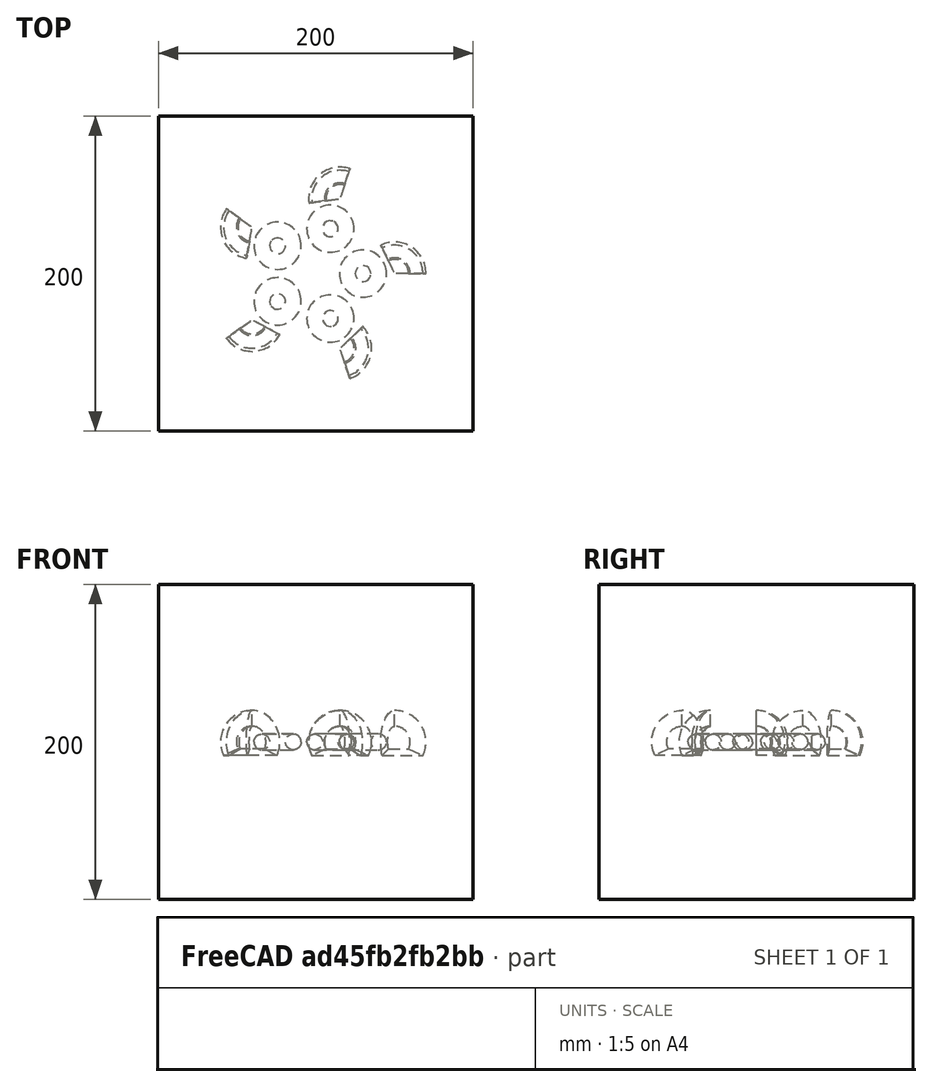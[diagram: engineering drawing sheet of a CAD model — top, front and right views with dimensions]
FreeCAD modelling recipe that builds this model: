
FCSTD DOCUMENT  (FreeCAD 0.19RUnknown)
Label: arrayTest-7
License: All rights reserved
LicenseURL: http://en.wikipedia.org/wiki/All_rights_reserved
objects: App::DocumentObjectGroupPython×1248, Part::FeaturePython×4, App::Part×2, Part::MultiFuse×1
note: 5 computed .brp shape members not serialized (recipe doc carries the construction recipe); baked Part::Feature solids carry a one-line shape summary decoded from their .brp

FEATURE [App::DocumentObjectGroupPython] HALFPI  # scripted group (container) (typed FeaturePython)
  name = HALFPI
  value = pi/2.
FEATURE [App::DocumentObjectGroupPython] PI  # scripted group (container) (typed FeaturePython)
  name = PI
  value = 1.*pi
FEATURE [App::DocumentObjectGroupPython] TWOPI  # scripted group (container) (typed FeaturePython)
  name = TWOPI
  value = 2.*pi
FEATURE [App::DocumentObjectGroupPython] Constants  # scripted group (container) (typed FeaturePython)
  Group = -> [HALFPI,PI,TWOPI]
FEATURE [App::DocumentObjectGroupPython] Variables  # scripted group (container) (typed FeaturePython)
FEATURE [App::DocumentObjectGroupPython] Quantities  # scripted group (container) (typed FeaturePython)
FEATURE [App::DocumentObjectGroupPython] Isotopes  # scripted group (container) (typed FeaturePython)
FEATURE [App::DocumentObjectGroupPython] Elements  # scripted group (container) (typed FeaturePython)
FEATURE [App::DocumentObjectGroupPython] G4Isotopes  # scripted group (container) (typed FeaturePython)
FEATURE [App::DocumentObjectGroupPython] H_element  # scripted group (container) (typed FeaturePython)
  Z = 1
  atom_value = 1.008
  formula = H
  name = H_element
FEATURE [App::DocumentObjectGroupPython] He_element  # scripted group (container) (typed FeaturePython)
  Z = 2
  atom_value = 4.0026
  formula = He
  name = He_element
FEATURE [App::DocumentObjectGroupPython] Li_element  # scripted group (container) (typed FeaturePython)
  Z = 3
  atom_value = 6.94
  formula = Li
  name = Li_element
FEATURE [App::DocumentObjectGroupPython] Be_element  # scripted group (container) (typed FeaturePython)
  Z = 4
  atom_value = 9.01218
  formula = Be
  name = Be_element
FEATURE [App::DocumentObjectGroupPython] B_element  # scripted group (container) (typed FeaturePython)
  Z = 5
  atom_value = 10.81
  formula = B
  name = B_element
FEATURE [App::DocumentObjectGroupPython] C_element  # scripted group (container) (typed FeaturePython)
  Z = 6
  atom_value = 12.011
  formula = C
  name = C_element
FEATURE [App::DocumentObjectGroupPython] N_element  # scripted group (container) (typed FeaturePython)
  Z = 7
  atom_value = 14.007
  formula = N
  name = N_element
FEATURE [App::DocumentObjectGroupPython] O_element  # scripted group (container) (typed FeaturePython)
  Z = 8
  atom_value = 15.999
  formula = O
  name = O_element
FEATURE [App::DocumentObjectGroupPython] F_element  # scripted group (container) (typed FeaturePython)
  Z = 9
  atom_value = 18.9984
  formula = F
  name = F_element
FEATURE [App::DocumentObjectGroupPython] Ne_element  # scripted group (container) (typed FeaturePython)
  Z = 10
  atom_value = 20.1797
  formula = Ne
  name = Ne_element
FEATURE [App::DocumentObjectGroupPython] Na_element  # scripted group (container) (typed FeaturePython)
  Z = 11
  atom_value = 22.9898
  formula = Na
  name = Na_element
FEATURE [App::DocumentObjectGroupPython] Mg_element  # scripted group (container) (typed FeaturePython)
  Z = 12
  atom_value = 24.305
  formula = Mg
  name = Mg_element
FEATURE [App::DocumentObjectGroupPython] Al_element  # scripted group (container) (typed FeaturePython)
  Z = 13
  atom_value = 26.9815
  formula = Al
  name = Al_element
FEATURE [App::DocumentObjectGroupPython] Si_element  # scripted group (container) (typed FeaturePython)
  Z = 14
  atom_value = 28.085
  formula = Si
  name = Si_element
FEATURE [App::DocumentObjectGroupPython] P_element  # scripted group (container) (typed FeaturePython)
  Z = 15
  atom_value = 30.9738
  formula = P
  name = P_element
FEATURE [App::DocumentObjectGroupPython] S_element  # scripted group (container) (typed FeaturePython)
  Z = 16
  atom_value = 32.06
  formula = S
  name = S_element
FEATURE [App::DocumentObjectGroupPython] Cl_element  # scripted group (container) (typed FeaturePython)
  Z = 17
  atom_value = 35.45
  formula = Cl
  name = Cl_element
FEATURE [App::DocumentObjectGroupPython] Ar_element  # scripted group (container) (typed FeaturePython)
  Z = 18
  atom_value = 39.95
  formula = Ar
  name = Ar_element
FEATURE [App::DocumentObjectGroupPython] K_element  # scripted group (container) (typed FeaturePython)
  Z = 19
  atom_value = 39.0983
  formula = K
  name = K_element
FEATURE [App::DocumentObjectGroupPython] Ca_element  # scripted group (container) (typed FeaturePython)
  Z = 20
  atom_value = 40.078
  formula = Ca
  name = Ca_element
FEATURE [App::DocumentObjectGroupPython] Sc_element  # scripted group (container) (typed FeaturePython)
  Z = 21
  atom_value = 44.9559
  formula = Sc
  name = Sc_element
FEATURE [App::DocumentObjectGroupPython] Ti_element  # scripted group (container) (typed FeaturePython)
  Z = 22
  atom_value = 47.867
  formula = Ti
  name = Ti_element
FEATURE [App::DocumentObjectGroupPython] V_element  # scripted group (container) (typed FeaturePython)
  Z = 23
  atom_value = 50.9415
  formula = V
  name = V_element
FEATURE [App::DocumentObjectGroupPython] Cr_element  # scripted group (container) (typed FeaturePython)
  Z = 24
  atom_value = 51.9961
  formula = Cr
  name = Cr_element
FEATURE [App::DocumentObjectGroupPython] Mn_element  # scripted group (container) (typed FeaturePython)
  Z = 25
  atom_value = 54.938
  formula = Mn
  name = Mn_element
FEATURE [App::DocumentObjectGroupPython] Fe_element  # scripted group (container) (typed FeaturePython)
  Z = 26
  atom_value = 55.845
  formula = Fe
  name = Fe_element
FEATURE [App::DocumentObjectGroupPython] Co_element  # scripted group (container) (typed FeaturePython)
  Z = 27
  atom_value = 58.9332
  formula = Co
  name = Co_element
FEATURE [App::DocumentObjectGroupPython] Ni_element  # scripted group (container) (typed FeaturePython)
  Z = 28
  atom_value = 58.6934
  formula = Ni
  name = Ni_element
FEATURE [App::DocumentObjectGroupPython] Cu_element  # scripted group (container) (typed FeaturePython)
  Z = 29
  atom_value = 63.546
  formula = Cu
  name = Cu_element
FEATURE [App::DocumentObjectGroupPython] Zn_element  # scripted group (container) (typed FeaturePython)
  Z = 30
  atom_value = 65.38
  formula = Zn
  name = Zn_element
FEATURE [App::DocumentObjectGroupPython] Ga_element  # scripted group (container) (typed FeaturePython)
  Z = 31
  atom_value = 69.723
  formula = Ga
  name = Ga_element
FEATURE [App::DocumentObjectGroupPython] Ge_element  # scripted group (container) (typed FeaturePython)
  Z = 32
  atom_value = 72.63
  formula = Ge
  name = Ge_element
FEATURE [App::DocumentObjectGroupPython] As_element  # scripted group (container) (typed FeaturePython)
  Z = 33
  atom_value = 74.9216
  formula = As
  name = As_element
FEATURE [App::DocumentObjectGroupPython] Se_element  # scripted group (container) (typed FeaturePython)
  Z = 34
  atom_value = 78.971
  formula = Se
  name = Se_element
FEATURE [App::DocumentObjectGroupPython] Br_element  # scripted group (container) (typed FeaturePython)
  Z = 35
  atom_value = 79.904
  formula = Br
  name = Br_element
FEATURE [App::DocumentObjectGroupPython] Kr_element  # scripted group (container) (typed FeaturePython)
  Z = 36
  atom_value = 83.798
  formula = Kr
  name = Kr_element
FEATURE [App::DocumentObjectGroupPython] Rb_element  # scripted group (container) (typed FeaturePython)
  Z = 37
  atom_value = 85.4678
  formula = Rb
  name = Rb_element
FEATURE [App::DocumentObjectGroupPython] Sr_element  # scripted group (container) (typed FeaturePython)
  Z = 38
  atom_value = 87.62
  formula = Sr
  name = Sr_element
FEATURE [App::DocumentObjectGroupPython] Y_element  # scripted group (container) (typed FeaturePython)
  Z = 39
  atom_value = 88.9058
  formula = Y
  name = Y_element
FEATURE [App::DocumentObjectGroupPython] Zr_element  # scripted group (container) (typed FeaturePython)
  Z = 40
  atom_value = 91.224
  formula = Zr
  name = Zr_element
FEATURE [App::DocumentObjectGroupPython] Nb_element  # scripted group (container) (typed FeaturePython)
  Z = 41
  atom_value = 92.9064
  formula = Nb
  name = Nb_element
FEATURE [App::DocumentObjectGroupPython] Mo_element  # scripted group (container) (typed FeaturePython)
  Z = 42
  atom_value = 95.95
  formula = Mo
  name = Mo_element
FEATURE [App::DocumentObjectGroupPython] Tc_element  # scripted group (container) (typed FeaturePython)
  Z = 43
  atom_value = 97
  formula = Tc
  name = Tc_element
FEATURE [App::DocumentObjectGroupPython] Ru_element  # scripted group (container) (typed FeaturePython)
  Z = 44
  atom_value = 101.07
  formula = Ru
  name = Ru_element
FEATURE [App::DocumentObjectGroupPython] Rh_element  # scripted group (container) (typed FeaturePython)
  Z = 45
  atom_value = 102.905
  formula = Rh
  name = Rh_element
FEATURE [App::DocumentObjectGroupPython] Pd_element  # scripted group (container) (typed FeaturePython)
  Z = 46
  atom_value = 106.42
  formula = Pd
  name = Pd_element
FEATURE [App::DocumentObjectGroupPython] Ag_element  # scripted group (container) (typed FeaturePython)
  Z = 47
  atom_value = 107.868
  formula = Ag
  name = Ag_element
FEATURE [App::DocumentObjectGroupPython] Cd_element  # scripted group (container) (typed FeaturePython)
  Z = 48
  atom_value = 112.414
  formula = Cd
  name = Cd_element
FEATURE [App::DocumentObjectGroupPython] In_element  # scripted group (container) (typed FeaturePython)
  Z = 49
  atom_value = 114.818
  formula = In
  name = In_element
FEATURE [App::DocumentObjectGroupPython] Sn_element  # scripted group (container) (typed FeaturePython)
  Z = 50
  atom_value = 118.71
  formula = Sn
  name = Sn_element
FEATURE [App::DocumentObjectGroupPython] Sb_element  # scripted group (container) (typed FeaturePython)
  Z = 51
  atom_value = 121.76
  formula = Sb
  name = Sb_element
FEATURE [App::DocumentObjectGroupPython] Te_element  # scripted group (container) (typed FeaturePython)
  Z = 52
  atom_value = 127.6
  formula = Te
  name = Te_element
FEATURE [App::DocumentObjectGroupPython] I_element  # scripted group (container) (typed FeaturePython)
  Z = 53
  atom_value = 126.904
  formula = I
  name = I_element
FEATURE [App::DocumentObjectGroupPython] Xe_element  # scripted group (container) (typed FeaturePython)
  Z = 54
  atom_value = 131.293
  formula = Xe
  name = Xe_element
FEATURE [App::DocumentObjectGroupPython] Cs_element  # scripted group (container) (typed FeaturePython)
  Z = 55
  atom_value = 132.905
  formula = Cs
  name = Cs_element
FEATURE [App::DocumentObjectGroupPython] Ba_element  # scripted group (container) (typed FeaturePython)
  Z = 56
  atom_value = 137.327
  formula = Ba
  name = Ba_element
FEATURE [App::DocumentObjectGroupPython] La_element  # scripted group (container) (typed FeaturePython)
  Z = 57
  atom_value = 138.905
  formula = La
  name = La_element
FEATURE [App::DocumentObjectGroupPython] Ce_element  # scripted group (container) (typed FeaturePython)
  Z = 58
  atom_value = 140.116
  formula = Ce
  name = Ce_element
FEATURE [App::DocumentObjectGroupPython] Pr_element  # scripted group (container) (typed FeaturePython)
  Z = 59
  atom_value = 140.908
  formula = Pr
  name = Pr_element
FEATURE [App::DocumentObjectGroupPython] Nd_element  # scripted group (container) (typed FeaturePython)
  Z = 60
  atom_value = 144.242
  formula = Nd
  name = Nd_element
FEATURE [App::DocumentObjectGroupPython] Pm_element  # scripted group (container) (typed FeaturePython)
  Z = 61
  atom_value = 145
  formula = Pm
  name = Pm_element
FEATURE [App::DocumentObjectGroupPython] Sm_element  # scripted group (container) (typed FeaturePython)
  Z = 62
  atom_value = 150.36
  formula = Sm
  name = Sm_element
FEATURE [App::DocumentObjectGroupPython] Eu_element  # scripted group (container) (typed FeaturePython)
  Z = 63
  atom_value = 151.964
  formula = Eu
  name = Eu_element
FEATURE [App::DocumentObjectGroupPython] Gd_element  # scripted group (container) (typed FeaturePython)
  Z = 64
  atom_value = 157.25
  formula = Gd
  name = Gd_element
FEATURE [App::DocumentObjectGroupPython] Tb_element  # scripted group (container) (typed FeaturePython)
  Z = 65
  atom_value = 158.925
  formula = Tb
  name = Tb_element
FEATURE [App::DocumentObjectGroupPython] Dy_element  # scripted group (container) (typed FeaturePython)
  Z = 66
  atom_value = 162.5
  formula = Dy
  name = Dy_element
FEATURE [App::DocumentObjectGroupPython] Ho_element  # scripted group (container) (typed FeaturePython)
  Z = 67
  atom_value = 164.93
  formula = Ho
  name = Ho_element
FEATURE [App::DocumentObjectGroupPython] Er_element  # scripted group (container) (typed FeaturePython)
  Z = 68
  atom_value = 167.259
  formula = Er
  name = Er_element
FEATURE [App::DocumentObjectGroupPython] Tm_element  # scripted group (container) (typed FeaturePython)
  Z = 69
  atom_value = 168.934
  formula = Tm
  name = Tm_element
FEATURE [App::DocumentObjectGroupPython] Yb_element  # scripted group (container) (typed FeaturePython)
  Z = 70
  atom_value = 173.045
  formula = Yb
  name = Yb_element
FEATURE [App::DocumentObjectGroupPython] Lu_element  # scripted group (container) (typed FeaturePython)
  Z = 71
  atom_value = 174.967
  formula = Lu
  name = Lu_element
FEATURE [App::DocumentObjectGroupPython] Hf_element  # scripted group (container) (typed FeaturePython)
  Z = 72
  atom_value = 178.49
  formula = Hf
  name = Hf_element
FEATURE [App::DocumentObjectGroupPython] Ta_element  # scripted group (container) (typed FeaturePython)
  Z = 73
  atom_value = 180.948
  formula = Ta
  name = Ta_element
FEATURE [App::DocumentObjectGroupPython] W_element  # scripted group (container) (typed FeaturePython)
  Z = 74
  atom_value = 183.84
  formula = W
  name = W_element
FEATURE [App::DocumentObjectGroupPython] Re_element  # scripted group (container) (typed FeaturePython)
  Z = 75
  atom_value = 186.207
  formula = Re
  name = Re_element
FEATURE [App::DocumentObjectGroupPython] Os_element  # scripted group (container) (typed FeaturePython)
  Z = 76
  atom_value = 190.23
  formula = Os
  name = Os_element
FEATURE [App::DocumentObjectGroupPython] Ir_element  # scripted group (container) (typed FeaturePython)
  Z = 77
  atom_value = 192.217
  formula = Ir
  name = Ir_element
FEATURE [App::DocumentObjectGroupPython] Pt_element  # scripted group (container) (typed FeaturePython)
  Z = 78
  atom_value = 195.084
  formula = Pt
  name = Pt_element
FEATURE [App::DocumentObjectGroupPython] Au_element  # scripted group (container) (typed FeaturePython)
  Z = 79
  atom_value = 196.967
  formula = Au
  name = Au_element
FEATURE [App::DocumentObjectGroupPython] Hg_element  # scripted group (container) (typed FeaturePython)
  Z = 80
  atom_value = 200.592
  formula = Hg
  name = Hg_element
FEATURE [App::DocumentObjectGroupPython] Tl_element  # scripted group (container) (typed FeaturePython)
  Z = 81
  atom_value = 204.38
  formula = Tl
  name = Tl_element
FEATURE [App::DocumentObjectGroupPython] Pb_element  # scripted group (container) (typed FeaturePython)
  Z = 82
  atom_value = 207.2
  formula = Pb
  name = Pb_element
FEATURE [App::DocumentObjectGroupPython] Bi_element  # scripted group (container) (typed FeaturePython)
  Z = 83
  atom_value = 208.98
  formula = Bi
  name = Bi_element
FEATURE [App::DocumentObjectGroupPython] Po_element  # scripted group (container) (typed FeaturePython)
  Z = 84
  atom_value = 209
  formula = Po
  name = Po_element
FEATURE [App::DocumentObjectGroupPython] At_element  # scripted group (container) (typed FeaturePython)
  Z = 85
  atom_value = 210
  formula = At
  name = At_element
FEATURE [App::DocumentObjectGroupPython] Rn_element  # scripted group (container) (typed FeaturePython)
  Z = 86
  atom_value = 222
  formula = Rn
  name = Rn_element
FEATURE [App::DocumentObjectGroupPython] Fr_element  # scripted group (container) (typed FeaturePython)
  Z = 87
  atom_value = 223
  formula = Fr
  name = Fr_element
FEATURE [App::DocumentObjectGroupPython] Ra_element  # scripted group (container) (typed FeaturePython)
  Z = 88
  atom_value = 226
  formula = Ra
  name = Ra_element
FEATURE [App::DocumentObjectGroupPython] Ac_element  # scripted group (container) (typed FeaturePython)
  Z = 89
  atom_value = 227
  formula = Ac
  name = Ac_element
FEATURE [App::DocumentObjectGroupPython] Th_element  # scripted group (container) (typed FeaturePython)
  Z = 90
  atom_value = 232.038
  formula = Th
  name = Th_element
FEATURE [App::DocumentObjectGroupPython] Pa_element  # scripted group (container) (typed FeaturePython)
  Z = 91
  atom_value = 231.036
  formula = Pa
  name = Pa_element
FEATURE [App::DocumentObjectGroupPython] U_element  # scripted group (container) (typed FeaturePython)
  Z = 92
  atom_value = 238.029
  formula = U
  name = U_element
FEATURE [App::DocumentObjectGroupPython] Np_element  # scripted group (container) (typed FeaturePython)
  Z = 93
  atom_value = 237
  formula = Np
  name = Np_element
FEATURE [App::DocumentObjectGroupPython] Pu_element  # scripted group (container) (typed FeaturePython)
  Z = 94
  atom_value = 244
  formula = Pu
  name = Pu_element
FEATURE [App::DocumentObjectGroupPython] Am_element  # scripted group (container) (typed FeaturePython)
  Z = 95
  atom_value = 243
  formula = Am
  name = Am_element
FEATURE [App::DocumentObjectGroupPython] Cm_element  # scripted group (container) (typed FeaturePython)
  Z = 96
  atom_value = 247
  formula = Cm
  name = Cm_element
FEATURE [App::DocumentObjectGroupPython] Bk_element  # scripted group (container) (typed FeaturePython)
  Z = 97
  atom_value = 247
  formula = Bk
  name = Bk_element
FEATURE [App::DocumentObjectGroupPython] Cf_element  # scripted group (container) (typed FeaturePython)
  Z = 98
  atom_value = 251
  formula = Cf
  name = Cf_element
FEATURE [App::DocumentObjectGroupPython] G4Elements  # scripted group (container) (typed FeaturePython)
  Group = -> [H_element,He_element,Li_element,Be_element,B_element,C_element,N_element,O_element,F_element,Ne_element,Na_element,Mg_element,Al_element,Si_element,P_element,S_element,Cl_element,Ar_element,K_element,Ca_element,Sc_element,Ti_element,V_element,Cr_element,Mn_element,Fe_element,Co_element,Ni_element,Cu_element,Zn_element,Ga_element,Ge_element,As_element,Se_element,Br_element,Kr_element,Rb_element,+61 more]
FEATURE [App::DocumentObjectGroupPython] H_element001  label="H_element : 0.101"  # scripted group (container) (typed FeaturePython)
  n = 0.101327
FEATURE [App::DocumentObjectGroupPython] C_element001  label="C_element : 0.775"  # scripted group (container) (typed FeaturePython)
  n = 0.7755
FEATURE [App::DocumentObjectGroupPython] N_element001  label="N_element : 0.035"  # scripted group (container) (typed FeaturePython)
  n = 0.035057
FEATURE [App::DocumentObjectGroupPython] O_element001  label="O_element : 0.052"  # scripted group (container) (typed FeaturePython)
  n = 0.0523159
FEATURE [App::DocumentObjectGroupPython] F_element001  label="F_element : 0.017"  # scripted group (container) (typed FeaturePython)
  n = 0.017422
FEATURE [App::DocumentObjectGroupPython] Ca_element001  label="Ca_element : 0.018"  # scripted group (container) (typed FeaturePython)
  n = 0.018378
FEATURE [App::DocumentObjectGroupPython] G4_A_150_TISSUE  label="G4_A-150_TISSUE"  # scripted group (container) (typed FeaturePython)
  Dunit = g/cm3
  Dvalue = 1.127
  Group = -> [H_element001,C_element001,N_element001,O_element001,F_element001,Ca_element001]
  conduct = 2
  density = 1
  expand = 3
  formula = G4_A-150_TISSUE
  name = G4_A-150_TISSUE
  specific = 4
FEATURE [App::DocumentObjectGroupPython] C_element002  label="C_element : 3"  # scripted group (container) (typed FeaturePython)
  n = 3
  ref = C_element
FEATURE [App::DocumentObjectGroupPython] H_element002  label="H_element : 6"  # scripted group (container) (typed FeaturePython)
  n = 6
  ref = H_element
FEATURE [App::DocumentObjectGroupPython] O_element002  label="O_element : 1"  # scripted group (container) (typed FeaturePython)
  n = 1
  ref = O_element
FEATURE [App::DocumentObjectGroupPython] G4_ACETONE  # scripted group (container) (typed FeaturePython)
  Dunit = g/cm3
  Dvalue = 0.7899
  Group = -> [C_element002,H_element002,O_element002]
  conduct = 2
  density = 1
  expand = 3
  formula = G4_ACETONE
  name = G4_ACETONE
  specific = 4
FEATURE [App::DocumentObjectGroupPython] C_element003  label="C_element : 2"  # scripted group (container) (typed FeaturePython)
  n = 2
  ref = C_element
FEATURE [App::DocumentObjectGroupPython] H_element003  label="H_element : 2"  # scripted group (container) (typed FeaturePython)
  n = 2
  ref = H_element
FEATURE [App::DocumentObjectGroupPython] G4_ACETYLENE  # scripted group (container) (typed FeaturePython)
  Dunit = g/cm3
  Dvalue = 0.0010967
  Group = -> [C_element003,H_element003]
  conduct = 2
  density = 1
  expand = 3
  formula = G4_ACETYLENE
  name = G4_ACETYLENE
  specific = 4
FEATURE [App::DocumentObjectGroupPython] C_element004  label="C_element : 5"  # scripted group (container) (typed FeaturePython)
  n = 5
  ref = C_element
FEATURE [App::DocumentObjectGroupPython] H_element004  label="H_element : 5"  # scripted group (container) (typed FeaturePython)
  n = 5
  ref = H_element
FEATURE [App::DocumentObjectGroupPython] N_element002  label="N_element : 5"  # scripted group (container) (typed FeaturePython)
  n = 5
  ref = N_element
FEATURE [App::DocumentObjectGroupPython] G4_ADENINE  # scripted group (container) (typed FeaturePython)
  Dunit = g/cm3
  Dvalue = 1.6
  Group = -> [C_element004,H_element004,N_element002]
  conduct = 2
  density = 1
  expand = 3
  formula = G4_ADENINE
  name = G4_ADENINE
  specific = 4
FEATURE [App::DocumentObjectGroupPython] H_element005  label="H_element : 0.114"  # scripted group (container) (typed FeaturePython)
  n = 0.114
FEATURE [App::DocumentObjectGroupPython] C_element005  label="C_element : 0.598"  # scripted group (container) (typed FeaturePython)
  n = 0.598
FEATURE [App::DocumentObjectGroupPython] N_element003  label="N_element : 0.007"  # scripted group (container) (typed FeaturePython)
  n = 0.007
FEATURE [App::DocumentObjectGroupPython] O_element003  label="O_element : 0.278"  # scripted group (container) (typed FeaturePython)
  n = 0.278
FEATURE [App::DocumentObjectGroupPython] Na_element001  label="Na_element : 0.001"  # scripted group (container) (typed FeaturePython)
  n = 0.001
FEATURE [App::DocumentObjectGroupPython] S_element001  label="S_element : 0.001"  # scripted group (container) (typed FeaturePython)
  n = 0.001
FEATURE [App::DocumentObjectGroupPython] Cl_element001  label="Cl_element : 0.001"  # scripted group (container) (typed FeaturePython)
  n = 0.001
FEATURE [App::DocumentObjectGroupPython] G4_ADIPOSE_TISSUE_ICRP  # scripted group (container) (typed FeaturePython)
  Dunit = g/cm3
  Dvalue = 0.95
  Group = -> [H_element005,C_element005,N_element003,O_element003,Na_element001,S_element001,Cl_element001]
  conduct = 2
  density = 1
  expand = 3
  formula = G4_ADIPOSE_TISSUE_ICRP
  name = G4_ADIPOSE_TISSUE_ICRP
  specific = 4
FEATURE [App::DocumentObjectGroupPython] C_element006  label="C_element : 0.000"  # scripted group (container) (typed FeaturePython)
  n = 0.000124
FEATURE [App::DocumentObjectGroupPython] N_element004  label="N_element : 0.755"  # scripted group (container) (typed FeaturePython)
  n = 0.755268
FEATURE [App::DocumentObjectGroupPython] O_element004  label="O_element : 0.232"  # scripted group (container) (typed FeaturePython)
  n = 0.231781
FEATURE [App::DocumentObjectGroupPython] Ar_element001  label="Ar_element : 0.013"  # scripted group (container) (typed FeaturePython)
  n = 0.012827
FEATURE [App::DocumentObjectGroupPython] G4_AIR  # scripted group (container) (typed FeaturePython)
  Dunit = g/cm3
  Dvalue = 0.00120479
  Group = -> [C_element006,N_element004,O_element004,Ar_element001]
  conduct = 2
  density = 1
  expand = 3
  formula = G4_AIR
  name = G4_AIR
  specific = 4
FEATURE [App::DocumentObjectGroupPython] C_element007  label="C_element : 006"  # scripted group (container) (typed FeaturePython)
  n = 3
  ref = C_element
FEATURE [App::DocumentObjectGroupPython] H_element006  label="H_element : 7"  # scripted group (container) (typed FeaturePython)
  n = 7
  ref = H_element
FEATURE [App::DocumentObjectGroupPython] N_element005  label="N_element : 1"  # scripted group (container) (typed FeaturePython)
  n = 1
  ref = N_element
FEATURE [App::DocumentObjectGroupPython] O_element005  label="O_element : 2"  # scripted group (container) (typed FeaturePython)
  n = 2
  ref = O_element
FEATURE [App::DocumentObjectGroupPython] G4_ALANINE  # scripted group (container) (typed FeaturePython)
  Dunit = g/cm3
  Dvalue = 1.42
  Group = -> [C_element007,H_element006,N_element005,O_element005]
  conduct = 2
  density = 1
  expand = 3
  formula = G4_ALANINE
  name = G4_ALANINE
  specific = 4
FEATURE [App::DocumentObjectGroupPython] Al_element001  label="Al_element : 2"  # scripted group (container) (typed FeaturePython)
  n = 2
  ref = Al_element
FEATURE [App::DocumentObjectGroupPython] O_element006  label="O_element : 3"  # scripted group (container) (typed FeaturePython)
  n = 3
  ref = O_element
FEATURE [App::DocumentObjectGroupPython] G4_ALUMINUM_OXIDE  # scripted group (container) (typed FeaturePython)
  Dunit = g/cm3
  Dvalue = 3.97
  Group = -> [Al_element001,O_element006]
  conduct = 2
  density = 1
  expand = 3
  formula = G4_ALUMINUM_OXIDE
  name = G4_ALUMINUM_OXIDE
  specific = 4
FEATURE [App::DocumentObjectGroupPython] H_element007  label="H_element : 0.106"  # scripted group (container) (typed FeaturePython)
  n = 0.10593
FEATURE [App::DocumentObjectGroupPython] C_element008  label="C_element : 0.789"  # scripted group (container) (typed FeaturePython)
  n = 0.788974
FEATURE [App::DocumentObjectGroupPython] O_element007  label="O_element : 0.105"  # scripted group (container) (typed FeaturePython)
  n = 0.105096
FEATURE [App::DocumentObjectGroupPython] G4_AMBER  # scripted group (container) (typed FeaturePython)
  Dunit = g/cm3
  Dvalue = 1.1
  Group = -> [H_element007,C_element008,O_element007]
  conduct = 2
  density = 1
  expand = 3
  formula = G4_AMBER
  name = G4_AMBER
  specific = 4
FEATURE [App::DocumentObjectGroupPython] N_element006  label="N_element : 006"  # scripted group (container) (typed FeaturePython)
  n = 1
  ref = N_element
FEATURE [App::DocumentObjectGroupPython] H_element008  label="H_element : 3"  # scripted group (container) (typed FeaturePython)
  n = 3
  ref = H_element
FEATURE [App::DocumentObjectGroupPython] G4_AMMONIA  # scripted group (container) (typed FeaturePython)
  Dunit = g/cm3
  Dvalue = 0.000826019
  Group = -> [N_element006,H_element008]
  conduct = 2
  density = 1
  expand = 3
  formula = G4_AMMONIA
  name = G4_AMMONIA
  specific = 4
FEATURE [App::DocumentObjectGroupPython] C_element009  label="C_element : 6"  # scripted group (container) (typed FeaturePython)
  n = 6
  ref = C_element
FEATURE [App::DocumentObjectGroupPython] H_element009  label="H_element : 008"  # scripted group (container) (typed FeaturePython)
  n = 7
  ref = H_element
FEATURE [App::DocumentObjectGroupPython] N_element007  label="N_element : 007"  # scripted group (container) (typed FeaturePython)
  n = 1
  ref = N_element
FEATURE [App::DocumentObjectGroupPython] G4_ANILINE  # scripted group (container) (typed FeaturePython)
  Dunit = g/cm3
  Dvalue = 1.0235
  Group = -> [C_element009,H_element009,N_element007]
  conduct = 2
  density = 1
  expand = 3
  formula = G4_ANILINE
  name = G4_ANILINE
  specific = 4
FEATURE [App::DocumentObjectGroupPython] C_element010  label="C_element : 14"  # scripted group (container) (typed FeaturePython)
  n = 14
  ref = C_element
FEATURE [App::DocumentObjectGroupPython] H_element010  label="H_element : 10"  # scripted group (container) (typed FeaturePython)
  n = 10
  ref = H_element
FEATURE [App::DocumentObjectGroupPython] G4_ANTHRACENE  # scripted group (container) (typed FeaturePython)
  Dunit = g/cm3
  Dvalue = 1.283
  Group = -> [C_element010,H_element010]
  conduct = 2
  density = 1
  expand = 3
  formula = G4_ANTHRACENE
  name = G4_ANTHRACENE
  specific = 4
FEATURE [App::DocumentObjectGroupPython] H_element011  label="H_element : 0.065"  # scripted group (container) (typed FeaturePython)
  n = 0.0654709
FEATURE [App::DocumentObjectGroupPython] C_element011  label="C_element : 0.537"  # scripted group (container) (typed FeaturePython)
  n = 0.536944
FEATURE [App::DocumentObjectGroupPython] N_element008  label="N_element : 0.021"  # scripted group (container) (typed FeaturePython)
  n = 0.0215
FEATURE [App::DocumentObjectGroupPython] O_element008  label="O_element : 0.032"  # scripted group (container) (typed FeaturePython)
  n = 0.032085
FEATURE [App::DocumentObjectGroupPython] F_element002  label="F_element : 0.167"  # scripted group (container) (typed FeaturePython)
  n = 0.167411
FEATURE [App::DocumentObjectGroupPython] Ca_element002  label="Ca_element : 0.177"  # scripted group (container) (typed FeaturePython)
  n = 0.176589
FEATURE [App::DocumentObjectGroupPython] G4_B_100_BONE  label="G4_B-100_BONE"  # scripted group (container) (typed FeaturePython)
  Dunit = g/cm3
  Dvalue = 1.45
  Group = -> [H_element011,C_element011,N_element008,O_element008,F_element002,Ca_element002]
  conduct = 2
  density = 1
  expand = 3
  formula = G4_B-100_BONE
  name = G4_B-100_BONE
  specific = 4
FEATURE [App::DocumentObjectGroupPython] H_element012  label="H_element : 0.057"  # scripted group (container) (typed FeaturePython)
  n = 0.057441
FEATURE [App::DocumentObjectGroupPython] C_element012  label="C_element : 0.790"  # scripted group (container) (typed FeaturePython)
  n = 0.774591
FEATURE [App::DocumentObjectGroupPython] O_element009  label="O_element : 0.168"  # scripted group (container) (typed FeaturePython)
  n = 0.167968
FEATURE [App::DocumentObjectGroupPython] G4_BAKELITE  # scripted group (container) (typed FeaturePython)
  Dunit = g/cm3
  Dvalue = 1.25
  Group = -> [H_element012,C_element012,O_element009]
  conduct = 2
  density = 1
  expand = 3
  formula = G4_BAKELITE
  name = G4_BAKELITE
  specific = 4
FEATURE [App::DocumentObjectGroupPython] Ba_element001  label="Ba_element : 1"  # scripted group (container) (typed FeaturePython)
  n = 1
  ref = Ba_element
FEATURE [App::DocumentObjectGroupPython] F_element003  label="F_element : 2"  # scripted group (container) (typed FeaturePython)
  n = 2
  ref = F_element
FEATURE [App::DocumentObjectGroupPython] G4_BARIUM_FLUORIDE  # scripted group (container) (typed FeaturePython)
  Dunit = g/cm3
  Dvalue = 4.89
  Group = -> [Ba_element001,F_element003]
  conduct = 2
  density = 1
  expand = 3
  formula = G4_BARIUM_FLUORIDE
  name = G4_BARIUM_FLUORIDE
  specific = 4
FEATURE [App::DocumentObjectGroupPython] Ba_element002  label="Ba_element : 002"  # scripted group (container) (typed FeaturePython)
  n = 1
  ref = Ba_element
FEATURE [App::DocumentObjectGroupPython] S_element002  label="S_element : 1"  # scripted group (container) (typed FeaturePython)
  n = 1
  ref = S_element
FEATURE [App::DocumentObjectGroupPython] O_element010  label="O_element : 4"  # scripted group (container) (typed FeaturePython)
  n = 4
  ref = O_element
FEATURE [App::DocumentObjectGroupPython] G4_BARIUM_SULFATE  # scripted group (container) (typed FeaturePython)
  Dunit = g/cm3
  Dvalue = 4.5
  Group = -> [Ba_element002,S_element002,O_element010]
  conduct = 2
  density = 1
  expand = 3
  formula = G4_BARIUM_SULFATE
  name = G4_BARIUM_SULFATE
  specific = 4
FEATURE [App::DocumentObjectGroupPython] C_element013  label="C_element : 007"  # scripted group (container) (typed FeaturePython)
  n = 6
  ref = C_element
FEATURE [App::DocumentObjectGroupPython] H_element013  label="H_element : 009"  # scripted group (container) (typed FeaturePython)
  n = 6
  ref = H_element
FEATURE [App::DocumentObjectGroupPython] G4_BENZENE  # scripted group (container) (typed FeaturePython)
  Dunit = g/cm3
  Dvalue = 0.87865
  Group = -> [C_element013,H_element013]
  conduct = 2
  density = 1
  expand = 3
  formula = G4_BENZENE
  name = G4_BENZENE
  specific = 4
FEATURE [App::DocumentObjectGroupPython] Be_element001  label="Be_element : 1"  # scripted group (container) (typed FeaturePython)
  n = 1
  ref = Be_element
FEATURE [App::DocumentObjectGroupPython] O_element011  label="O_element : 005"  # scripted group (container) (typed FeaturePython)
  n = 1
  ref = O_element
FEATURE [App::DocumentObjectGroupPython] G4_BERYLLIUM_OXIDE  # scripted group (container) (typed FeaturePython)
  Dunit = g/cm3
  Dvalue = 3.01
  Group = -> [Be_element001,O_element011]
  conduct = 2
  density = 1
  expand = 3
  formula = G4_BERYLLIUM_OXIDE
  name = G4_BERYLLIUM_OXIDE
  specific = 4
FEATURE [App::DocumentObjectGroupPython] Bi_element001  label="Bi_element : 4"  # scripted group (container) (typed FeaturePython)
  n = 4
  ref = Bi_element
FEATURE [App::DocumentObjectGroupPython] Ge_element001  label="Ge_element : 3"  # scripted group (container) (typed FeaturePython)
  n = 3
  ref = Ge_element
FEATURE [App::DocumentObjectGroupPython] O_element012  label="O_element : 12"  # scripted group (container) (typed FeaturePython)
  n = 12
  ref = O_element
FEATURE [App::DocumentObjectGroupPython] G4_BGO  # scripted group (container) (typed FeaturePython)
  Dunit = g/cm3
  Dvalue = 7.13
  Group = -> [Bi_element001,Ge_element001,O_element012]
  conduct = 2
  density = 1
  expand = 3
  formula = G4_BGO
  name = G4_BGO
  specific = 4
FEATURE [App::DocumentObjectGroupPython] H_element014  label="H_element : 0.102"  # scripted group (container) (typed FeaturePython)
  n = 0.102
FEATURE [App::DocumentObjectGroupPython] C_element014  label="C_element : 0.110"  # scripted group (container) (typed FeaturePython)
  n = 0.11
FEATURE [App::DocumentObjectGroupPython] N_element009  label="N_element : 0.033"  # scripted group (container) (typed FeaturePython)
  n = 0.033
FEATURE [App::DocumentObjectGroupPython] O_element013  label="O_element : 0.745"  # scripted group (container) (typed FeaturePython)
  n = 0.745
FEATURE [App::DocumentObjectGroupPython] Na_element002  label="Na_element : 0.002"  # scripted group (container) (typed FeaturePython)
  n = 0.001
FEATURE [App::DocumentObjectGroupPython] P_element001  label="P_element : 0.001"  # scripted group (container) (typed FeaturePython)
  n = 0.001
FEATURE [App::DocumentObjectGroupPython] S_element003  label="S_element : 0.002"  # scripted group (container) (typed FeaturePython)
  n = 0.002
FEATURE [App::DocumentObjectGroupPython] Cl_element002  label="Cl_element : 0.003"  # scripted group (container) (typed FeaturePython)
  n = 0.003
FEATURE [App::DocumentObjectGroupPython] K_element001  label="K_element : 0.002"  # scripted group (container) (typed FeaturePython)
  n = 0.002
FEATURE [App::DocumentObjectGroupPython] Fe_element001  label="Fe_element : 0.001"  # scripted group (container) (typed FeaturePython)
  n = 0.001
FEATURE [App::DocumentObjectGroupPython] G4_BLOOD_ICRP  # scripted group (container) (typed FeaturePython)
  Dunit = g/cm3
  Dvalue = 1.06
  Group = -> [H_element014,C_element014,N_element009,O_element013,Na_element002,P_element001,S_element003,Cl_element002,K_element001,Fe_element001]
  conduct = 2
  density = 1
  expand = 3
  formula = G4_BLOOD_ICRP
  name = G4_BLOOD_ICRP
  specific = 4
FEATURE [App::DocumentObjectGroupPython] H_element015  label="H_element : 0.064"  # scripted group (container) (typed FeaturePython)
  n = 0.064
FEATURE [App::DocumentObjectGroupPython] C_element015  label="C_element : 0.278"  # scripted group (container) (typed FeaturePython)
  n = 0.278
FEATURE [App::DocumentObjectGroupPython] N_element010  label="N_element : 0.027"  # scripted group (container) (typed FeaturePython)
  n = 0.027
FEATURE [App::DocumentObjectGroupPython] O_element014  label="O_element : 0.410"  # scripted group (container) (typed FeaturePython)
  n = 0.41
FEATURE [App::DocumentObjectGroupPython] Mg_element001  label="Mg_element : 0.002"  # scripted group (container) (typed FeaturePython)
  n = 0.002
FEATURE [App::DocumentObjectGroupPython] P_element002  label="P_element : 0.070"  # scripted group (container) (typed FeaturePython)
  n = 0.07
FEATURE [App::DocumentObjectGroupPython] S_element004  label="S_element : 0.003"  # scripted group (container) (typed FeaturePython)
  n = 0.002
FEATURE [App::DocumentObjectGroupPython] Ca_element003  label="Ca_element : 0.147"  # scripted group (container) (typed FeaturePython)
  n = 0.147
FEATURE [App::DocumentObjectGroupPython] G4_BONE_COMPACT_ICRU  # scripted group (container) (typed FeaturePython)
  Dunit = g/cm3
  Dvalue = 1.85
  Group = -> [H_element015,C_element015,N_element010,O_element014,Mg_element001,P_element002,S_element004,Ca_element003]
  conduct = 2
  density = 1
  expand = 3
  formula = G4_BONE_COMPACT_ICRU
  name = G4_BONE_COMPACT_ICRU
  specific = 4
FEATURE [App::DocumentObjectGroupPython] H_element016  label="H_element : 0.034"  # scripted group (container) (typed FeaturePython)
  n = 0.034
FEATURE [App::DocumentObjectGroupPython] C_element016  label="C_element : 0.155"  # scripted group (container) (typed FeaturePython)
  n = 0.155
FEATURE [App::DocumentObjectGroupPython] N_element011  label="N_element : 0.042"  # scripted group (container) (typed FeaturePython)
  n = 0.042
FEATURE [App::DocumentObjectGroupPython] O_element015  label="O_element : 0.435"  # scripted group (container) (typed FeaturePython)
  n = 0.435
FEATURE [App::DocumentObjectGroupPython] Na_element003  label="Na_element : 0.003"  # scripted group (container) (typed FeaturePython)
  n = 0.001
FEATURE [App::DocumentObjectGroupPython] Mg_element002  label="Mg_element : 0.003"  # scripted group (container) (typed FeaturePython)
  n = 0.002
FEATURE [App::DocumentObjectGroupPython] P_element003  label="P_element : 0.103"  # scripted group (container) (typed FeaturePython)
  n = 0.103
FEATURE [App::DocumentObjectGroupPython] S_element005  label="S_element : 0.004"  # scripted group (container) (typed FeaturePython)
  n = 0.003
FEATURE [App::DocumentObjectGroupPython] Ca_element004  label="Ca_element : 0.225"  # scripted group (container) (typed FeaturePython)
  n = 0.225
FEATURE [App::DocumentObjectGroupPython] G4_BONE_CORTICAL_ICRP  # scripted group (container) (typed FeaturePython)
  Dunit = g/cm3
  Dvalue = 1.92
  Group = -> [H_element016,C_element016,N_element011,O_element015,Na_element003,Mg_element002,P_element003,S_element005,Ca_element004]
  conduct = 2
  density = 1
  expand = 3
  formula = G4_BONE_CORTICAL_ICRP
  name = G4_BONE_CORTICAL_ICRP
  specific = 4
FEATURE [App::DocumentObjectGroupPython] B_element001  label="B_element : 4"  # scripted group (container) (typed FeaturePython)
  n = 4
  ref = B_element
FEATURE [App::DocumentObjectGroupPython] C_element017  label="C_element : 1"  # scripted group (container) (typed FeaturePython)
  n = 1
  ref = C_element
FEATURE [App::DocumentObjectGroupPython] G4_BORON_CARBIDE  # scripted group (container) (typed FeaturePython)
  Dunit = g/cm3
  Dvalue = 2.52
  Group = -> [B_element001,C_element017]
  conduct = 2
  density = 1
  expand = 3
  formula = G4_BORON_CARBIDE
  name = G4_BORON_CARBIDE
  specific = 4
FEATURE [App::DocumentObjectGroupPython] B_element002  label="B_element : 2"  # scripted group (container) (typed FeaturePython)
  n = 2
  ref = B_element
FEATURE [App::DocumentObjectGroupPython] O_element016  label="O_element : 006"  # scripted group (container) (typed FeaturePython)
  n = 3
  ref = O_element
FEATURE [App::DocumentObjectGroupPython] G4_BORON_OXIDE  # scripted group (container) (typed FeaturePython)
  Dunit = g/cm3
  Dvalue = 1.812
  Group = -> [B_element002,O_element016]
  conduct = 2
  density = 1
  expand = 3
  formula = G4_BORON_OXIDE
  name = G4_BORON_OXIDE
  specific = 4
FEATURE [App::DocumentObjectGroupPython] H_element017  label="H_element : 0.107"  # scripted group (container) (typed FeaturePython)
  n = 0.107
FEATURE [App::DocumentObjectGroupPython] C_element018  label="C_element : 0.145"  # scripted group (container) (typed FeaturePython)
  n = 0.145
FEATURE [App::DocumentObjectGroupPython] N_element012  label="N_element : 0.022"  # scripted group (container) (typed FeaturePython)
  n = 0.022
FEATURE [App::DocumentObjectGroupPython] O_element017  label="O_element : 0.712"  # scripted group (container) (typed FeaturePython)
  n = 0.712
FEATURE [App::DocumentObjectGroupPython] Na_element004  label="Na_element : 0.004"  # scripted group (container) (typed FeaturePython)
  n = 0.002
FEATURE [App::DocumentObjectGroupPython] P_element004  label="P_element : 0.004"  # scripted group (container) (typed FeaturePython)
  n = 0.004
FEATURE [App::DocumentObjectGroupPython] S_element006  label="S_element : 0.005"  # scripted group (container) (typed FeaturePython)
  n = 0.002
FEATURE [App::DocumentObjectGroupPython] Cl_element003  label="Cl_element : 0.004"  # scripted group (container) (typed FeaturePython)
  n = 0.003
FEATURE [App::DocumentObjectGroupPython] K_element002  label="K_element : 0.003"  # scripted group (container) (typed FeaturePython)
  n = 0.003
FEATURE [App::DocumentObjectGroupPython] G4_BRAIN_ICRP  # scripted group (container) (typed FeaturePython)
  Dunit = g/cm3
  Dvalue = 1.04
  Group = -> [H_element017,C_element018,N_element012,O_element017,Na_element004,P_element004,S_element006,Cl_element003,K_element002]
  conduct = 2
  density = 1
  expand = 3
  formula = G4_BRAIN_ICRP
  name = G4_BRAIN_ICRP
  specific = 4
FEATURE [App::DocumentObjectGroupPython] C_element019  label="C_element : 4"  # scripted group (container) (typed FeaturePython)
  n = 4
  ref = C_element
FEATURE [App::DocumentObjectGroupPython] H_element018  label="H_element : 010"  # scripted group (container) (typed FeaturePython)
  n = 10
  ref = H_element
FEATURE [App::DocumentObjectGroupPython] G4_BUTANE  # scripted group (container) (typed FeaturePython)
  Dunit = g/cm3
  Dvalue = 0.00249343
  Group = -> [C_element019,H_element018]
  conduct = 2
  density = 1
  expand = 3
  formula = G4_BUTANE
  name = G4_BUTANE
  specific = 4
FEATURE [App::DocumentObjectGroupPython] C_element020  label="C_element : 008"  # scripted group (container) (typed FeaturePython)
  n = 4
  ref = C_element
FEATURE [App::DocumentObjectGroupPython] H_element019  label="H_element : 011"  # scripted group (container) (typed FeaturePython)
  n = 10
  ref = H_element
FEATURE [App::DocumentObjectGroupPython] O_element018  label="O_element : 007"  # scripted group (container) (typed FeaturePython)
  n = 1
  ref = O_element
FEATURE [App::DocumentObjectGroupPython] G4_N_BUTYL_ALCOHOL  label="G4_N-BUTYL_ALCOHOL"  # scripted group (container) (typed FeaturePython)
  Dunit = g/cm3
  Dvalue = 0.8098
  Group = -> [C_element020,H_element019,O_element018]
  conduct = 2
  density = 1
  expand = 3
  formula = G4_N-BUTYL_ALCOHOL
  name = G4_N-BUTYL_ALCOHOL
  specific = 4
FEATURE [App::DocumentObjectGroupPython] H_element020  label="H_element : 0.025"  # scripted group (container) (typed FeaturePython)
  n = 0.02468
FEATURE [App::DocumentObjectGroupPython] C_element021  label="C_element : 0.502"  # scripted group (container) (typed FeaturePython)
  n = 0.501611
FEATURE [App::DocumentObjectGroupPython] O_element019  label="O_element : 0.005"  # scripted group (container) (typed FeaturePython)
  n = 0.004527
FEATURE [App::DocumentObjectGroupPython] F_element004  label="F_element : 0.465"  # scripted group (container) (typed FeaturePython)
  n = 0.465209
FEATURE [App::DocumentObjectGroupPython] Si_element001  label="Si_element : 0.004"  # scripted group (container) (typed FeaturePython)
  n = 0.003973
FEATURE [App::DocumentObjectGroupPython] G4_C_552  label="G4_C-552"  # scripted group (container) (typed FeaturePython)
  Dunit = g/cm3
  Dvalue = 1.76
  Group = -> [H_element020,C_element021,O_element019,F_element004,Si_element001]
  conduct = 2
  density = 1
  expand = 3
  formula = G4_C-552
  name = G4_C-552
  specific = 4
FEATURE [App::DocumentObjectGroupPython] Cd_element001  label="Cd_element : 1"  # scripted group (container) (typed FeaturePython)
  n = 1
  ref = Cd_element
FEATURE [App::DocumentObjectGroupPython] Te_element001  label="Te_element : 1"  # scripted group (container) (typed FeaturePython)
  n = 1
  ref = Te_element
FEATURE [App::DocumentObjectGroupPython] G4_CADMIUM_TELLURIDE  # scripted group (container) (typed FeaturePython)
  Dunit = g/cm3
  Dvalue = 6.2
  Group = -> [Cd_element001,Te_element001]
  conduct = 2
  density = 1
  expand = 3
  formula = G4_CADMIUM_TELLURIDE
  name = G4_CADMIUM_TELLURIDE
  specific = 4
FEATURE [App::DocumentObjectGroupPython] Cd_element002  label="Cd_element : 002"  # scripted group (container) (typed FeaturePython)
  n = 1
  ref = Cd_element
FEATURE [App::DocumentObjectGroupPython] W_element001  label="W_element : 1"  # scripted group (container) (typed FeaturePython)
  n = 1
  ref = W_element
FEATURE [App::DocumentObjectGroupPython] O_element020  label="O_element : 008"  # scripted group (container) (typed FeaturePython)
  n = 4
  ref = O_element
FEATURE [App::DocumentObjectGroupPython] G4_CADMIUM_TUNGSTATE  # scripted group (container) (typed FeaturePython)
  Dunit = g/cm3
  Dvalue = 7.9
  Group = -> [Cd_element002,W_element001,O_element020]
  conduct = 2
  density = 1
  expand = 3
  formula = G4_CADMIUM_TUNGSTATE
  name = G4_CADMIUM_TUNGSTATE
  specific = 4
FEATURE [App::DocumentObjectGroupPython] Ca_element005  label="Ca_element : 1"  # scripted group (container) (typed FeaturePython)
  n = 1
  ref = Ca_element
FEATURE [App::DocumentObjectGroupPython] C_element022  label="C_element : 009"  # scripted group (container) (typed FeaturePython)
  n = 1
  ref = C_element
FEATURE [App::DocumentObjectGroupPython] O_element021  label="O_element : 009"  # scripted group (container) (typed FeaturePython)
  n = 3
  ref = O_element
FEATURE [App::DocumentObjectGroupPython] G4_CALCIUM_CARBONATE  # scripted group (container) (typed FeaturePython)
  Dunit = g/cm3
  Dvalue = 2.8
  Group = -> [Ca_element005,C_element022,O_element021]
  conduct = 2
  density = 1
  expand = 3
  formula = G4_CALCIUM_CARBONATE
  name = G4_CALCIUM_CARBONATE
  specific = 4
FEATURE [App::DocumentObjectGroupPython] Ca_element006  label="Ca_element : 002"  # scripted group (container) (typed FeaturePython)
  n = 1
  ref = Ca_element
FEATURE [App::DocumentObjectGroupPython] F_element005  label="F_element : 003"  # scripted group (container) (typed FeaturePython)
  n = 2
  ref = F_element
FEATURE [App::DocumentObjectGroupPython] G4_CALCIUM_FLUORIDE  # scripted group (container) (typed FeaturePython)
  Dunit = g/cm3
  Dvalue = 3.18
  Group = -> [Ca_element006,F_element005]
  conduct = 2
  density = 1
  expand = 3
  formula = G4_CALCIUM_FLUORIDE
  name = G4_CALCIUM_FLUORIDE
  specific = 4
FEATURE [App::DocumentObjectGroupPython] Ca_element007  label="Ca_element : 003"  # scripted group (container) (typed FeaturePython)
  n = 1
  ref = Ca_element
FEATURE [App::DocumentObjectGroupPython] O_element022  label="O_element : 010"  # scripted group (container) (typed FeaturePython)
  n = 1
  ref = O_element
FEATURE [App::DocumentObjectGroupPython] G4_CALCIUM_OXIDE  # scripted group (container) (typed FeaturePython)
  Dunit = g/cm3
  Dvalue = 3.3
  Group = -> [Ca_element007,O_element022]
  conduct = 2
  density = 1
  expand = 3
  formula = G4_CALCIUM_OXIDE
  name = G4_CALCIUM_OXIDE
  specific = 4
FEATURE [App::DocumentObjectGroupPython] Ca_element008  label="Ca_element : 004"  # scripted group (container) (typed FeaturePython)
  n = 1
  ref = Ca_element
FEATURE [App::DocumentObjectGroupPython] S_element007  label="S_element : 002"  # scripted group (container) (typed FeaturePython)
  n = 1
  ref = S_element
FEATURE [App::DocumentObjectGroupPython] O_element023  label="O_element : 011"  # scripted group (container) (typed FeaturePython)
  n = 4
  ref = O_element
FEATURE [App::DocumentObjectGroupPython] G4_CALCIUM_SULFATE  # scripted group (container) (typed FeaturePython)
  Dunit = g/cm3
  Dvalue = 2.96
  Group = -> [Ca_element008,S_element007,O_element023]
  conduct = 2
  density = 1
  expand = 3
  formula = G4_CALCIUM_SULFATE
  name = G4_CALCIUM_SULFATE
  specific = 4
FEATURE [App::DocumentObjectGroupPython] Ca_element009  label="Ca_element : 005"  # scripted group (container) (typed FeaturePython)
  n = 1
  ref = Ca_element
FEATURE [App::DocumentObjectGroupPython] W_element002  label="W_element : 002"  # scripted group (container) (typed FeaturePython)
  n = 1
  ref = W_element
FEATURE [App::DocumentObjectGroupPython] O_element024  label="O_element : 012"  # scripted group (container) (typed FeaturePython)
  n = 4
  ref = O_element
FEATURE [App::DocumentObjectGroupPython] G4_CALCIUM_TUNGSTATE  # scripted group (container) (typed FeaturePython)
  Dunit = g/cm3
  Dvalue = 6.062
  Group = -> [Ca_element009,W_element002,O_element024]
  conduct = 2
  density = 1
  expand = 3
  formula = G4_CALCIUM_TUNGSTATE
  name = G4_CALCIUM_TUNGSTATE
  specific = 4
FEATURE [App::DocumentObjectGroupPython] C_element023  label="C_element : 010"  # scripted group (container) (typed FeaturePython)
  n = 1
  ref = C_element
FEATURE [App::DocumentObjectGroupPython] O_element025  label="O_element : 013"  # scripted group (container) (typed FeaturePython)
  n = 2
  ref = O_element
FEATURE [App::DocumentObjectGroupPython] G4_CARBON_DIOXIDE  # scripted group (container) (typed FeaturePython)
  Dunit = g/cm3
  Dvalue = 0.00184212
  Group = -> [C_element023,O_element025]
  conduct = 2
  density = 1
  expand = 3
  formula = G4_CARBON_DIOXIDE
  name = G4_CARBON_DIOXIDE
  specific = 4
FEATURE [App::DocumentObjectGroupPython] C_element024  label="C_element : 011"  # scripted group (container) (typed FeaturePython)
  n = 1
  ref = C_element
FEATURE [App::DocumentObjectGroupPython] Cl_element004  label="Cl_element : 4"  # scripted group (container) (typed FeaturePython)
  n = 4
  ref = Cl_element
FEATURE [App::DocumentObjectGroupPython] G4_CARBON_TETRACHLORIDE  # scripted group (container) (typed FeaturePython)
  Dunit = g/cm3
  Dvalue = 1.594
  Group = -> [C_element024,Cl_element004]
  conduct = 2
  density = 1
  expand = 3
  formula = G4_CARBON_TETRACHLORIDE
  name = G4_CARBON_TETRACHLORIDE
  specific = 4
FEATURE [App::DocumentObjectGroupPython] C_element025  label="C_element : 012"  # scripted group (container) (typed FeaturePython)
  n = 6
  ref = C_element
FEATURE [App::DocumentObjectGroupPython] H_element021  label="H_element : 012"  # scripted group (container) (typed FeaturePython)
  n = 10
  ref = H_element
FEATURE [App::DocumentObjectGroupPython] O_element026  label="O_element : 5"  # scripted group (container) (typed FeaturePython)
  n = 5
  ref = O_element
FEATURE [App::DocumentObjectGroupPython] G4_CELLULOSE_CELLOPHANE  # scripted group (container) (typed FeaturePython)
  Dunit = g/cm3
  Dvalue = 1.42
  Group = -> [C_element025,H_element021,O_element026]
  conduct = 2
  density = 1
  expand = 3
  formula = G4_CELLULOSE_CELLOPHANE
  name = G4_CELLULOSE_CELLOPHANE
  specific = 4
FEATURE [App::DocumentObjectGroupPython] H_element022  label="H_element : 0.067"  # scripted group (container) (typed FeaturePython)
  n = 0.067125
FEATURE [App::DocumentObjectGroupPython] C_element026  label="C_element : 0.545"  # scripted group (container) (typed FeaturePython)
  n = 0.545403
FEATURE [App::DocumentObjectGroupPython] O_element027  label="O_element : 0.387"  # scripted group (container) (typed FeaturePython)
  n = 0.387472
FEATURE [App::DocumentObjectGroupPython] G4_CELLULOSE_BUTYRATE  # scripted group (container) (typed FeaturePython)
  Dunit = g/cm3
  Dvalue = 1.2
  Group = -> [H_element022,C_element026,O_element027]
  conduct = 2
  density = 1
  expand = 3
  formula = G4_CELLULOSE_BUTYRATE
  name = G4_CELLULOSE_BUTYRATE
  specific = 4
FEATURE [App::DocumentObjectGroupPython] H_element023  label="H_element : 0.029"  # scripted group (container) (typed FeaturePython)
  n = 0.029216
FEATURE [App::DocumentObjectGroupPython] C_element027  label="C_element : 0.271"  # scripted group (container) (typed FeaturePython)
  n = 0.271296
FEATURE [App::DocumentObjectGroupPython] N_element013  label="N_element : 0.121"  # scripted group (container) (typed FeaturePython)
  n = 0.121276
FEATURE [App::DocumentObjectGroupPython] O_element028  label="O_element : 0.578"  # scripted group (container) (typed FeaturePython)
  n = 0.578212
FEATURE [App::DocumentObjectGroupPython] G4_CELLULOSE_NITRATE  # scripted group (container) (typed FeaturePython)
  Dunit = g/cm3
  Dvalue = 1.49
  Group = -> [H_element023,C_element027,N_element013,O_element028]
  conduct = 2
  density = 1
  expand = 3
  formula = G4_CELLULOSE_NITRATE
  name = G4_CELLULOSE_NITRATE
  specific = 4
FEATURE [App::DocumentObjectGroupPython] H_element024  label="H_element : 0.108"  # scripted group (container) (typed FeaturePython)
  n = 0.107596
FEATURE [App::DocumentObjectGroupPython] N_element014  label="N_element : 0.001"  # scripted group (container) (typed FeaturePython)
  n = 0.0008
FEATURE [App::DocumentObjectGroupPython] O_element029  label="O_element : 0.875"  # scripted group (container) (typed FeaturePython)
  n = 0.874976
FEATURE [App::DocumentObjectGroupPython] S_element008  label="S_element : 0.015"  # scripted group (container) (typed FeaturePython)
  n = 0.014627
FEATURE [App::DocumentObjectGroupPython] Ce_element001  label="Ce_element : 0.002"  # scripted group (container) (typed FeaturePython)
  n = 0.002001
FEATURE [App::DocumentObjectGroupPython] G4_CERIC_SULFATE  # scripted group (container) (typed FeaturePython)
  Dunit = g/cm3
  Dvalue = 1.03
  Group = -> [H_element024,N_element014,O_element029,S_element008,Ce_element001]
  conduct = 2
  density = 1
  expand = 3
  formula = G4_CERIC_SULFATE
  name = G4_CERIC_SULFATE
  specific = 4
FEATURE [App::DocumentObjectGroupPython] Cs_element001  label="Cs_element : 1"  # scripted group (container) (typed FeaturePython)
  n = 1
  ref = Cs_element
FEATURE [App::DocumentObjectGroupPython] F_element006  label="F_element : 1"  # scripted group (container) (typed FeaturePython)
  n = 1
  ref = F_element
FEATURE [App::DocumentObjectGroupPython] G4_CESIUM_FLUORIDE  # scripted group (container) (typed FeaturePython)
  Dunit = g/cm3
  Dvalue = 4.115
  Group = -> [Cs_element001,F_element006]
  conduct = 2
  density = 1
  expand = 3
  formula = G4_CESIUM_FLUORIDE
  name = G4_CESIUM_FLUORIDE
  specific = 4
FEATURE [App::DocumentObjectGroupPython] Cs_element002  label="Cs_element : 002"  # scripted group (container) (typed FeaturePython)
  n = 1
  ref = Cs_element
FEATURE [App::DocumentObjectGroupPython] I_element001  label="I_element : 1"  # scripted group (container) (typed FeaturePython)
  n = 1
  ref = I_element
FEATURE [App::DocumentObjectGroupPython] G4_CESIUM_IODIDE  # scripted group (container) (typed FeaturePython)
  Dunit = g/cm3
  Dvalue = 4.51
  Group = -> [Cs_element002,I_element001]
  conduct = 2
  density = 1
  expand = 3
  formula = G4_CESIUM_IODIDE
  name = G4_CESIUM_IODIDE
  specific = 4
FEATURE [App::DocumentObjectGroupPython] C_element028  label="C_element : 013"  # scripted group (container) (typed FeaturePython)
  n = 6
  ref = C_element
FEATURE [App::DocumentObjectGroupPython] H_element025  label="H_element : 013"  # scripted group (container) (typed FeaturePython)
  n = 5
  ref = H_element
FEATURE [App::DocumentObjectGroupPython] Cl_element005  label="Cl_element : 1"  # scripted group (container) (typed FeaturePython)
  n = 1
  ref = Cl_element
FEATURE [App::DocumentObjectGroupPython] G4_CHLOROBENZENE  # scripted group (container) (typed FeaturePython)
  Dunit = g/cm3
  Dvalue = 1.1058
  Group = -> [C_element028,H_element025,Cl_element005]
  conduct = 2
  density = 1
  expand = 3
  formula = G4_CHLOROBENZENE
  name = G4_CHLOROBENZENE
  specific = 4
FEATURE [App::DocumentObjectGroupPython] C_element029  label="C_element : 014"  # scripted group (container) (typed FeaturePython)
  n = 1
  ref = C_element
FEATURE [App::DocumentObjectGroupPython] H_element026  label="H_element : 1"  # scripted group (container) (typed FeaturePython)
  n = 1
  ref = H_element
FEATURE [App::DocumentObjectGroupPython] Cl_element006  label="Cl_element : 3"  # scripted group (container) (typed FeaturePython)
  n = 3
  ref = Cl_element
FEATURE [App::DocumentObjectGroupPython] G4_CHLOROFORM  # scripted group (container) (typed FeaturePython)
  Dunit = g/cm3
  Dvalue = 1.4832
  Group = -> [C_element029,H_element026,Cl_element006]
  conduct = 2
  density = 1
  expand = 3
  formula = G4_CHLOROFORM
  name = G4_CHLOROFORM
  specific = 4
FEATURE [App::DocumentObjectGroupPython] H_element027  label="H_element : 0.010"  # scripted group (container) (typed FeaturePython)
  n = 0.01
FEATURE [App::DocumentObjectGroupPython] C_element030  label="C_element : 0.001"  # scripted group (container) (typed FeaturePython)
  n = 0.001
FEATURE [App::DocumentObjectGroupPython] O_element030  label="O_element : 0.529"  # scripted group (container) (typed FeaturePython)
  n = 0.529107
FEATURE [App::DocumentObjectGroupPython] Na_element005  label="Na_element : 0.016"  # scripted group (container) (typed FeaturePython)
  n = 0.016
FEATURE [App::DocumentObjectGroupPython] Mg_element003  label="Mg_element : 0.004"  # scripted group (container) (typed FeaturePython)
  n = 0.002
FEATURE [App::DocumentObjectGroupPython] Al_element002  label="Al_element : 0.034"  # scripted group (container) (typed FeaturePython)
  n = 0.033872
FEATURE [App::DocumentObjectGroupPython] Si_element002  label="Si_element : 0.337"  # scripted group (container) (typed FeaturePython)
  n = 0.337021
FEATURE [App::DocumentObjectGroupPython] K_element003  label="K_element : 0.013"  # scripted group (container) (typed FeaturePython)
  n = 0.013
FEATURE [App::DocumentObjectGroupPython] Ca_element010  label="Ca_element : 0.044"  # scripted group (container) (typed FeaturePython)
  n = 0.044
FEATURE [App::DocumentObjectGroupPython] Fe_element002  label="Fe_element : 0.014"  # scripted group (container) (typed FeaturePython)
  n = 0.014
FEATURE [App::DocumentObjectGroupPython] G4_CONCRETE  # scripted group (container) (typed FeaturePython)
  Dunit = g/cm3
  Dvalue = 2.3
  Group = -> [H_element027,C_element030,O_element030,Na_element005,Mg_element003,Al_element002,Si_element002,K_element003,Ca_element010,Fe_element002]
  conduct = 2
  density = 1
  expand = 3
  formula = G4_CONCRETE
  name = G4_CONCRETE
  specific = 4
FEATURE [App::DocumentObjectGroupPython] C_element031  label="C_element : 015"  # scripted group (container) (typed FeaturePython)
  n = 6
  ref = C_element
FEATURE [App::DocumentObjectGroupPython] H_element028  label="H_element : 12"  # scripted group (container) (typed FeaturePython)
  n = 12
  ref = H_element
FEATURE [App::DocumentObjectGroupPython] G4_CYCLOHEXANE  # scripted group (container) (typed FeaturePython)
  Dunit = g/cm3
  Dvalue = 0.779
  Group = -> [C_element031,H_element028]
  conduct = 2
  density = 1
  expand = 3
  formula = G4_CYCLOHEXANE
  name = G4_CYCLOHEXANE
  specific = 4
FEATURE [App::DocumentObjectGroupPython] C_element032  label="C_element : 016"  # scripted group (container) (typed FeaturePython)
  n = 6
  ref = C_element
FEATURE [App::DocumentObjectGroupPython] H_element029  label="H_element : 4"  # scripted group (container) (typed FeaturePython)
  n = 4
  ref = H_element
FEATURE [App::DocumentObjectGroupPython] Cl_element007  label="Cl_element : 2"  # scripted group (container) (typed FeaturePython)
  n = 2
  ref = Cl_element
FEATURE [App::DocumentObjectGroupPython] G4_1_2_DICHLOROBENZENE  label="G4_1.2-DICHLOROBENZENE"  # scripted group (container) (typed FeaturePython)
  Dunit = g/cm3
  Dvalue = 1.3048
  Group = -> [C_element032,H_element029,Cl_element007]
  conduct = 2
  density = 1
  expand = 3
  formula = G4_1.2-DICHLOROBENZENE
  name = G4_1.2-DICHLOROBENZENE
  specific = 4
FEATURE [App::DocumentObjectGroupPython] C_element033  label="C_element : 017"  # scripted group (container) (typed FeaturePython)
  n = 4
  ref = C_element
FEATURE [App::DocumentObjectGroupPython] H_element030  label="H_element : 8"  # scripted group (container) (typed FeaturePython)
  n = 8
  ref = H_element
FEATURE [App::DocumentObjectGroupPython] O_element031  label="O_element : 014"  # scripted group (container) (typed FeaturePython)
  n = 1
  ref = O_element
FEATURE [App::DocumentObjectGroupPython] Cl_element008  label="Cl_element : 005"  # scripted group (container) (typed FeaturePython)
  n = 2
  ref = Cl_element
FEATURE [App::DocumentObjectGroupPython] G4_DICHLORODIETHYL_ETHER  # scripted group (container) (typed FeaturePython)
  Dunit = g/cm3
  Dvalue = 1.2199
  Group = -> [C_element033,H_element030,O_element031,Cl_element008]
  conduct = 2
  density = 1
  expand = 3
  formula = G4_DICHLORODIETHYL_ETHER
  name = G4_DICHLORODIETHYL_ETHER
  specific = 4
FEATURE [App::DocumentObjectGroupPython] C_element034  label="C_element : 018"  # scripted group (container) (typed FeaturePython)
  n = 2
  ref = C_element
FEATURE [App::DocumentObjectGroupPython] H_element031  label="H_element : 014"  # scripted group (container) (typed FeaturePython)
  n = 4
  ref = H_element
FEATURE [App::DocumentObjectGroupPython] Cl_element009  label="Cl_element : 006"  # scripted group (container) (typed FeaturePython)
  n = 2
  ref = Cl_element
FEATURE [App::DocumentObjectGroupPython] G4_1_2_DICHLOROETHANE  label="G4_1.2-DICHLOROETHANE"  # scripted group (container) (typed FeaturePython)
  Dunit = g/cm3
  Dvalue = 1.2351
  Group = -> [C_element034,H_element031,Cl_element009]
  conduct = 2
  density = 1
  expand = 3
  formula = G4_1.2-DICHLOROETHANE
  name = G4_1.2-DICHLOROETHANE
  specific = 4
FEATURE [App::DocumentObjectGroupPython] C_element035  label="C_element : 019"  # scripted group (container) (typed FeaturePython)
  n = 4
  ref = C_element
FEATURE [App::DocumentObjectGroupPython] H_element032  label="H_element : 015"  # scripted group (container) (typed FeaturePython)
  n = 10
  ref = H_element
FEATURE [App::DocumentObjectGroupPython] O_element032  label="O_element : 015"  # scripted group (container) (typed FeaturePython)
  n = 1
  ref = O_element
FEATURE [App::DocumentObjectGroupPython] G4_DIETHYL_ETHER  # scripted group (container) (typed FeaturePython)
  Dunit = g/cm3
  Dvalue = 0.71378
  Group = -> [C_element035,H_element032,O_element032]
  conduct = 2
  density = 1
  expand = 3
  formula = G4_DIETHYL_ETHER
  name = G4_DIETHYL_ETHER
  specific = 4
FEATURE [App::DocumentObjectGroupPython] C_element036  label="C_element : 020"  # scripted group (container) (typed FeaturePython)
  n = 3
  ref = C_element
FEATURE [App::DocumentObjectGroupPython] H_element033  label="H_element : 016"  # scripted group (container) (typed FeaturePython)
  n = 7
  ref = H_element
FEATURE [App::DocumentObjectGroupPython] N_element015  label="N_element : 008"  # scripted group (container) (typed FeaturePython)
  n = 1
  ref = N_element
FEATURE [App::DocumentObjectGroupPython] O_element033  label="O_element : 016"  # scripted group (container) (typed FeaturePython)
  n = 1
  ref = O_element
FEATURE [App::DocumentObjectGroupPython] G4_N_N_DIMETHYL_FORMAMIDE  label="G4_N.N-DIMETHYL_FORMAMIDE"  # scripted group (container) (typed FeaturePython)
  Dunit = g/cm3
  Dvalue = 0.9487
  Group = -> [C_element036,H_element033,N_element015,O_element033]
  conduct = 2
  density = 1
  expand = 3
  formula = G4_N.N-DIMETHYL_FORMAMIDE
  name = G4_N.N-DIMETHYL_FORMAMIDE
  specific = 4
FEATURE [App::DocumentObjectGroupPython] C_element037  label="C_element : 021"  # scripted group (container) (typed FeaturePython)
  n = 2
  ref = C_element
FEATURE [App::DocumentObjectGroupPython] H_element034  label="H_element : 017"  # scripted group (container) (typed FeaturePython)
  n = 6
  ref = H_element
FEATURE [App::DocumentObjectGroupPython] O_element034  label="O_element : 017"  # scripted group (container) (typed FeaturePython)
  n = 1
  ref = O_element
FEATURE [App::DocumentObjectGroupPython] S_element009  label="S_element : 003"  # scripted group (container) (typed FeaturePython)
  n = 1
  ref = S_element
FEATURE [App::DocumentObjectGroupPython] G4_DIMETHYL_SULFOXIDE  # scripted group (container) (typed FeaturePython)
  Dunit = g/cm3
  Dvalue = 1.1014
  Group = -> [C_element037,H_element034,O_element034,S_element009]
  conduct = 2
  density = 1
  expand = 3
  formula = G4_DIMETHYL_SULFOXIDE
  name = G4_DIMETHYL_SULFOXIDE
  specific = 4
FEATURE [App::DocumentObjectGroupPython] C_element038  label="C_element : 022"  # scripted group (container) (typed FeaturePython)
  n = 2
  ref = C_element
FEATURE [App::DocumentObjectGroupPython] H_element035  label="H_element : 018"  # scripted group (container) (typed FeaturePython)
  n = 6
  ref = H_element
FEATURE [App::DocumentObjectGroupPython] G4_ETHANE  # scripted group (container) (typed FeaturePython)
  Dunit = g/cm3
  Dvalue = 0.00125324
  Group = -> [C_element038,H_element035]
  conduct = 2
  density = 1
  expand = 3
  formula = G4_ETHANE
  name = G4_ETHANE
  specific = 4
FEATURE [App::DocumentObjectGroupPython] C_element039  label="C_element : 023"  # scripted group (container) (typed FeaturePython)
  n = 2
  ref = C_element
FEATURE [App::DocumentObjectGroupPython] H_element036  label="H_element : 019"  # scripted group (container) (typed FeaturePython)
  n = 6
  ref = H_element
FEATURE [App::DocumentObjectGroupPython] O_element035  label="O_element : 018"  # scripted group (container) (typed FeaturePython)
  n = 1
  ref = O_element
FEATURE [App::DocumentObjectGroupPython] G4_ETHYL_ALCOHOL  # scripted group (container) (typed FeaturePython)
  Dunit = g/cm3
  Dvalue = 0.7893
  Group = -> [C_element039,H_element036,O_element035]
  conduct = 2
  density = 1
  expand = 3
  formula = G4_ETHYL_ALCOHOL
  name = G4_ETHYL_ALCOHOL
  specific = 4
FEATURE [App::DocumentObjectGroupPython] H_element037  label="H_element : 0.090"  # scripted group (container) (typed FeaturePython)
  n = 0.090027
FEATURE [App::DocumentObjectGroupPython] C_element040  label="C_element : 0.585"  # scripted group (container) (typed FeaturePython)
  n = 0.585182
FEATURE [App::DocumentObjectGroupPython] O_element036  label="O_element : 0.325"  # scripted group (container) (typed FeaturePython)
  n = 0.324791
FEATURE [App::DocumentObjectGroupPython] G4_ETHYL_CELLULOSE  # scripted group (container) (typed FeaturePython)
  Dunit = g/cm3
  Dvalue = 1.13
  Group = -> [H_element037,C_element040,O_element036]
  conduct = 2
  density = 1
  expand = 3
  formula = G4_ETHYL_CELLULOSE
  name = G4_ETHYL_CELLULOSE
  specific = 4
FEATURE [App::DocumentObjectGroupPython] C_element041  label="C_element : 024"  # scripted group (container) (typed FeaturePython)
  n = 2
  ref = C_element
FEATURE [App::DocumentObjectGroupPython] H_element038  label="H_element : 020"  # scripted group (container) (typed FeaturePython)
  n = 4
  ref = H_element
FEATURE [App::DocumentObjectGroupPython] G4_ETHYLENE  # scripted group (container) (typed FeaturePython)
  Dunit = g/cm3
  Dvalue = 0.00117497
  Group = -> [C_element041,H_element038]
  conduct = 2
  density = 1
  expand = 3
  formula = G4_ETHYLENE
  name = G4_ETHYLENE
  specific = 4
FEATURE [App::DocumentObjectGroupPython] H_element039  label="H_element : 0.096"  # scripted group (container) (typed FeaturePython)
  n = 0.096
FEATURE [App::DocumentObjectGroupPython] C_element042  label="C_element : 0.195"  # scripted group (container) (typed FeaturePython)
  n = 0.195
FEATURE [App::DocumentObjectGroupPython] N_element016  label="N_element : 0.057"  # scripted group (container) (typed FeaturePython)
  n = 0.057
FEATURE [App::DocumentObjectGroupPython] O_element037  label="O_element : 0.646"  # scripted group (container) (typed FeaturePython)
  n = 0.646
FEATURE [App::DocumentObjectGroupPython] Na_element006  label="Na_element : 0.017"  # scripted group (container) (typed FeaturePython)
  n = 0.001
FEATURE [App::DocumentObjectGroupPython] P_element005  label="P_element : 0.104"  # scripted group (container) (typed FeaturePython)
  n = 0.001
FEATURE [App::DocumentObjectGroupPython] S_element010  label="S_element : 0.016"  # scripted group (container) (typed FeaturePython)
  n = 0.003
FEATURE [App::DocumentObjectGroupPython] Cl_element010  label="Cl_element : 0.005"  # scripted group (container) (typed FeaturePython)
  n = 0.001
FEATURE [App::DocumentObjectGroupPython] G4_EYE_LENS_ICRP  # scripted group (container) (typed FeaturePython)
  Dunit = g/cm3
  Dvalue = 1.07
  Group = -> [H_element039,C_element042,N_element016,O_element037,Na_element006,P_element005,S_element010,Cl_element010]
  conduct = 2
  density = 1
  expand = 3
  formula = G4_EYE_LENS_ICRP
  name = G4_EYE_LENS_ICRP
  specific = 4
FEATURE [App::DocumentObjectGroupPython] Fe_element003  label="Fe_element : 2"  # scripted group (container) (typed FeaturePython)
  n = 2
  ref = Fe_element
FEATURE [App::DocumentObjectGroupPython] O_element038  label="O_element : 019"  # scripted group (container) (typed FeaturePython)
  n = 3
  ref = O_element
FEATURE [App::DocumentObjectGroupPython] G4_FERRIC_OXIDE  # scripted group (container) (typed FeaturePython)
  Dunit = g/cm3
  Dvalue = 5.2
  Group = -> [Fe_element003,O_element038]
  conduct = 2
  density = 1
  expand = 3
  formula = G4_FERRIC_OXIDE
  name = G4_FERRIC_OXIDE
  specific = 4
FEATURE [App::DocumentObjectGroupPython] Fe_element004  label="Fe_element : 1"  # scripted group (container) (typed FeaturePython)
  n = 1
  ref = Fe_element
FEATURE [App::DocumentObjectGroupPython] B_element003  label="B_element : 1"  # scripted group (container) (typed FeaturePython)
  n = 1
  ref = B_element
FEATURE [App::DocumentObjectGroupPython] G4_FERROBORIDE  # scripted group (container) (typed FeaturePython)
  Dunit = g/cm3
  Dvalue = 7.15
  Group = -> [Fe_element004,B_element003]
  conduct = 2
  density = 1
  expand = 3
  formula = G4_FERROBORIDE
  name = G4_FERROBORIDE
  specific = 4
FEATURE [App::DocumentObjectGroupPython] Fe_element005  label="Fe_element : 003"  # scripted group (container) (typed FeaturePython)
  n = 1
  ref = Fe_element
FEATURE [App::DocumentObjectGroupPython] O_element039  label="O_element : 020"  # scripted group (container) (typed FeaturePython)
  n = 1
  ref = O_element
FEATURE [App::DocumentObjectGroupPython] G4_FERROUS_OXIDE  # scripted group (container) (typed FeaturePython)
  Dunit = g/cm3
  Dvalue = 5.7
  Group = -> [Fe_element005,O_element039]
  conduct = 2
  density = 1
  expand = 3
  formula = G4_FERROUS_OXIDE
  name = G4_FERROUS_OXIDE
  specific = 4
FEATURE [App::DocumentObjectGroupPython] H_element040  label="H_element : 0.115"  # scripted group (container) (typed FeaturePython)
  n = 0.108259
FEATURE [App::DocumentObjectGroupPython] N_element017  label="N_element : 0.000"  # scripted group (container) (typed FeaturePython)
  n = 2.7e-05
FEATURE [App::DocumentObjectGroupPython] O_element040  label="O_element : 0.879"  # scripted group (container) (typed FeaturePython)
  n = 0.878636
FEATURE [App::DocumentObjectGroupPython] Na_element007  label="Na_element : 0.000"  # scripted group (container) (typed FeaturePython)
  n = 2.2e-05
FEATURE [App::DocumentObjectGroupPython] S_element011  label="S_element : 0.013"  # scripted group (container) (typed FeaturePython)
  n = 0.012968
FEATURE [App::DocumentObjectGroupPython] Cl_element011  label="Cl_element : 0.000"  # scripted group (container) (typed FeaturePython)
  n = 3.4e-05
FEATURE [App::DocumentObjectGroupPython] Fe_element006  label="Fe_element : 0.000"  # scripted group (container) (typed FeaturePython)
  n = 5.4e-05
FEATURE [App::DocumentObjectGroupPython] G4_FERROUS_SULFATE  # scripted group (container) (typed FeaturePython)
  Dunit = g/cm3
  Dvalue = 1.024
  Group = -> [H_element040,N_element017,O_element040,Na_element007,S_element011,Cl_element011,Fe_element006]
  conduct = 2
  density = 1
  expand = 3
  formula = G4_FERROUS_SULFATE
  name = G4_FERROUS_SULFATE
  specific = 4
FEATURE [App::DocumentObjectGroupPython] C_element043  label="C_element : 0.099"  # scripted group (container) (typed FeaturePython)
  n = 0.099335
FEATURE [App::DocumentObjectGroupPython] F_element007  label="F_element : 0.314"  # scripted group (container) (typed FeaturePython)
  n = 0.314247
FEATURE [App::DocumentObjectGroupPython] Cl_element012  label="Cl_element : 0.586"  # scripted group (container) (typed FeaturePython)
  n = 0.586418
FEATURE [App::DocumentObjectGroupPython] G4_FREON_12  label="G4_FREON-12"  # scripted group (container) (typed FeaturePython)
  Dunit = g/cm3
  Dvalue = 1.12
  Group = -> [C_element043,F_element007,Cl_element012]
  conduct = 2
  density = 1
  expand = 3
  formula = G4_FREON-12
  name = G4_FREON-12
  specific = 4
FEATURE [App::DocumentObjectGroupPython] C_element044  label="C_element : 0.057"  # scripted group (container) (typed FeaturePython)
  n = 0.057245
FEATURE [App::DocumentObjectGroupPython] F_element008  label="F_element : 0.181"  # scripted group (container) (typed FeaturePython)
  n = 0.181096
FEATURE [App::DocumentObjectGroupPython] Br_element001  label="Br_element : 0.762"  # scripted group (container) (typed FeaturePython)
  n = 0.761659
FEATURE [App::DocumentObjectGroupPython] G4_FREON_12B2  label="G4_FREON-12B2"  # scripted group (container) (typed FeaturePython)
  Dunit = g/cm3
  Dvalue = 1.8
  Group = -> [C_element044,F_element008,Br_element001]
  conduct = 2
  density = 1
  expand = 3
  formula = G4_FREON-12B2
  name = G4_FREON-12B2
  specific = 4
FEATURE [App::DocumentObjectGroupPython] C_element045  label="C_element : 0.115"  # scripted group (container) (typed FeaturePython)
  n = 0.114983
FEATURE [App::DocumentObjectGroupPython] F_element009  label="F_element : 0.546"  # scripted group (container) (typed FeaturePython)
  n = 0.545621
FEATURE [App::DocumentObjectGroupPython] Cl_element013  label="Cl_element : 0.339"  # scripted group (container) (typed FeaturePython)
  n = 0.339396
FEATURE [App::DocumentObjectGroupPython] G4_FREON_13  label="G4_FREON-13"  # scripted group (container) (typed FeaturePython)
  Dunit = g/cm3
  Dvalue = 0.95
  Group = -> [C_element045,F_element009,Cl_element013]
  conduct = 2
  density = 1
  expand = 3
  formula = G4_FREON-13
  name = G4_FREON-13
  specific = 4
FEATURE [App::DocumentObjectGroupPython] C_element046  label="C_element : 025"  # scripted group (container) (typed FeaturePython)
  n = 1
  ref = C_element
FEATURE [App::DocumentObjectGroupPython] F_element010  label="F_element : 3"  # scripted group (container) (typed FeaturePython)
  n = 3
  ref = F_element
FEATURE [App::DocumentObjectGroupPython] Br_element002  label="Br_element : 1"  # scripted group (container) (typed FeaturePython)
  n = 1
  ref = Br_element
FEATURE [App::DocumentObjectGroupPython] G4_FREON_13B1  label="G4_FREON-13B1"  # scripted group (container) (typed FeaturePython)
  Dunit = g/cm3
  Dvalue = 1.5
  Group = -> [C_element046,F_element010,Br_element002]
  conduct = 2
  density = 1
  expand = 3
  formula = G4_FREON-13B1
  name = G4_FREON-13B1
  specific = 4
FEATURE [App::DocumentObjectGroupPython] C_element047  label="C_element : 0.061"  # scripted group (container) (typed FeaturePython)
  n = 0.061309
FEATURE [App::DocumentObjectGroupPython] F_element011  label="F_element : 0.291"  # scripted group (container) (typed FeaturePython)
  n = 0.290924
FEATURE [App::DocumentObjectGroupPython] I_element002  label="I_element : 0.648"  # scripted group (container) (typed FeaturePython)
  n = 0.647767
FEATURE [App::DocumentObjectGroupPython] G4_FREON_13I1  label="G4_FREON-13I1"  # scripted group (container) (typed FeaturePython)
  Dunit = g/cm3
  Dvalue = 1.8
  Group = -> [C_element047,F_element011,I_element002]
  conduct = 2
  density = 1
  expand = 3
  formula = G4_FREON-13I1
  name = G4_FREON-13I1
  specific = 4
FEATURE [App::DocumentObjectGroupPython] Gd_element001  label="Gd_element : 2"  # scripted group (container) (typed FeaturePython)
  n = 2
  ref = Gd_element
FEATURE [App::DocumentObjectGroupPython] O_element041  label="O_element : 021"  # scripted group (container) (typed FeaturePython)
  n = 2
  ref = O_element
FEATURE [App::DocumentObjectGroupPython] S_element012  label="S_element : 004"  # scripted group (container) (typed FeaturePython)
  n = 1
  ref = S_element
FEATURE [App::DocumentObjectGroupPython] G4_GADOLINIUM_OXYSULFIDE  # scripted group (container) (typed FeaturePython)
  Dunit = g/cm3
  Dvalue = 7.44
  Group = -> [Gd_element001,O_element041,S_element012]
  conduct = 2
  density = 1
  expand = 3
  formula = G4_GADOLINIUM_OXYSULFIDE
  name = G4_GADOLINIUM_OXYSULFIDE
  specific = 4
FEATURE [App::DocumentObjectGroupPython] Ga_element001  label="Ga_element : 1"  # scripted group (container) (typed FeaturePython)
  n = 1
  ref = Ga_element
FEATURE [App::DocumentObjectGroupPython] As_element001  label="As_element : 1"  # scripted group (container) (typed FeaturePython)
  n = 1
  ref = As_element
FEATURE [App::DocumentObjectGroupPython] G4_GALLIUM_ARSENIDE  # scripted group (container) (typed FeaturePython)
  Dunit = g/cm3
  Dvalue = 5.31
  Group = -> [Ga_element001,As_element001]
  conduct = 2
  density = 1
  expand = 3
  formula = G4_GALLIUM_ARSENIDE
  name = G4_GALLIUM_ARSENIDE
  specific = 4
FEATURE [App::DocumentObjectGroupPython] H_element041  label="H_element : 0.081"  # scripted group (container) (typed FeaturePython)
  n = 0.08118
FEATURE [App::DocumentObjectGroupPython] C_element048  label="C_element : 0.416"  # scripted group (container) (typed FeaturePython)
  n = 0.41606
FEATURE [App::DocumentObjectGroupPython] N_element018  label="N_element : 0.111"  # scripted group (container) (typed FeaturePython)
  n = 0.11124
FEATURE [App::DocumentObjectGroupPython] O_element042  label="O_element : 0.381"  # scripted group (container) (typed FeaturePython)
  n = 0.38064
FEATURE [App::DocumentObjectGroupPython] S_element013  label="S_element : 0.011"  # scripted group (container) (typed FeaturePython)
  n = 0.01088
FEATURE [App::DocumentObjectGroupPython] G4_GEL_PHOTO_EMULSION  # scripted group (container) (typed FeaturePython)
  Dunit = g/cm3
  Dvalue = 1.2914
  Group = -> [H_element041,C_element048,N_element018,O_element042,S_element013]
  conduct = 2
  density = 1
  expand = 3
  formula = G4_GEL_PHOTO_EMULSION
  name = G4_GEL_PHOTO_EMULSION
  specific = 4
FEATURE [App::DocumentObjectGroupPython] B_element004  label="B_element : 0.040"  # scripted group (container) (typed FeaturePython)
  n = 0.0400639
FEATURE [App::DocumentObjectGroupPython] O_element043  label="O_element : 0.540"  # scripted group (container) (typed FeaturePython)
  n = 0.539561
FEATURE [App::DocumentObjectGroupPython] Na_element008  label="Na_element : 0.028"  # scripted group (container) (typed FeaturePython)
  n = 0.0281909
FEATURE [App::DocumentObjectGroupPython] Al_element003  label="Al_element : 0.012"  # scripted group (container) (typed FeaturePython)
  n = 0.011644
FEATURE [App::DocumentObjectGroupPython] Si_element003  label="Si_element : 0.377"  # scripted group (container) (typed FeaturePython)
  n = 0.377219
FEATURE [App::DocumentObjectGroupPython] K_element004  label="K_element : 0.014"  # scripted group (container) (typed FeaturePython)
  n = 0.00332099
FEATURE [App::DocumentObjectGroupPython] G4_Pyrex_Glass  # scripted group (container) (typed FeaturePython)
  Dunit = g/cm3
  Dvalue = 2.23
  Group = -> [B_element004,O_element043,Na_element008,Al_element003,Si_element003,K_element004]
  conduct = 2
  density = 1
  expand = 3
  formula = G4_Pyrex_Glass
  name = G4_Pyrex_Glass
  specific = 4
FEATURE [App::DocumentObjectGroupPython] O_element044  label="O_element : 0.156"  # scripted group (container) (typed FeaturePython)
  n = 0.156453
FEATURE [App::DocumentObjectGroupPython] Si_element004  label="Si_element : 0.081"  # scripted group (container) (typed FeaturePython)
  n = 0.080866
FEATURE [App::DocumentObjectGroupPython] Ti_element001  label="Ti_element : 0.008"  # scripted group (container) (typed FeaturePython)
  n = 0.008092
FEATURE [App::DocumentObjectGroupPython] As_element002  label="As_element : 0.003"  # scripted group (container) (typed FeaturePython)
  n = 0.002651
FEATURE [App::DocumentObjectGroupPython] Pb_element001  label="Pb_element : 0.752"  # scripted group (container) (typed FeaturePython)
  n = 0.751938
FEATURE [App::DocumentObjectGroupPython] G4_GLASS_LEAD  # scripted group (container) (typed FeaturePython)
  Dunit = g/cm3
  Dvalue = 6.22
  Group = -> [O_element044,Si_element004,Ti_element001,As_element002,Pb_element001]
  conduct = 2
  density = 1
  expand = 3
  formula = G4_GLASS_LEAD
  name = G4_GLASS_LEAD
  specific = 4
FEATURE [App::DocumentObjectGroupPython] O_element045  label="O_element : 0.460"  # scripted group (container) (typed FeaturePython)
  n = 0.4598
FEATURE [App::DocumentObjectGroupPython] Na_element009  label="Na_element : 0.096"  # scripted group (container) (typed FeaturePython)
  n = 0.0964411
FEATURE [App::DocumentObjectGroupPython] Si_element005  label="Si_element : 0.378"  # scripted group (container) (typed FeaturePython)
  n = 0.336553
FEATURE [App::DocumentObjectGroupPython] Ca_element011  label="Ca_element : 0.107"  # scripted group (container) (typed FeaturePython)
  n = 0.107205
FEATURE [App::DocumentObjectGroupPython] G4_GLASS_PLATE  # scripted group (container) (typed FeaturePython)
  Dunit = g/cm3
  Dvalue = 2.4
  Group = -> [O_element045,Na_element009,Si_element005,Ca_element011]
  conduct = 2
  density = 1
  expand = 3
  formula = G4_GLASS_PLATE
  name = G4_GLASS_PLATE
  specific = 4
FEATURE [App::DocumentObjectGroupPython] C_element049  label="C_element : 026"  # scripted group (container) (typed FeaturePython)
  n = 5
  ref = C_element
FEATURE [App::DocumentObjectGroupPython] H_element042  label="H_element : 021"  # scripted group (container) (typed FeaturePython)
  n = 10
  ref = H_element
FEATURE [App::DocumentObjectGroupPython] N_element019  label="N_element : 2"  # scripted group (container) (typed FeaturePython)
  n = 2
  ref = N_element
FEATURE [App::DocumentObjectGroupPython] O_element046  label="O_element : 022"  # scripted group (container) (typed FeaturePython)
  n = 3
  ref = O_element
FEATURE [App::DocumentObjectGroupPython] G4_GLUTAMINE  # scripted group (container) (typed FeaturePython)
  Dunit = g/cm3
  Dvalue = 1.46
  Group = -> [C_element049,H_element042,N_element019,O_element046]
  conduct = 2
  density = 1
  expand = 3
  formula = G4_GLUTAMINE
  name = G4_GLUTAMINE
  specific = 4
FEATURE [App::DocumentObjectGroupPython] C_element050  label="C_element : 027"  # scripted group (container) (typed FeaturePython)
  n = 3
  ref = C_element
FEATURE [App::DocumentObjectGroupPython] H_element043  label="H_element : 022"  # scripted group (container) (typed FeaturePython)
  n = 8
  ref = H_element
FEATURE [App::DocumentObjectGroupPython] O_element047  label="O_element : 023"  # scripted group (container) (typed FeaturePython)
  n = 3
  ref = O_element
FEATURE [App::DocumentObjectGroupPython] G4_GLYCEROL  # scripted group (container) (typed FeaturePython)
  Dunit = g/cm3
  Dvalue = 1.2613
  Group = -> [C_element050,H_element043,O_element047]
  conduct = 2
  density = 1
  expand = 3
  formula = G4_GLYCEROL
  name = G4_GLYCEROL
  specific = 4
FEATURE [App::DocumentObjectGroupPython] C_element051  label="C_element : 028"  # scripted group (container) (typed FeaturePython)
  n = 5
  ref = C_element
FEATURE [App::DocumentObjectGroupPython] H_element044  label="H_element : 023"  # scripted group (container) (typed FeaturePython)
  n = 5
  ref = H_element
FEATURE [App::DocumentObjectGroupPython] N_element020  label="N_element : 009"  # scripted group (container) (typed FeaturePython)
  n = 5
  ref = N_element
FEATURE [App::DocumentObjectGroupPython] O_element048  label="O_element : 024"  # scripted group (container) (typed FeaturePython)
  n = 1
  ref = O_element
FEATURE [App::DocumentObjectGroupPython] G4_GUANINE  # scripted group (container) (typed FeaturePython)
  Dunit = g/cm3
  Dvalue = 2.2
  Group = -> [C_element051,H_element044,N_element020,O_element048]
  conduct = 2
  density = 1
  expand = 3
  formula = G4_GUANINE
  name = G4_GUANINE
  specific = 4
FEATURE [App::DocumentObjectGroupPython] Ca_element012  label="Ca_element : 006"  # scripted group (container) (typed FeaturePython)
  n = 1
  ref = Ca_element
FEATURE [App::DocumentObjectGroupPython] S_element014  label="S_element : 005"  # scripted group (container) (typed FeaturePython)
  n = 1
  ref = S_element
FEATURE [App::DocumentObjectGroupPython] O_element049  label="O_element : 6"  # scripted group (container) (typed FeaturePython)
  n = 6
  ref = O_element
FEATURE [App::DocumentObjectGroupPython] H_element045  label="H_element : 024"  # scripted group (container) (typed FeaturePython)
  n = 4
  ref = H_element
FEATURE [App::DocumentObjectGroupPython] G4_GYPSUM  # scripted group (container) (typed FeaturePython)
  Dunit = g/cm3
  Dvalue = 2.32
  Group = -> [Ca_element012,S_element014,O_element049,H_element045]
  conduct = 2
  density = 1
  expand = 3
  formula = G4_GYPSUM
  name = G4_GYPSUM
  specific = 4
FEATURE [App::DocumentObjectGroupPython] C_element052  label="C_element : 7"  # scripted group (container) (typed FeaturePython)
  n = 7
  ref = C_element
FEATURE [App::DocumentObjectGroupPython] H_element046  label="H_element : 16"  # scripted group (container) (typed FeaturePython)
  n = 16
  ref = H_element
FEATURE [App::DocumentObjectGroupPython] G4_N_HEPTANE  label="G4_N-HEPTANE"  # scripted group (container) (typed FeaturePython)
  Dunit = g/cm3
  Dvalue = 0.68376
  Group = -> [C_element052,H_element046]
  conduct = 2
  density = 1
  expand = 3
  formula = G4_N-HEPTANE
  name = G4_N-HEPTANE
  specific = 4
FEATURE [App::DocumentObjectGroupPython] C_element053  label="C_element : 029"  # scripted group (container) (typed FeaturePython)
  n = 6
  ref = C_element
FEATURE [App::DocumentObjectGroupPython] H_element047  label="H_element : 14"  # scripted group (container) (typed FeaturePython)
  n = 14
  ref = H_element
FEATURE [App::DocumentObjectGroupPython] G4_N_HEXANE  label="G4_N-HEXANE"  # scripted group (container) (typed FeaturePython)
  Dunit = g/cm3
  Dvalue = 0.6603
  Group = -> [C_element053,H_element047]
  conduct = 2
  density = 1
  expand = 3
  formula = G4_N-HEXANE
  name = G4_N-HEXANE
  specific = 4
FEATURE [App::DocumentObjectGroupPython] C_element054  label="C_element : 22"  # scripted group (container) (typed FeaturePython)
  n = 22
  ref = C_element
FEATURE [App::DocumentObjectGroupPython] H_element048  label="H_element : 025"  # scripted group (container) (typed FeaturePython)
  n = 10
  ref = H_element
FEATURE [App::DocumentObjectGroupPython] N_element021  label="N_element : 010"  # scripted group (container) (typed FeaturePython)
  n = 2
  ref = N_element
FEATURE [App::DocumentObjectGroupPython] O_element050  label="O_element : 025"  # scripted group (container) (typed FeaturePython)
  n = 5
  ref = O_element
FEATURE [App::DocumentObjectGroupPython] G4_KAPTON  # scripted group (container) (typed FeaturePython)
  Dunit = g/cm3
  Dvalue = 1.42
  Group = -> [C_element054,H_element048,N_element021,O_element050]
  conduct = 2
  density = 1
  expand = 3
  formula = G4_KAPTON
  name = G4_KAPTON
  specific = 4
FEATURE [App::DocumentObjectGroupPython] La_element001  label="La_element : 1"  # scripted group (container) (typed FeaturePython)
  n = 1
  ref = La_element
FEATURE [App::DocumentObjectGroupPython] Br_element003  label="Br_element : 002"  # scripted group (container) (typed FeaturePython)
  n = 1
  ref = Br_element
FEATURE [App::DocumentObjectGroupPython] O_element051  label="O_element : 026"  # scripted group (container) (typed FeaturePython)
  n = 1
  ref = O_element
FEATURE [App::DocumentObjectGroupPython] G4_LANTHANUM_OXYBROMIDE  # scripted group (container) (typed FeaturePython)
  Dunit = g/cm3
  Dvalue = 6.28
  Group = -> [La_element001,Br_element003,O_element051]
  conduct = 2
  density = 1
  expand = 3
  formula = G4_LANTHANUM_OXYBROMIDE
  name = G4_LANTHANUM_OXYBROMIDE
  specific = 4
FEATURE [App::DocumentObjectGroupPython] La_element002  label="La_element : 2"  # scripted group (container) (typed FeaturePython)
  n = 2
  ref = La_element
FEATURE [App::DocumentObjectGroupPython] O_element052  label="O_element : 027"  # scripted group (container) (typed FeaturePython)
  n = 2
  ref = O_element
FEATURE [App::DocumentObjectGroupPython] S_element015  label="S_element : 006"  # scripted group (container) (typed FeaturePython)
  n = 1
  ref = S_element
FEATURE [App::DocumentObjectGroupPython] G4_LANTHANUM_OXYSULFIDE  # scripted group (container) (typed FeaturePython)
  Dunit = g/cm3
  Dvalue = 5.86
  Group = -> [La_element002,O_element052,S_element015]
  conduct = 2
  density = 1
  expand = 3
  formula = G4_LANTHANUM_OXYSULFIDE
  name = G4_LANTHANUM_OXYSULFIDE
  specific = 4
FEATURE [App::DocumentObjectGroupPython] O_element053  label="O_element : 0.072"  # scripted group (container) (typed FeaturePython)
  n = 0.071682
FEATURE [App::DocumentObjectGroupPython] Pb_element002  label="Pb_element : 0.928"  # scripted group (container) (typed FeaturePython)
  n = 0.928318
FEATURE [App::DocumentObjectGroupPython] G4_LEAD_OXIDE  # scripted group (container) (typed FeaturePython)
  Dunit = g/cm3
  Dvalue = 9.53
  Group = -> [O_element053,Pb_element002]
  conduct = 2
  density = 1
  expand = 3
  formula = G4_LEAD_OXIDE
  name = G4_LEAD_OXIDE
  specific = 4
FEATURE [App::DocumentObjectGroupPython] Li_element001  label="Li_element : 1"  # scripted group (container) (typed FeaturePython)
  n = 1
  ref = Li_element
FEATURE [App::DocumentObjectGroupPython] N_element022  label="N_element : 011"  # scripted group (container) (typed FeaturePython)
  n = 1
  ref = N_element
FEATURE [App::DocumentObjectGroupPython] H_element049  label="H_element : 026"  # scripted group (container) (typed FeaturePython)
  n = 2
  ref = H_element
FEATURE [App::DocumentObjectGroupPython] G4_LITHIUM_AMIDE  # scripted group (container) (typed FeaturePython)
  Dunit = g/cm3
  Dvalue = 1.178
  Group = -> [Li_element001,N_element022,H_element049]
  conduct = 2
  density = 1
  expand = 3
  formula = G4_LITHIUM_AMIDE
  name = G4_LITHIUM_AMIDE
  specific = 4
FEATURE [App::DocumentObjectGroupPython] Li_element002  label="Li_element : 2"  # scripted group (container) (typed FeaturePython)
  n = 2
  ref = Li_element
FEATURE [App::DocumentObjectGroupPython] C_element055  label="C_element : 030"  # scripted group (container) (typed FeaturePython)
  n = 1
  ref = C_element
FEATURE [App::DocumentObjectGroupPython] O_element054  label="O_element : 028"  # scripted group (container) (typed FeaturePython)
  n = 3
  ref = O_element
FEATURE [App::DocumentObjectGroupPython] G4_LITHIUM_CARBONATE  # scripted group (container) (typed FeaturePython)
  Dunit = g/cm3
  Dvalue = 2.11
  Group = -> [Li_element002,C_element055,O_element054]
  conduct = 2
  density = 1
  expand = 3
  formula = G4_LITHIUM_CARBONATE
  name = G4_LITHIUM_CARBONATE
  specific = 4
FEATURE [App::DocumentObjectGroupPython] Li_element003  label="Li_element : 003"  # scripted group (container) (typed FeaturePython)
  n = 1
  ref = Li_element
FEATURE [App::DocumentObjectGroupPython] F_element012  label="F_element : 004"  # scripted group (container) (typed FeaturePython)
  n = 1
  ref = F_element
FEATURE [App::DocumentObjectGroupPython] G4_LITHIUM_FLUORIDE  # scripted group (container) (typed FeaturePython)
  Dunit = g/cm3
  Dvalue = 2.635
  Group = -> [Li_element003,F_element012]
  conduct = 2
  density = 1
  expand = 3
  formula = G4_LITHIUM_FLUORIDE
  name = G4_LITHIUM_FLUORIDE
  specific = 4
FEATURE [App::DocumentObjectGroupPython] Li_element004  label="Li_element : 004"  # scripted group (container) (typed FeaturePython)
  n = 1
  ref = Li_element
FEATURE [App::DocumentObjectGroupPython] H_element050  label="H_element : 027"  # scripted group (container) (typed FeaturePython)
  n = 1
  ref = H_element
FEATURE [App::DocumentObjectGroupPython] G4_LITHIUM_HYDRIDE  # scripted group (container) (typed FeaturePython)
  Dunit = g/cm3
  Dvalue = 0.82
  Group = -> [Li_element004,H_element050]
  conduct = 2
  density = 1
  expand = 3
  formula = G4_LITHIUM_HYDRIDE
  name = G4_LITHIUM_HYDRIDE
  specific = 4
FEATURE [App::DocumentObjectGroupPython] Li_element005  label="Li_element : 005"  # scripted group (container) (typed FeaturePython)
  n = 1
  ref = Li_element
FEATURE [App::DocumentObjectGroupPython] I_element003  label="I_element : 002"  # scripted group (container) (typed FeaturePython)
  n = 1
  ref = I_element
FEATURE [App::DocumentObjectGroupPython] G4_LITHIUM_IODIDE  # scripted group (container) (typed FeaturePython)
  Dunit = g/cm3
  Dvalue = 3.494
  Group = -> [Li_element005,I_element003]
  conduct = 2
  density = 1
  expand = 3
  formula = G4_LITHIUM_IODIDE
  name = G4_LITHIUM_IODIDE
  specific = 4
FEATURE [App::DocumentObjectGroupPython] Li_element006  label="Li_element : 006"  # scripted group (container) (typed FeaturePython)
  n = 2
  ref = Li_element
FEATURE [App::DocumentObjectGroupPython] O_element055  label="O_element : 029"  # scripted group (container) (typed FeaturePython)
  n = 1
  ref = O_element
FEATURE [App::DocumentObjectGroupPython] G4_LITHIUM_OXIDE  # scripted group (container) (typed FeaturePython)
  Dunit = g/cm3
  Dvalue = 2.013
  Group = -> [Li_element006,O_element055]
  conduct = 2
  density = 1
  expand = 3
  formula = G4_LITHIUM_OXIDE
  name = G4_LITHIUM_OXIDE
  specific = 4
FEATURE [App::DocumentObjectGroupPython] Li_element007  label="Li_element : 007"  # scripted group (container) (typed FeaturePython)
  n = 2
  ref = Li_element
FEATURE [App::DocumentObjectGroupPython] B_element005  label="B_element : 005"  # scripted group (container) (typed FeaturePython)
  n = 4
  ref = B_element
FEATURE [App::DocumentObjectGroupPython] O_element056  label="O_element : 7"  # scripted group (container) (typed FeaturePython)
  n = 7
  ref = O_element
FEATURE [App::DocumentObjectGroupPython] G4_LITHIUM_TETRABORATE  # scripted group (container) (typed FeaturePython)
  Dunit = g/cm3
  Dvalue = 2.44
  Group = -> [Li_element007,B_element005,O_element056]
  conduct = 2
  density = 1
  expand = 3
  formula = G4_LITHIUM_TETRABORATE
  name = G4_LITHIUM_TETRABORATE
  specific = 4
FEATURE [App::DocumentObjectGroupPython] H_element051  label="H_element : 0.105"  # scripted group (container) (typed FeaturePython)
  n = 0.105
FEATURE [App::DocumentObjectGroupPython] C_element056  label="C_element : 0.083"  # scripted group (container) (typed FeaturePython)
  n = 0.083
FEATURE [App::DocumentObjectGroupPython] N_element023  label="N_element : 0.023"  # scripted group (container) (typed FeaturePython)
  n = 0.023
FEATURE [App::DocumentObjectGroupPython] O_element057  label="O_element : 0.779"  # scripted group (container) (typed FeaturePython)
  n = 0.779
FEATURE [App::DocumentObjectGroupPython] Na_element010  label="Na_element : 0.097"  # scripted group (container) (typed FeaturePython)
  n = 0.002
FEATURE [App::DocumentObjectGroupPython] P_element006  label="P_element : 0.105"  # scripted group (container) (typed FeaturePython)
  n = 0.001
FEATURE [App::DocumentObjectGroupPython] S_element016  label="S_element : 0.017"  # scripted group (container) (typed FeaturePython)
  n = 0.002
FEATURE [App::DocumentObjectGroupPython] Cl_element014  label="Cl_element : 0.587"  # scripted group (container) (typed FeaturePython)
  n = 0.003
FEATURE [App::DocumentObjectGroupPython] K_element005  label="K_element : 0.015"  # scripted group (container) (typed FeaturePython)
  n = 0.002
FEATURE [App::DocumentObjectGroupPython] G4_LUNG_ICRP  # scripted group (container) (typed FeaturePython)
  Dunit = g/cm3
  Dvalue = 1.04
  Group = -> [H_element051,C_element056,N_element023,O_element057,Na_element010,P_element006,S_element016,Cl_element014,K_element005]
  conduct = 2
  density = 1
  expand = 3
  formula = G4_LUNG_ICRP
  name = G4_LUNG_ICRP
  specific = 4
FEATURE [App::DocumentObjectGroupPython] H_element052  label="H_element : 0.116"  # scripted group (container) (typed FeaturePython)
  n = 0.114318
FEATURE [App::DocumentObjectGroupPython] C_element057  label="C_element : 0.656"  # scripted group (container) (typed FeaturePython)
  n = 0.655824
FEATURE [App::DocumentObjectGroupPython] O_element058  label="O_element : 0.092"  # scripted group (container) (typed FeaturePython)
  n = 0.0921831
FEATURE [App::DocumentObjectGroupPython] Mg_element004  label="Mg_element : 0.135"  # scripted group (container) (typed FeaturePython)
  n = 0.134792
FEATURE [App::DocumentObjectGroupPython] Ca_element013  label="Ca_element : 0.003"  # scripted group (container) (typed FeaturePython)
  n = 0.002883
FEATURE [App::DocumentObjectGroupPython] G4_M3_WAX  # scripted group (container) (typed FeaturePython)
  Dunit = g/cm3
  Dvalue = 1.05
  Group = -> [H_element052,C_element057,O_element058,Mg_element004,Ca_element013]
  conduct = 2
  density = 1
  expand = 3
  formula = G4_M3_WAX
  name = G4_M3_WAX
  specific = 4
FEATURE [App::DocumentObjectGroupPython] Mg_element005  label="Mg_element : 1"  # scripted group (container) (typed FeaturePython)
  n = 1
  ref = Mg_element
FEATURE [App::DocumentObjectGroupPython] C_element058  label="C_element : 031"  # scripted group (container) (typed FeaturePython)
  n = 1
  ref = C_element
FEATURE [App::DocumentObjectGroupPython] O_element059  label="O_element : 030"  # scripted group (container) (typed FeaturePython)
  n = 3
  ref = O_element
FEATURE [App::DocumentObjectGroupPython] G4_MAGNESIUM_CARBONATE  # scripted group (container) (typed FeaturePython)
  Dunit = g/cm3
  Dvalue = 2.958
  Group = -> [Mg_element005,C_element058,O_element059]
  conduct = 2
  density = 1
  expand = 3
  formula = G4_MAGNESIUM_CARBONATE
  name = G4_MAGNESIUM_CARBONATE
  specific = 4
FEATURE [App::DocumentObjectGroupPython] Mg_element006  label="Mg_element : 002"  # scripted group (container) (typed FeaturePython)
  n = 1
  ref = Mg_element
FEATURE [App::DocumentObjectGroupPython] F_element013  label="F_element : 005"  # scripted group (container) (typed FeaturePython)
  n = 2
  ref = F_element
FEATURE [App::DocumentObjectGroupPython] G4_MAGNESIUM_FLUORIDE  # scripted group (container) (typed FeaturePython)
  Dunit = g/cm3
  Dvalue = 3
  Group = -> [Mg_element006,F_element013]
  conduct = 2
  density = 1
  expand = 3
  formula = G4_MAGNESIUM_FLUORIDE
  name = G4_MAGNESIUM_FLUORIDE
  specific = 4
FEATURE [App::DocumentObjectGroupPython] Mg_element007  label="Mg_element : 003"  # scripted group (container) (typed FeaturePython)
  n = 1
  ref = Mg_element
FEATURE [App::DocumentObjectGroupPython] O_element060  label="O_element : 031"  # scripted group (container) (typed FeaturePython)
  n = 1
  ref = O_element
FEATURE [App::DocumentObjectGroupPython] G4_MAGNESIUM_OXIDE  # scripted group (container) (typed FeaturePython)
  Dunit = g/cm3
  Dvalue = 3.58
  Group = -> [Mg_element007,O_element060]
  conduct = 2
  density = 1
  expand = 3
  formula = G4_MAGNESIUM_OXIDE
  name = G4_MAGNESIUM_OXIDE
  specific = 4
FEATURE [App::DocumentObjectGroupPython] Mg_element008  label="Mg_element : 004"  # scripted group (container) (typed FeaturePython)
  n = 1
  ref = Mg_element
FEATURE [App::DocumentObjectGroupPython] B_element006  label="B_element : 006"  # scripted group (container) (typed FeaturePython)
  n = 4
  ref = B_element
FEATURE [App::DocumentObjectGroupPython] O_element061  label="O_element : 032"  # scripted group (container) (typed FeaturePython)
  n = 7
  ref = O_element
FEATURE [App::DocumentObjectGroupPython] G4_MAGNESIUM_TETRABORATE  # scripted group (container) (typed FeaturePython)
  Dunit = g/cm3
  Dvalue = 2.53
  Group = -> [Mg_element008,B_element006,O_element061]
  conduct = 2
  density = 1
  expand = 3
  formula = G4_MAGNESIUM_TETRABORATE
  name = G4_MAGNESIUM_TETRABORATE
  specific = 4
FEATURE [App::DocumentObjectGroupPython] Hg_element001  label="Hg_element : 1"  # scripted group (container) (typed FeaturePython)
  n = 1
  ref = Hg_element
FEATURE [App::DocumentObjectGroupPython] I_element004  label="I_element : 2"  # scripted group (container) (typed FeaturePython)
  n = 2
  ref = I_element
FEATURE [App::DocumentObjectGroupPython] G4_MERCURIC_IODIDE  # scripted group (container) (typed FeaturePython)
  Dunit = g/cm3
  Dvalue = 6.36
  Group = -> [Hg_element001,I_element004]
  conduct = 2
  density = 1
  expand = 3
  formula = G4_MERCURIC_IODIDE
  name = G4_MERCURIC_IODIDE
  specific = 4
FEATURE [App::DocumentObjectGroupPython] C_element059  label="C_element : 032"  # scripted group (container) (typed FeaturePython)
  n = 1
  ref = C_element
FEATURE [App::DocumentObjectGroupPython] H_element053  label="H_element : 028"  # scripted group (container) (typed FeaturePython)
  n = 4
  ref = H_element
FEATURE [App::DocumentObjectGroupPython] G4_METHANE  # scripted group (container) (typed FeaturePython)
  Dunit = g/cm3
  Dvalue = 0.000667151
  Group = -> [C_element059,H_element053]
  conduct = 2
  density = 1
  expand = 3
  formula = G4_METHANE
  name = G4_METHANE
  specific = 4
FEATURE [App::DocumentObjectGroupPython] C_element060  label="C_element : 033"  # scripted group (container) (typed FeaturePython)
  n = 1
  ref = C_element
FEATURE [App::DocumentObjectGroupPython] H_element054  label="H_element : 029"  # scripted group (container) (typed FeaturePython)
  n = 4
  ref = H_element
FEATURE [App::DocumentObjectGroupPython] O_element062  label="O_element : 033"  # scripted group (container) (typed FeaturePython)
  n = 1
  ref = O_element
FEATURE [App::DocumentObjectGroupPython] G4_METHANOL  # scripted group (container) (typed FeaturePython)
  Dunit = g/cm3
  Dvalue = 0.7914
  Group = -> [C_element060,H_element054,O_element062]
  conduct = 2
  density = 1
  expand = 3
  formula = G4_METHANOL
  name = G4_METHANOL
  specific = 4
FEATURE [App::DocumentObjectGroupPython] H_element055  label="H_element : 0.134"  # scripted group (container) (typed FeaturePython)
  n = 0.13404
FEATURE [App::DocumentObjectGroupPython] C_element061  label="C_element : 0.778"  # scripted group (container) (typed FeaturePython)
  n = 0.77796
FEATURE [App::DocumentObjectGroupPython] O_element063  label="O_element : 0.035"  # scripted group (container) (typed FeaturePython)
  n = 0.03502
FEATURE [App::DocumentObjectGroupPython] Mg_element009  label="Mg_element : 0.039"  # scripted group (container) (typed FeaturePython)
  n = 0.038594
FEATURE [App::DocumentObjectGroupPython] Ti_element002  label="Ti_element : 0.014"  # scripted group (container) (typed FeaturePython)
  n = 0.014386
FEATURE [App::DocumentObjectGroupPython] G4_MIX_D_WAX  # scripted group (container) (typed FeaturePython)
  Dunit = g/cm3
  Dvalue = 0.99
  Group = -> [H_element055,C_element061,O_element063,Mg_element009,Ti_element002]
  conduct = 2
  density = 1
  expand = 3
  formula = G4_MIX_D_WAX
  name = G4_MIX_D_WAX
  specific = 4
FEATURE [App::DocumentObjectGroupPython] H_element056  label="H_element : 0.135"  # scripted group (container) (typed FeaturePython)
  n = 0.081192
FEATURE [App::DocumentObjectGroupPython] C_element062  label="C_element : 0.583"  # scripted group (container) (typed FeaturePython)
  n = 0.583442
FEATURE [App::DocumentObjectGroupPython] N_element024  label="N_element : 0.018"  # scripted group (container) (typed FeaturePython)
  n = 0.017798
FEATURE [App::DocumentObjectGroupPython] O_element064  label="O_element : 0.186"  # scripted group (container) (typed FeaturePython)
  n = 0.186381
FEATURE [App::DocumentObjectGroupPython] Mg_element010  label="Mg_element : 0.130"  # scripted group (container) (typed FeaturePython)
  n = 0.130287
FEATURE [App::DocumentObjectGroupPython] Cl_element015  label="Cl_element : 0.588"  # scripted group (container) (typed FeaturePython)
  n = 0.0009
FEATURE [App::DocumentObjectGroupPython] G4_MS20_TISSUE  # scripted group (container) (typed FeaturePython)
  Dunit = g/cm3
  Dvalue = 1
  Group = -> [H_element056,C_element062,N_element024,O_element064,Mg_element010,Cl_element015]
  conduct = 2
  density = 1
  expand = 3
  formula = G4_MS20_TISSUE
  name = G4_MS20_TISSUE
  specific = 4
FEATURE [App::DocumentObjectGroupPython] H_element057  label="H_element : 0.136"  # scripted group (container) (typed FeaturePython)
  n = 0.102
FEATURE [App::DocumentObjectGroupPython] C_element063  label="C_element : 0.143"  # scripted group (container) (typed FeaturePython)
  n = 0.143
FEATURE [App::DocumentObjectGroupPython] N_element025  label="N_element : 0.034"  # scripted group (container) (typed FeaturePython)
  n = 0.034
FEATURE [App::DocumentObjectGroupPython] O_element065  label="O_element : 0.710"  # scripted group (container) (typed FeaturePython)
  n = 0.71
FEATURE [App::DocumentObjectGroupPython] Na_element011  label="Na_element : 0.098"  # scripted group (container) (typed FeaturePython)
  n = 0.001
FEATURE [App::DocumentObjectGroupPython] P_element007  label="P_element : 0.002"  # scripted group (container) (typed FeaturePython)
  n = 0.002
FEATURE [App::DocumentObjectGroupPython] S_element017  label="S_element : 0.018"  # scripted group (container) (typed FeaturePython)
  n = 0.003
FEATURE [App::DocumentObjectGroupPython] Cl_element016  label="Cl_element : 0.589"  # scripted group (container) (typed FeaturePython)
  n = 0.001
FEATURE [App::DocumentObjectGroupPython] K_element006  label="K_element : 0.004"  # scripted group (container) (typed FeaturePython)
  n = 0.004
FEATURE [App::DocumentObjectGroupPython] G4_MUSCLE_SKELETAL_ICRP  # scripted group (container) (typed FeaturePython)
  Dunit = g/cm3
  Dvalue = 1.05
  Group = -> [H_element057,C_element063,N_element025,O_element065,Na_element011,P_element007,S_element017,Cl_element016,K_element006]
  conduct = 2
  density = 1
  expand = 3
  formula = G4_MUSCLE_SKELETAL_ICRP
  name = G4_MUSCLE_SKELETAL_ICRP
  specific = 4
FEATURE [App::DocumentObjectGroupPython] H_element058  label="H_element : 0.137"  # scripted group (container) (typed FeaturePython)
  n = 0.102102
FEATURE [App::DocumentObjectGroupPython] C_element064  label="C_element : 0.123"  # scripted group (container) (typed FeaturePython)
  n = 0.123123
FEATURE [App::DocumentObjectGroupPython] N_element026  label="N_element : 0.756"  # scripted group (container) (typed FeaturePython)
  n = 0.035035
FEATURE [App::DocumentObjectGroupPython] O_element066  label="O_element : 0.730"  # scripted group (container) (typed FeaturePython)
  n = 0.72973
FEATURE [App::DocumentObjectGroupPython] Na_element012  label="Na_element : 0.099"  # scripted group (container) (typed FeaturePython)
  n = 0.001001
FEATURE [App::DocumentObjectGroupPython] P_element008  label="P_element : 0.106"  # scripted group (container) (typed FeaturePython)
  n = 0.002002
FEATURE [App::DocumentObjectGroupPython] S_element018  label="S_element : 0.019"  # scripted group (container) (typed FeaturePython)
  n = 0.004004
FEATURE [App::DocumentObjectGroupPython] K_element007  label="K_element : 0.016"  # scripted group (container) (typed FeaturePython)
  n = 0.003003
FEATURE [App::DocumentObjectGroupPython] G4_MUSCLE_STRIATED_ICRU  # scripted group (container) (typed FeaturePython)
  Dunit = g/cm3
  Dvalue = 1.04
  Group = -> [H_element058,C_element064,N_element026,O_element066,Na_element012,P_element008,S_element018,K_element007]
  conduct = 2
  density = 1
  expand = 3
  formula = G4_MUSCLE_STRIATED_ICRU
  name = G4_MUSCLE_STRIATED_ICRU
  specific = 4
FEATURE [App::DocumentObjectGroupPython] H_element059  label="H_element : 0.098"  # scripted group (container) (typed FeaturePython)
  n = 0.0982341
FEATURE [App::DocumentObjectGroupPython] C_element065  label="C_element : 0.156"  # scripted group (container) (typed FeaturePython)
  n = 0.156214
FEATURE [App::DocumentObjectGroupPython] N_element027  label="N_element : 0.757"  # scripted group (container) (typed FeaturePython)
  n = 0.035451
FEATURE [App::DocumentObjectGroupPython] O_element067  label="O_element : 0.880"  # scripted group (container) (typed FeaturePython)
  n = 0.710101
FEATURE [App::DocumentObjectGroupPython] G4_MUSCLE_WITH_SUCROSE  # scripted group (container) (typed FeaturePython)
  Dunit = g/cm3
  Dvalue = 1.11
  Group = -> [H_element059,C_element065,N_element027,O_element067]
  conduct = 2
  density = 1
  expand = 3
  formula = G4_MUSCLE_WITH_SUCROSE
  name = G4_MUSCLE_WITH_SUCROSE
  specific = 4
FEATURE [App::DocumentObjectGroupPython] H_element060  label="H_element : 0.138"  # scripted group (container) (typed FeaturePython)
  n = 0.101969
FEATURE [App::DocumentObjectGroupPython] C_element066  label="C_element : 0.120"  # scripted group (container) (typed FeaturePython)
  n = 0.120058
FEATURE [App::DocumentObjectGroupPython] N_element028  label="N_element : 0.758"  # scripted group (container) (typed FeaturePython)
  n = 0.035451
FEATURE [App::DocumentObjectGroupPython] O_element068  label="O_element : 0.743"  # scripted group (container) (typed FeaturePython)
  n = 0.742522
FEATURE [App::DocumentObjectGroupPython] G4_MUSCLE_WITHOUT_SUCROSE  # scripted group (container) (typed FeaturePython)
  Dunit = g/cm3
  Dvalue = 1.07
  Group = -> [H_element060,C_element066,N_element028,O_element068]
  conduct = 2
  density = 1
  expand = 3
  formula = G4_MUSCLE_WITHOUT_SUCROSE
  name = G4_MUSCLE_WITHOUT_SUCROSE
  specific = 4
FEATURE [App::DocumentObjectGroupPython] C_element067  label="C_element : 10"  # scripted group (container) (typed FeaturePython)
  n = 10
  ref = C_element
FEATURE [App::DocumentObjectGroupPython] H_element061  label="H_element : 030"  # scripted group (container) (typed FeaturePython)
  n = 8
  ref = H_element
FEATURE [App::DocumentObjectGroupPython] G4_NAPHTHALENE  # scripted group (container) (typed FeaturePython)
  Dunit = g/cm3
  Dvalue = 1.145
  Group = -> [C_element067,H_element061]
  conduct = 2
  density = 1
  expand = 3
  formula = G4_NAPHTHALENE
  name = G4_NAPHTHALENE
  specific = 4
FEATURE [App::DocumentObjectGroupPython] C_element068  label="C_element : 034"  # scripted group (container) (typed FeaturePython)
  n = 6
  ref = C_element
FEATURE [App::DocumentObjectGroupPython] H_element062  label="H_element : 031"  # scripted group (container) (typed FeaturePython)
  n = 5
  ref = H_element
FEATURE [App::DocumentObjectGroupPython] N_element029  label="N_element : 012"  # scripted group (container) (typed FeaturePython)
  n = 1
  ref = N_element
FEATURE [App::DocumentObjectGroupPython] O_element069  label="O_element : 034"  # scripted group (container) (typed FeaturePython)
  n = 2
  ref = O_element
FEATURE [App::DocumentObjectGroupPython] G4_NITROBENZENE  # scripted group (container) (typed FeaturePython)
  Dunit = g/cm3
  Dvalue = 1.19867
  Group = -> [C_element068,H_element062,N_element029,O_element069]
  conduct = 2
  density = 1
  expand = 3
  formula = G4_NITROBENZENE
  name = G4_NITROBENZENE
  specific = 4
FEATURE [App::DocumentObjectGroupPython] N_element030  label="N_element : 013"  # scripted group (container) (typed FeaturePython)
  n = 2
  ref = N_element
FEATURE [App::DocumentObjectGroupPython] O_element070  label="O_element : 035"  # scripted group (container) (typed FeaturePython)
  n = 1
  ref = O_element
FEATURE [App::DocumentObjectGroupPython] G4_NITROUS_OXIDE  # scripted group (container) (typed FeaturePython)
  Dunit = g/cm3
  Dvalue = 0.00183094
  Group = -> [N_element030,O_element070]
  conduct = 2
  density = 1
  expand = 3
  formula = G4_NITROUS_OXIDE
  name = G4_NITROUS_OXIDE
  specific = 4
FEATURE [App::DocumentObjectGroupPython] H_element063  label="H_element : 0.104"  # scripted group (container) (typed FeaturePython)
  n = 0.103509
FEATURE [App::DocumentObjectGroupPython] C_element069  label="C_element : 0.648"  # scripted group (container) (typed FeaturePython)
  n = 0.648416
FEATURE [App::DocumentObjectGroupPython] N_element031  label="N_element : 0.100"  # scripted group (container) (typed FeaturePython)
  n = 0.0995361
FEATURE [App::DocumentObjectGroupPython] O_element071  label="O_element : 0.149"  # scripted group (container) (typed FeaturePython)
  n = 0.148539
FEATURE [App::DocumentObjectGroupPython] G4_NYLON_8062  label="G4_NYLON-8062"  # scripted group (container) (typed FeaturePython)
  Dunit = g/cm3
  Dvalue = 1.08
  Group = -> [H_element063,C_element069,N_element031,O_element071]
  conduct = 2
  density = 1
  expand = 3
  formula = G4_NYLON-8062
  name = G4_NYLON-8062
  specific = 4
FEATURE [App::DocumentObjectGroupPython] C_element070  label="C_element : 035"  # scripted group (container) (typed FeaturePython)
  n = 6
  ref = C_element
FEATURE [App::DocumentObjectGroupPython] H_element064  label="H_element : 11"  # scripted group (container) (typed FeaturePython)
  n = 11
  ref = H_element
FEATURE [App::DocumentObjectGroupPython] N_element032  label="N_element : 014"  # scripted group (container) (typed FeaturePython)
  n = 1
  ref = N_element
FEATURE [App::DocumentObjectGroupPython] O_element072  label="O_element : 036"  # scripted group (container) (typed FeaturePython)
  n = 1
  ref = O_element
FEATURE [App::DocumentObjectGroupPython] G4_NYLON_6_6  label="G4_NYLON-6-6"  # scripted group (container) (typed FeaturePython)
  Dunit = g/cm3
  Dvalue = 1.14
  Group = -> [C_element070,H_element064,N_element032,O_element072]
  conduct = 2
  density = 1
  expand = 3
  formula = G4_NYLON-6-6
  name = G4_NYLON-6-6
  specific = 4
FEATURE [App::DocumentObjectGroupPython] H_element065  label="H_element : 0.139"  # scripted group (container) (typed FeaturePython)
  n = 0.107062
FEATURE [App::DocumentObjectGroupPython] C_element071  label="C_element : 0.680"  # scripted group (container) (typed FeaturePython)
  n = 0.680449
FEATURE [App::DocumentObjectGroupPython] N_element033  label="N_element : 0.099"  # scripted group (container) (typed FeaturePython)
  n = 0.099189
FEATURE [App::DocumentObjectGroupPython] O_element073  label="O_element : 0.113"  # scripted group (container) (typed FeaturePython)
  n = 0.1133
FEATURE [App::DocumentObjectGroupPython] G4_NYLON_6_10  label="G4_NYLON-6-10"  # scripted group (container) (typed FeaturePython)
  Dunit = g/cm3
  Dvalue = 1.14
  Group = -> [H_element065,C_element071,N_element033,O_element073]
  conduct = 2
  density = 1
  expand = 3
  formula = G4_NYLON-6-10
  name = G4_NYLON-6-10
  specific = 4
FEATURE [App::DocumentObjectGroupPython] H_element066  label="H_element : 0.140"  # scripted group (container) (typed FeaturePython)
  n = 0.115476
FEATURE [App::DocumentObjectGroupPython] C_element072  label="C_element : 0.721"  # scripted group (container) (typed FeaturePython)
  n = 0.720818
FEATURE [App::DocumentObjectGroupPython] N_element034  label="N_element : 0.076"  # scripted group (container) (typed FeaturePython)
  n = 0.0764169
FEATURE [App::DocumentObjectGroupPython] O_element074  label="O_element : 0.087"  # scripted group (container) (typed FeaturePython)
  n = 0.0872889
FEATURE [App::DocumentObjectGroupPython] G4_NYLON_11_RILSAN  label="G4_NYLON-11_RILSAN"  # scripted group (container) (typed FeaturePython)
  Dunit = g/cm3
  Dvalue = 1.425
  Group = -> [H_element066,C_element072,N_element034,O_element074]
  conduct = 2
  density = 1
  expand = 3
  formula = G4_NYLON-11_RILSAN
  name = G4_NYLON-11_RILSAN
  specific = 4
FEATURE [App::DocumentObjectGroupPython] C_element073  label="C_element : 8"  # scripted group (container) (typed FeaturePython)
  n = 8
  ref = C_element
FEATURE [App::DocumentObjectGroupPython] H_element067  label="H_element : 18"  # scripted group (container) (typed FeaturePython)
  n = 18
  ref = H_element
FEATURE [App::DocumentObjectGroupPython] G4_OCTANE  # scripted group (container) (typed FeaturePython)
  Dunit = g/cm3
  Dvalue = 0.7026
  Group = -> [C_element073,H_element067]
  conduct = 2
  density = 1
  expand = 3
  formula = G4_OCTANE
  name = G4_OCTANE
  specific = 4
FEATURE [App::DocumentObjectGroupPython] C_element074  label="C_element : 25"  # scripted group (container) (typed FeaturePython)
  n = 25
  ref = C_element
FEATURE [App::DocumentObjectGroupPython] H_element068  label="H_element : 52"  # scripted group (container) (typed FeaturePython)
  n = 52
  ref = H_element
FEATURE [App::DocumentObjectGroupPython] G4_PARAFFIN  # scripted group (container) (typed FeaturePython)
  Dunit = g/cm3
  Dvalue = 0.93
  Group = -> [C_element074,H_element068]
  conduct = 2
  density = 1
  expand = 3
  formula = G4_PARAFFIN
  name = G4_PARAFFIN
  specific = 4
FEATURE [App::DocumentObjectGroupPython] C_element075  label="C_element : 036"  # scripted group (container) (typed FeaturePython)
  n = 5
  ref = C_element
FEATURE [App::DocumentObjectGroupPython] H_element069  label="H_element : 032"  # scripted group (container) (typed FeaturePython)
  n = 12
  ref = H_element
FEATURE [App::DocumentObjectGroupPython] G4_N_PENTANE  label="G4_N-PENTANE"  # scripted group (container) (typed FeaturePython)
  Dunit = g/cm3
  Dvalue = 0.6262
  Group = -> [C_element075,H_element069]
  conduct = 2
  density = 1
  expand = 3
  formula = G4_N-PENTANE
  name = G4_N-PENTANE
  specific = 4
FEATURE [App::DocumentObjectGroupPython] H_element070  label="H_element : 0.014"  # scripted group (container) (typed FeaturePython)
  n = 0.0141
FEATURE [App::DocumentObjectGroupPython] C_element076  label="C_element : 0.072"  # scripted group (container) (typed FeaturePython)
  n = 0.072261
FEATURE [App::DocumentObjectGroupPython] N_element035  label="N_element : 0.019"  # scripted group (container) (typed FeaturePython)
  n = 0.01932
FEATURE [App::DocumentObjectGroupPython] O_element075  label="O_element : 0.066"  # scripted group (container) (typed FeaturePython)
  n = 0.066101
FEATURE [App::DocumentObjectGroupPython] S_element019  label="S_element : 0.020"  # scripted group (container) (typed FeaturePython)
  n = 0.00189
FEATURE [App::DocumentObjectGroupPython] Br_element004  label="Br_element : 0.349"  # scripted group (container) (typed FeaturePython)
  n = 0.349103
FEATURE [App::DocumentObjectGroupPython] Ag_element001  label="Ag_element : 0.474"  # scripted group (container) (typed FeaturePython)
  n = 0.474105
FEATURE [App::DocumentObjectGroupPython] I_element005  label="I_element : 0.003"  # scripted group (container) (typed FeaturePython)
  n = 0.00312
FEATURE [App::DocumentObjectGroupPython] G4_PHOTO_EMULSION  # scripted group (container) (typed FeaturePython)
  Dunit = g/cm3
  Dvalue = 3.815
  Group = -> [H_element070,C_element076,N_element035,O_element075,S_element019,Br_element004,Ag_element001,I_element005]
  conduct = 2
  density = 1
  expand = 3
  formula = G4_PHOTO_EMULSION
  name = G4_PHOTO_EMULSION
  specific = 4
FEATURE [App::DocumentObjectGroupPython] C_element077  label="C_element : 9"  # scripted group (container) (typed FeaturePython)
  n = 9
  ref = C_element
FEATURE [App::DocumentObjectGroupPython] H_element071  label="H_element : 033"  # scripted group (container) (typed FeaturePython)
  n = 10
  ref = H_element
FEATURE [App::DocumentObjectGroupPython] G4_PLASTIC_SC_VINYLTOLUENE  # scripted group (container) (typed FeaturePython)
  Dunit = g/cm3
  Dvalue = 1.032
  Group = -> [C_element077,H_element071]
  conduct = 2
  density = 1
  expand = 3
  formula = G4_PLASTIC_SC_VINYLTOLUENE
  name = G4_PLASTIC_SC_VINYLTOLUENE
  specific = 4
FEATURE [App::DocumentObjectGroupPython] Pu_element001  label="Pu_element : 1"  # scripted group (container) (typed FeaturePython)
  n = 1
  ref = Pu_element
FEATURE [App::DocumentObjectGroupPython] O_element076  label="O_element : 037"  # scripted group (container) (typed FeaturePython)
  n = 2
  ref = O_element
FEATURE [App::DocumentObjectGroupPython] G4_PLUTONIUM_DIOXIDE  # scripted group (container) (typed FeaturePython)
  Dunit = g/cm3
  Dvalue = 11.46
  Group = -> [Pu_element001,O_element076]
  conduct = 2
  density = 1
  expand = 3
  formula = G4_PLUTONIUM_DIOXIDE
  name = G4_PLUTONIUM_DIOXIDE
  specific = 4
FEATURE [App::DocumentObjectGroupPython] C_element078  label="C_element : 037"  # scripted group (container) (typed FeaturePython)
  n = 3
  ref = C_element
FEATURE [App::DocumentObjectGroupPython] H_element072  label="H_element : 034"  # scripted group (container) (typed FeaturePython)
  n = 3
  ref = H_element
FEATURE [App::DocumentObjectGroupPython] N_element036  label="N_element : 015"  # scripted group (container) (typed FeaturePython)
  n = 1
  ref = N_element
FEATURE [App::DocumentObjectGroupPython] G4_POLYACRYLONITRILE  # scripted group (container) (typed FeaturePython)
  Dunit = g/cm3
  Dvalue = 1.17
  Group = -> [C_element078,H_element072,N_element036]
  conduct = 2
  density = 1
  expand = 3
  formula = G4_POLYACRYLONITRILE
  name = G4_POLYACRYLONITRILE
  specific = 4
FEATURE [App::DocumentObjectGroupPython] C_element079  label="C_element : 16"  # scripted group (container) (typed FeaturePython)
  n = 16
  ref = C_element
FEATURE [App::DocumentObjectGroupPython] H_element073  label="H_element : 035"  # scripted group (container) (typed FeaturePython)
  n = 14
  ref = H_element
FEATURE [App::DocumentObjectGroupPython] O_element077  label="O_element : 038"  # scripted group (container) (typed FeaturePython)
  n = 3
  ref = O_element
FEATURE [App::DocumentObjectGroupPython] G4_POLYCARBONATE  # scripted group (container) (typed FeaturePython)
  Dunit = g/cm3
  Dvalue = 1.2
  Group = -> [C_element079,H_element073,O_element077]
  conduct = 2
  density = 1
  expand = 3
  formula = G4_POLYCARBONATE
  name = G4_POLYCARBONATE
  specific = 4
FEATURE [App::DocumentObjectGroupPython] C_element080  label="C_element : 038"  # scripted group (container) (typed FeaturePython)
  n = 8
  ref = C_element
FEATURE [App::DocumentObjectGroupPython] H_element074  label="H_element : 036"  # scripted group (container) (typed FeaturePython)
  n = 7
  ref = H_element
FEATURE [App::DocumentObjectGroupPython] Cl_element017  label="Cl_element : 007"  # scripted group (container) (typed FeaturePython)
  n = 1
  ref = Cl_element
FEATURE [App::DocumentObjectGroupPython] G4_POLYCHLOROSTYRENE  # scripted group (container) (typed FeaturePython)
  Dunit = g/cm3
  Dvalue = 1.3
  Group = -> [C_element080,H_element074,Cl_element017]
  conduct = 2
  density = 1
  expand = 3
  formula = G4_POLYCHLOROSTYRENE
  name = G4_POLYCHLOROSTYRENE
  specific = 4
FEATURE [App::DocumentObjectGroupPython] C_element081  label="C_element : 039"  # scripted group (container) (typed FeaturePython)
  n = 1
  ref = C_element
FEATURE [App::DocumentObjectGroupPython] H_element075  label="H_element : 037"  # scripted group (container) (typed FeaturePython)
  n = 2
  ref = H_element
FEATURE [App::DocumentObjectGroupPython] G4_POLYETHYLENE  # scripted group (container) (typed FeaturePython)
  Dunit = g/cm3
  Dvalue = 0.94
  Group = -> [C_element081,H_element075]
  conduct = 2
  density = 1
  expand = 3
  formula = G4_POLYETHYLENE
  name = G4_POLYETHYLENE
  specific = 4
FEATURE [App::DocumentObjectGroupPython] C_element082  label="C_element : 040"  # scripted group (container) (typed FeaturePython)
  n = 10
  ref = C_element
FEATURE [App::DocumentObjectGroupPython] H_element076  label="H_element : 038"  # scripted group (container) (typed FeaturePython)
  n = 8
  ref = H_element
FEATURE [App::DocumentObjectGroupPython] O_element078  label="O_element : 039"  # scripted group (container) (typed FeaturePython)
  n = 4
  ref = O_element
FEATURE [App::DocumentObjectGroupPython] G4_MYLAR  # scripted group (container) (typed FeaturePython)
  Dunit = g/cm3
  Dvalue = 1.4
  Group = -> [C_element082,H_element076,O_element078]
  conduct = 2
  density = 1
  expand = 3
  formula = G4_MYLAR
  name = G4_MYLAR
  specific = 4
FEATURE [App::DocumentObjectGroupPython] C_element083  label="C_element : 041"  # scripted group (container) (typed FeaturePython)
  n = 5
  ref = C_element
FEATURE [App::DocumentObjectGroupPython] H_element077  label="H_element : 039"  # scripted group (container) (typed FeaturePython)
  n = 8
  ref = H_element
FEATURE [App::DocumentObjectGroupPython] O_element079  label="O_element : 040"  # scripted group (container) (typed FeaturePython)
  n = 2
  ref = O_element
FEATURE [App::DocumentObjectGroupPython] G4_PLEXIGLASS  # scripted group (container) (typed FeaturePython)
  Dunit = g/cm3
  Dvalue = 1.19
  Group = -> [C_element083,H_element077,O_element079]
  conduct = 2
  density = 1
  expand = 3
  formula = G4_PLEXIGLASS
  name = G4_PLEXIGLASS
  specific = 4
FEATURE [App::DocumentObjectGroupPython] C_element084  label="C_element : 042"  # scripted group (container) (typed FeaturePython)
  n = 1
  ref = C_element
FEATURE [App::DocumentObjectGroupPython] H_element078  label="H_element : 040"  # scripted group (container) (typed FeaturePython)
  n = 2
  ref = H_element
FEATURE [App::DocumentObjectGroupPython] O_element080  label="O_element : 041"  # scripted group (container) (typed FeaturePython)
  n = 1
  ref = O_element
FEATURE [App::DocumentObjectGroupPython] G4_POLYOXYMETHYLENE  # scripted group (container) (typed FeaturePython)
  Dunit = g/cm3
  Dvalue = 1.425
  Group = -> [C_element084,H_element078,O_element080]
  conduct = 2
  density = 1
  expand = 3
  formula = G4_POLYOXYMETHYLENE
  name = G4_POLYOXYMETHYLENE
  specific = 4
FEATURE [App::DocumentObjectGroupPython] C_element085  label="C_element : 043"  # scripted group (container) (typed FeaturePython)
  n = 2
  ref = C_element
FEATURE [App::DocumentObjectGroupPython] H_element079  label="H_element : 041"  # scripted group (container) (typed FeaturePython)
  n = 4
  ref = H_element
FEATURE [App::DocumentObjectGroupPython] G4_POLYPROPYLENE  # scripted group (container) (typed FeaturePython)
  Dunit = g/cm3
  Dvalue = 0.9
  Group = -> [C_element085,H_element079]
  conduct = 2
  density = 1
  expand = 3
  formula = G4_POLYPROPYLENE
  name = G4_POLYPROPYLENE
  specific = 4
FEATURE [App::DocumentObjectGroupPython] C_element086  label="C_element : 044"  # scripted group (container) (typed FeaturePython)
  n = 8
  ref = C_element
FEATURE [App::DocumentObjectGroupPython] H_element080  label="H_element : 042"  # scripted group (container) (typed FeaturePython)
  n = 8
  ref = H_element
FEATURE [App::DocumentObjectGroupPython] G4_POLYSTYRENE  # scripted group (container) (typed FeaturePython)
  Dunit = g/cm3
  Dvalue = 1.06
  Group = -> [C_element086,H_element080]
  conduct = 2
  density = 1
  expand = 3
  formula = G4_POLYSTYRENE
  name = G4_POLYSTYRENE
  specific = 4
FEATURE [App::DocumentObjectGroupPython] C_element087  label="C_element : 045"  # scripted group (container) (typed FeaturePython)
  n = 2
  ref = C_element
FEATURE [App::DocumentObjectGroupPython] F_element014  label="F_element : 4"  # scripted group (container) (typed FeaturePython)
  n = 4
  ref = F_element
FEATURE [App::DocumentObjectGroupPython] G4_TEFLON  # scripted group (container) (typed FeaturePython)
  Dunit = g/cm3
  Dvalue = 2.2
  Group = -> [C_element087,F_element014]
  conduct = 2
  density = 1
  expand = 3
  formula = G4_TEFLON
  name = G4_TEFLON
  specific = 4
FEATURE [App::DocumentObjectGroupPython] C_element088  label="C_element : 046"  # scripted group (container) (typed FeaturePython)
  n = 2
  ref = C_element
FEATURE [App::DocumentObjectGroupPython] F_element015  label="F_element : 006"  # scripted group (container) (typed FeaturePython)
  n = 3
  ref = F_element
FEATURE [App::DocumentObjectGroupPython] Cl_element018  label="Cl_element : 008"  # scripted group (container) (typed FeaturePython)
  n = 1
  ref = Cl_element
FEATURE [App::DocumentObjectGroupPython] G4_POLYTRIFLUOROCHLOROETHYLENE  # scripted group (container) (typed FeaturePython)
  Dunit = g/cm3
  Dvalue = 2.1
  Group = -> [C_element088,F_element015,Cl_element018]
  conduct = 2
  density = 1
  expand = 3
  formula = G4_POLYTRIFLUOROCHLOROETHYLENE
  name = G4_POLYTRIFLUOROCHLOROETHYLENE
  specific = 4
FEATURE [App::DocumentObjectGroupPython] C_element089  label="C_element : 047"  # scripted group (container) (typed FeaturePython)
  n = 4
  ref = C_element
FEATURE [App::DocumentObjectGroupPython] H_element081  label="H_element : 043"  # scripted group (container) (typed FeaturePython)
  n = 6
  ref = H_element
FEATURE [App::DocumentObjectGroupPython] O_element081  label="O_element : 042"  # scripted group (container) (typed FeaturePython)
  n = 2
  ref = O_element
FEATURE [App::DocumentObjectGroupPython] G4_POLYVINYL_ACETATE  # scripted group (container) (typed FeaturePython)
  Dunit = g/cm3
  Dvalue = 1.19
  Group = -> [C_element089,H_element081,O_element081]
  conduct = 2
  density = 1
  expand = 3
  formula = G4_POLYVINYL_ACETATE
  name = G4_POLYVINYL_ACETATE
  specific = 4
FEATURE [App::DocumentObjectGroupPython] C_element090  label="C_element : 048"  # scripted group (container) (typed FeaturePython)
  n = 2
  ref = C_element
FEATURE [App::DocumentObjectGroupPython] H_element082  label="H_element : 044"  # scripted group (container) (typed FeaturePython)
  n = 4
  ref = H_element
FEATURE [App::DocumentObjectGroupPython] O_element082  label="O_element : 043"  # scripted group (container) (typed FeaturePython)
  n = 1
  ref = O_element
FEATURE [App::DocumentObjectGroupPython] G4_POLYVINYL_ALCOHOL  # scripted group (container) (typed FeaturePython)
  Dunit = g/cm3
  Dvalue = 1.3
  Group = -> [C_element090,H_element082,O_element082]
  conduct = 2
  density = 1
  expand = 3
  formula = G4_POLYVINYL_ALCOHOL
  name = G4_POLYVINYL_ALCOHOL
  specific = 4
FEATURE [App::DocumentObjectGroupPython] C_element091  label="C_element : 049"  # scripted group (container) (typed FeaturePython)
  n = 8
  ref = C_element
FEATURE [App::DocumentObjectGroupPython] H_element083  label="H_element : 045"  # scripted group (container) (typed FeaturePython)
  n = 14
  ref = H_element
FEATURE [App::DocumentObjectGroupPython] O_element083  label="O_element : 044"  # scripted group (container) (typed FeaturePython)
  n = 2
  ref = O_element
FEATURE [App::DocumentObjectGroupPython] G4_POLYVINYL_BUTYRAL  # scripted group (container) (typed FeaturePython)
  Dunit = g/cm3
  Dvalue = 1.12
  Group = -> [C_element091,H_element083,O_element083]
  conduct = 2
  density = 1
  expand = 3
  formula = G4_POLYVINYL_BUTYRAL
  name = G4_POLYVINYL_BUTYRAL
  specific = 4
FEATURE [App::DocumentObjectGroupPython] C_element092  label="C_element : 050"  # scripted group (container) (typed FeaturePython)
  n = 2
  ref = C_element
FEATURE [App::DocumentObjectGroupPython] H_element084  label="H_element : 046"  # scripted group (container) (typed FeaturePython)
  n = 3
  ref = H_element
FEATURE [App::DocumentObjectGroupPython] Cl_element019  label="Cl_element : 009"  # scripted group (container) (typed FeaturePython)
  n = 1
  ref = Cl_element
FEATURE [App::DocumentObjectGroupPython] G4_POLYVINYL_CHLORIDE  # scripted group (container) (typed FeaturePython)
  Dunit = g/cm3
  Dvalue = 1.3
  Group = -> [C_element092,H_element084,Cl_element019]
  conduct = 2
  density = 1
  expand = 3
  formula = G4_POLYVINYL_CHLORIDE
  name = G4_POLYVINYL_CHLORIDE
  specific = 4
FEATURE [App::DocumentObjectGroupPython] C_element093  label="C_element : 051"  # scripted group (container) (typed FeaturePython)
  n = 2
  ref = C_element
FEATURE [App::DocumentObjectGroupPython] H_element085  label="H_element : 047"  # scripted group (container) (typed FeaturePython)
  n = 2
  ref = H_element
FEATURE [App::DocumentObjectGroupPython] Cl_element020  label="Cl_element : 010"  # scripted group (container) (typed FeaturePython)
  n = 2
  ref = Cl_element
FEATURE [App::DocumentObjectGroupPython] G4_POLYVINYLIDENE_CHLORIDE  # scripted group (container) (typed FeaturePython)
  Dunit = g/cm3
  Dvalue = 1.7
  Group = -> [C_element093,H_element085,Cl_element020]
  conduct = 2
  density = 1
  expand = 3
  formula = G4_POLYVINYLIDENE_CHLORIDE
  name = G4_POLYVINYLIDENE_CHLORIDE
  specific = 4
FEATURE [App::DocumentObjectGroupPython] C_element094  label="C_element : 052"  # scripted group (container) (typed FeaturePython)
  n = 2
  ref = C_element
FEATURE [App::DocumentObjectGroupPython] H_element086  label="H_element : 048"  # scripted group (container) (typed FeaturePython)
  n = 2
  ref = H_element
FEATURE [App::DocumentObjectGroupPython] F_element016  label="F_element : 007"  # scripted group (container) (typed FeaturePython)
  n = 2
  ref = F_element
FEATURE [App::DocumentObjectGroupPython] G4_POLYVINYLIDENE_FLUORIDE  # scripted group (container) (typed FeaturePython)
  Dunit = g/cm3
  Dvalue = 1.76
  Group = -> [C_element094,H_element086,F_element016]
  conduct = 2
  density = 1
  expand = 3
  formula = G4_POLYVINYLIDENE_FLUORIDE
  name = G4_POLYVINYLIDENE_FLUORIDE
  specific = 4
FEATURE [App::DocumentObjectGroupPython] C_element095  label="C_element : 053"  # scripted group (container) (typed FeaturePython)
  n = 6
  ref = C_element
FEATURE [App::DocumentObjectGroupPython] H_element087  label="H_element : 9"  # scripted group (container) (typed FeaturePython)
  n = 9
  ref = H_element
FEATURE [App::DocumentObjectGroupPython] N_element037  label="N_element : 016"  # scripted group (container) (typed FeaturePython)
  n = 1
  ref = N_element
FEATURE [App::DocumentObjectGroupPython] O_element084  label="O_element : 045"  # scripted group (container) (typed FeaturePython)
  n = 1
  ref = O_element
FEATURE [App::DocumentObjectGroupPython] G4_POLYVINYL_PYRROLIDONE  # scripted group (container) (typed FeaturePython)
  Dunit = g/cm3
  Dvalue = 1.25
  Group = -> [C_element095,H_element087,N_element037,O_element084]
  conduct = 2
  density = 1
  expand = 3
  formula = G4_POLYVINYL_PYRROLIDONE
  name = G4_POLYVINYL_PYRROLIDONE
  specific = 4
FEATURE [App::DocumentObjectGroupPython] K_element008  label="K_element : 1"  # scripted group (container) (typed FeaturePython)
  n = 1
  ref = K_element
FEATURE [App::DocumentObjectGroupPython] I_element006  label="I_element : 003"  # scripted group (container) (typed FeaturePython)
  n = 1
  ref = I_element
FEATURE [App::DocumentObjectGroupPython] G4_POTASSIUM_IODIDE  # scripted group (container) (typed FeaturePython)
  Dunit = g/cm3
  Dvalue = 3.13
  Group = -> [K_element008,I_element006]
  conduct = 2
  density = 1
  expand = 3
  formula = G4_POTASSIUM_IODIDE
  name = G4_POTASSIUM_IODIDE
  specific = 4
FEATURE [App::DocumentObjectGroupPython] K_element009  label="K_element : 2"  # scripted group (container) (typed FeaturePython)
  n = 2
  ref = K_element
FEATURE [App::DocumentObjectGroupPython] O_element085  label="O_element : 046"  # scripted group (container) (typed FeaturePython)
  n = 1
  ref = O_element
FEATURE [App::DocumentObjectGroupPython] G4_POTASSIUM_OXIDE  # scripted group (container) (typed FeaturePython)
  Dunit = g/cm3
  Dvalue = 2.32
  Group = -> [K_element009,O_element085]
  conduct = 2
  density = 1
  expand = 3
  formula = G4_POTASSIUM_OXIDE
  name = G4_POTASSIUM_OXIDE
  specific = 4
FEATURE [App::DocumentObjectGroupPython] C_element096  label="C_element : 054"  # scripted group (container) (typed FeaturePython)
  n = 3
  ref = C_element
FEATURE [App::DocumentObjectGroupPython] H_element088  label="H_element : 049"  # scripted group (container) (typed FeaturePython)
  n = 8
  ref = H_element
FEATURE [App::DocumentObjectGroupPython] G4_PROPANE  # scripted group (container) (typed FeaturePython)
  Dunit = g/cm3
  Dvalue = 0.00187939
  Group = -> [C_element096,H_element088]
  conduct = 2
  density = 1
  expand = 3
  formula = G4_PROPANE
  name = G4_PROPANE
  specific = 4
FEATURE [App::DocumentObjectGroupPython] C_element097  label="C_element : 055"  # scripted group (container) (typed FeaturePython)
  n = 3
  ref = C_element
FEATURE [App::DocumentObjectGroupPython] H_element089  label="H_element : 050"  # scripted group (container) (typed FeaturePython)
  n = 8
  ref = H_element
FEATURE [App::DocumentObjectGroupPython] G4_lPROPANE  # scripted group (container) (typed FeaturePython)
  Dunit = g/cm3
  Dvalue = 0.43
  Group = -> [C_element097,H_element089]
  conduct = 2
  density = 1
  expand = 3
  formula = G4_lPROPANE
  name = G4_lPROPANE
  specific = 4
FEATURE [App::DocumentObjectGroupPython] C_element098  label="C_element : 056"  # scripted group (container) (typed FeaturePython)
  n = 3
  ref = C_element
FEATURE [App::DocumentObjectGroupPython] H_element090  label="H_element : 051"  # scripted group (container) (typed FeaturePython)
  n = 8
  ref = H_element
FEATURE [App::DocumentObjectGroupPython] O_element086  label="O_element : 047"  # scripted group (container) (typed FeaturePython)
  n = 1
  ref = O_element
FEATURE [App::DocumentObjectGroupPython] G4_N_PROPYL_ALCOHOL  label="G4_N-PROPYL_ALCOHOL"  # scripted group (container) (typed FeaturePython)
  Dunit = g/cm3
  Dvalue = 0.8035
  Group = -> [C_element098,H_element090,O_element086]
  conduct = 2
  density = 1
  expand = 3
  formula = G4_N-PROPYL_ALCOHOL
  name = G4_N-PROPYL_ALCOHOL
  specific = 4
FEATURE [App::DocumentObjectGroupPython] C_element099  label="C_element : 057"  # scripted group (container) (typed FeaturePython)
  n = 5
  ref = C_element
FEATURE [App::DocumentObjectGroupPython] H_element091  label="H_element : 052"  # scripted group (container) (typed FeaturePython)
  n = 5
  ref = H_element
FEATURE [App::DocumentObjectGroupPython] N_element038  label="N_element : 017"  # scripted group (container) (typed FeaturePython)
  n = 1
  ref = N_element
FEATURE [App::DocumentObjectGroupPython] G4_PYRIDINE  # scripted group (container) (typed FeaturePython)
  Dunit = g/cm3
  Dvalue = 0.9819
  Group = -> [C_element099,H_element091,N_element038]
  conduct = 2
  density = 1
  expand = 3
  formula = G4_PYRIDINE
  name = G4_PYRIDINE
  specific = 4
FEATURE [App::DocumentObjectGroupPython] H_element092  label="H_element : 0.144"  # scripted group (container) (typed FeaturePython)
  n = 0.143711
FEATURE [App::DocumentObjectGroupPython] C_element100  label="C_element : 0.856"  # scripted group (container) (typed FeaturePython)
  n = 0.856289
FEATURE [App::DocumentObjectGroupPython] G4_RUBBER_BUTYL  # scripted group (container) (typed FeaturePython)
  Dunit = g/cm3
  Dvalue = 0.92
  Group = -> [H_element092,C_element100]
  conduct = 2
  density = 1
  expand = 3
  formula = G4_RUBBER_BUTYL
  name = G4_RUBBER_BUTYL
  specific = 4
FEATURE [App::DocumentObjectGroupPython] H_element093  label="H_element : 0.118"  # scripted group (container) (typed FeaturePython)
  n = 0.118371
FEATURE [App::DocumentObjectGroupPython] C_element101  label="C_element : 0.882"  # scripted group (container) (typed FeaturePython)
  n = 0.881629
FEATURE [App::DocumentObjectGroupPython] G4_RUBBER_NATURAL  # scripted group (container) (typed FeaturePython)
  Dunit = g/cm3
  Dvalue = 0.92
  Group = -> [H_element093,C_element101]
  conduct = 2
  density = 1
  expand = 3
  formula = G4_RUBBER_NATURAL
  name = G4_RUBBER_NATURAL
  specific = 4
FEATURE [App::DocumentObjectGroupPython] H_element094  label="H_element : 0.145"  # scripted group (container) (typed FeaturePython)
  n = 0.05692
FEATURE [App::DocumentObjectGroupPython] C_element102  label="C_element : 0.543"  # scripted group (container) (typed FeaturePython)
  n = 0.542646
FEATURE [App::DocumentObjectGroupPython] Cl_element021  label="Cl_element : 0.400"  # scripted group (container) (typed FeaturePython)
  n = 0.400434
FEATURE [App::DocumentObjectGroupPython] G4_RUBBER_NEOPRENE  # scripted group (container) (typed FeaturePython)
  Dunit = g/cm3
  Dvalue = 1.23
  Group = -> [H_element094,C_element102,Cl_element021]
  conduct = 2
  density = 1
  expand = 3
  formula = G4_RUBBER_NEOPRENE
  name = G4_RUBBER_NEOPRENE
  specific = 4
FEATURE [App::DocumentObjectGroupPython] Si_element006  label="Si_element : 1"  # scripted group (container) (typed FeaturePython)
  n = 1
  ref = Si_element
FEATURE [App::DocumentObjectGroupPython] O_element087  label="O_element : 048"  # scripted group (container) (typed FeaturePython)
  n = 2
  ref = O_element
FEATURE [App::DocumentObjectGroupPython] G4_SILICON_DIOXIDE  # scripted group (container) (typed FeaturePython)
  Dunit = g/cm3
  Dvalue = 2.32
  Group = -> [Si_element006,O_element087]
  conduct = 2
  density = 1
  expand = 3
  formula = G4_SILICON_DIOXIDE
  name = G4_SILICON_DIOXIDE
  specific = 4
FEATURE [App::DocumentObjectGroupPython] Ag_element002  label="Ag_element : 1"  # scripted group (container) (typed FeaturePython)
  n = 1
  ref = Ag_element
FEATURE [App::DocumentObjectGroupPython] Br_element005  label="Br_element : 003"  # scripted group (container) (typed FeaturePython)
  n = 1
  ref = Br_element
FEATURE [App::DocumentObjectGroupPython] G4_SILVER_BROMIDE  # scripted group (container) (typed FeaturePython)
  Dunit = g/cm3
  Dvalue = 6.473
  Group = -> [Ag_element002,Br_element005]
  conduct = 2
  density = 1
  expand = 3
  formula = G4_SILVER_BROMIDE
  name = G4_SILVER_BROMIDE
  specific = 4
FEATURE [App::DocumentObjectGroupPython] Ag_element003  label="Ag_element : 002"  # scripted group (container) (typed FeaturePython)
  n = 1
  ref = Ag_element
FEATURE [App::DocumentObjectGroupPython] Cl_element022  label="Cl_element : 011"  # scripted group (container) (typed FeaturePython)
  n = 1
  ref = Cl_element
FEATURE [App::DocumentObjectGroupPython] G4_SILVER_CHLORIDE  # scripted group (container) (typed FeaturePython)
  Dunit = g/cm3
  Dvalue = 5.56
  Group = -> [Ag_element003,Cl_element022]
  conduct = 2
  density = 1
  expand = 3
  formula = G4_SILVER_CHLORIDE
  name = G4_SILVER_CHLORIDE
  specific = 4
FEATURE [App::DocumentObjectGroupPython] Br_element006  label="Br_element : 0.423"  # scripted group (container) (typed FeaturePython)
  n = 0.422895
FEATURE [App::DocumentObjectGroupPython] Ag_element004  label="Ag_element : 0.574"  # scripted group (container) (typed FeaturePython)
  n = 0.573748
FEATURE [App::DocumentObjectGroupPython] I_element007  label="I_element : 0.649"  # scripted group (container) (typed FeaturePython)
  n = 0.003357
FEATURE [App::DocumentObjectGroupPython] G4_SILVER_HALIDES  # scripted group (container) (typed FeaturePython)
  Dunit = g/cm3
  Dvalue = 6.47
  Group = -> [Br_element006,Ag_element004,I_element007]
  conduct = 2
  density = 1
  expand = 3
  formula = G4_SILVER_HALIDES
  name = G4_SILVER_HALIDES
  specific = 4
FEATURE [App::DocumentObjectGroupPython] Ag_element005  label="Ag_element : 003"  # scripted group (container) (typed FeaturePython)
  n = 1
  ref = Ag_element
FEATURE [App::DocumentObjectGroupPython] I_element008  label="I_element : 004"  # scripted group (container) (typed FeaturePython)
  n = 1
  ref = I_element
FEATURE [App::DocumentObjectGroupPython] G4_SILVER_IODIDE  # scripted group (container) (typed FeaturePython)
  Dunit = g/cm3
  Dvalue = 6.01
  Group = -> [Ag_element005,I_element008]
  conduct = 2
  density = 1
  expand = 3
  formula = G4_SILVER_IODIDE
  name = G4_SILVER_IODIDE
  specific = 4
FEATURE [App::DocumentObjectGroupPython] H_element095  label="H_element : 0.100"  # scripted group (container) (typed FeaturePython)
  n = 0.1
FEATURE [App::DocumentObjectGroupPython] C_element103  label="C_element : 0.204"  # scripted group (container) (typed FeaturePython)
  n = 0.204
FEATURE [App::DocumentObjectGroupPython] N_element039  label="N_element : 0.759"  # scripted group (container) (typed FeaturePython)
  n = 0.042
FEATURE [App::DocumentObjectGroupPython] O_element088  label="O_element : 0.645"  # scripted group (container) (typed FeaturePython)
  n = 0.645
FEATURE [App::DocumentObjectGroupPython] Na_element013  label="Na_element : 0.100"  # scripted group (container) (typed FeaturePython)
  n = 0.002
FEATURE [App::DocumentObjectGroupPython] P_element009  label="P_element : 0.107"  # scripted group (container) (typed FeaturePython)
  n = 0.001
FEATURE [App::DocumentObjectGroupPython] S_element020  label="S_element : 0.021"  # scripted group (container) (typed FeaturePython)
  n = 0.002
FEATURE [App::DocumentObjectGroupPython] Cl_element023  label="Cl_element : 0.590"  # scripted group (container) (typed FeaturePython)
  n = 0.003
FEATURE [App::DocumentObjectGroupPython] K_element010  label="K_element : 0.001"  # scripted group (container) (typed FeaturePython)
  n = 0.001
FEATURE [App::DocumentObjectGroupPython] G4_SKIN_ICRP  # scripted group (container) (typed FeaturePython)
  Dunit = g/cm3
  Dvalue = 1.09
  Group = -> [H_element095,C_element103,N_element039,O_element088,Na_element013,P_element009,S_element020,Cl_element023,K_element010]
  conduct = 2
  density = 1
  expand = 3
  formula = G4_SKIN_ICRP
  name = G4_SKIN_ICRP
  specific = 4
FEATURE [App::DocumentObjectGroupPython] Na_element014  label="Na_element : 2"  # scripted group (container) (typed FeaturePython)
  n = 2
  ref = Na_element
FEATURE [App::DocumentObjectGroupPython] C_element104  label="C_element : 058"  # scripted group (container) (typed FeaturePython)
  n = 1
  ref = C_element
FEATURE [App::DocumentObjectGroupPython] O_element089  label="O_element : 049"  # scripted group (container) (typed FeaturePython)
  n = 3
  ref = O_element
FEATURE [App::DocumentObjectGroupPython] G4_SODIUM_CARBONATE  # scripted group (container) (typed FeaturePython)
  Dunit = g/cm3
  Dvalue = 2.532
  Group = -> [Na_element014,C_element104,O_element089]
  conduct = 2
  density = 1
  expand = 3
  formula = G4_SODIUM_CARBONATE
  name = G4_SODIUM_CARBONATE
  specific = 4
FEATURE [App::DocumentObjectGroupPython] Na_element015  label="Na_element : 1"  # scripted group (container) (typed FeaturePython)
  n = 1
  ref = Na_element
FEATURE [App::DocumentObjectGroupPython] I_element009  label="I_element : 005"  # scripted group (container) (typed FeaturePython)
  n = 1
  ref = I_element
FEATURE [App::DocumentObjectGroupPython] G4_SODIUM_IODIDE  # scripted group (container) (typed FeaturePython)
  Dunit = g/cm3
  Dvalue = 3.667
  Group = -> [Na_element015,I_element009]
  conduct = 2
  density = 1
  expand = 3
  formula = G4_SODIUM_IODIDE
  name = G4_SODIUM_IODIDE
  specific = 4
FEATURE [App::DocumentObjectGroupPython] Na_element016  label="Na_element : 003"  # scripted group (container) (typed FeaturePython)
  n = 2
  ref = Na_element
FEATURE [App::DocumentObjectGroupPython] O_element090  label="O_element : 050"  # scripted group (container) (typed FeaturePython)
  n = 1
  ref = O_element
FEATURE [App::DocumentObjectGroupPython] G4_SODIUM_MONOXIDE  # scripted group (container) (typed FeaturePython)
  Dunit = g/cm3
  Dvalue = 2.27
  Group = -> [Na_element016,O_element090]
  conduct = 2
  density = 1
  expand = 3
  formula = G4_SODIUM_MONOXIDE
  name = G4_SODIUM_MONOXIDE
  specific = 4
FEATURE [App::DocumentObjectGroupPython] Na_element017  label="Na_element : 004"  # scripted group (container) (typed FeaturePython)
  n = 1
  ref = Na_element
FEATURE [App::DocumentObjectGroupPython] N_element040  label="N_element : 018"  # scripted group (container) (typed FeaturePython)
  n = 1
  ref = N_element
FEATURE [App::DocumentObjectGroupPython] O_element091  label="O_element : 051"  # scripted group (container) (typed FeaturePython)
  n = 3
  ref = O_element
FEATURE [App::DocumentObjectGroupPython] G4_SODIUM_NITRATE  # scripted group (container) (typed FeaturePython)
  Dunit = g/cm3
  Dvalue = 2.261
  Group = -> [Na_element017,N_element040,O_element091]
  conduct = 2
  density = 1
  expand = 3
  formula = G4_SODIUM_NITRATE
  name = G4_SODIUM_NITRATE
  specific = 4
FEATURE [App::DocumentObjectGroupPython] C_element105  label="C_element : 059"  # scripted group (container) (typed FeaturePython)
  n = 14
  ref = C_element
FEATURE [App::DocumentObjectGroupPython] H_element096  label="H_element : 053"  # scripted group (container) (typed FeaturePython)
  n = 12
  ref = H_element
FEATURE [App::DocumentObjectGroupPython] G4_STILBENE  # scripted group (container) (typed FeaturePython)
  Dunit = g/cm3
  Dvalue = 0.9707
  Group = -> [C_element105,H_element096]
  conduct = 2
  density = 1
  expand = 3
  formula = G4_STILBENE
  name = G4_STILBENE
  specific = 4
FEATURE [App::DocumentObjectGroupPython] C_element106  label="C_element : 12"  # scripted group (container) (typed FeaturePython)
  n = 12
  ref = C_element
FEATURE [App::DocumentObjectGroupPython] H_element097  label="H_element : 22"  # scripted group (container) (typed FeaturePython)
  n = 22
  ref = H_element
FEATURE [App::DocumentObjectGroupPython] O_element092  label="O_element : 11"  # scripted group (container) (typed FeaturePython)
  n = 11
  ref = O_element
FEATURE [App::DocumentObjectGroupPython] G4_SUCROSE  # scripted group (container) (typed FeaturePython)
  Dunit = g/cm3
  Dvalue = 1.5805
  Group = -> [C_element106,H_element097,O_element092]
  conduct = 2
  density = 1
  expand = 3
  formula = G4_SUCROSE
  name = G4_SUCROSE
  specific = 4
FEATURE [App::DocumentObjectGroupPython] C_element107  label="C_element : 18"  # scripted group (container) (typed FeaturePython)
  n = 18
  ref = C_element
FEATURE [App::DocumentObjectGroupPython] H_element098  label="H_element : 054"  # scripted group (container) (typed FeaturePython)
  n = 14
  ref = H_element
FEATURE [App::DocumentObjectGroupPython] G4_TERPHENYL  # scripted group (container) (typed FeaturePython)
  Dunit = g/cm3
  Dvalue = 1.24
  Group = -> [C_element107,H_element098]
  conduct = 2
  density = 1
  expand = 3
  formula = G4_TERPHENYL
  name = G4_TERPHENYL
  specific = 4
FEATURE [App::DocumentObjectGroupPython] H_element099  label="H_element : 0.146"  # scripted group (container) (typed FeaturePython)
  n = 0.106
FEATURE [App::DocumentObjectGroupPython] C_element108  label="C_element : 0.883"  # scripted group (container) (typed FeaturePython)
  n = 0.099
FEATURE [App::DocumentObjectGroupPython] N_element041  label="N_element : 0.020"  # scripted group (container) (typed FeaturePython)
  n = 0.02
FEATURE [App::DocumentObjectGroupPython] O_element093  label="O_element : 0.766"  # scripted group (container) (typed FeaturePython)
  n = 0.766
FEATURE [App::DocumentObjectGroupPython] Na_element018  label="Na_element : 0.101"  # scripted group (container) (typed FeaturePython)
  n = 0.002
FEATURE [App::DocumentObjectGroupPython] P_element010  label="P_element : 0.108"  # scripted group (container) (typed FeaturePython)
  n = 0.001
FEATURE [App::DocumentObjectGroupPython] S_element021  label="S_element : 0.022"  # scripted group (container) (typed FeaturePython)
  n = 0.002
FEATURE [App::DocumentObjectGroupPython] Cl_element024  label="Cl_element : 0.002"  # scripted group (container) (typed FeaturePython)
  n = 0.002
FEATURE [App::DocumentObjectGroupPython] K_element011  label="K_element : 0.017"  # scripted group (container) (typed FeaturePython)
  n = 0.002
FEATURE [App::DocumentObjectGroupPython] G4_TESTIS_ICRP  # scripted group (container) (typed FeaturePython)
  Dunit = g/cm3
  Dvalue = 1.04
  Group = -> [H_element099,C_element108,N_element041,O_element093,Na_element018,P_element010,S_element021,Cl_element024,K_element011]
  conduct = 2
  density = 1
  expand = 3
  formula = G4_TESTIS_ICRP
  name = G4_TESTIS_ICRP
  specific = 4
FEATURE [App::DocumentObjectGroupPython] C_element109  label="C_element : 060"  # scripted group (container) (typed FeaturePython)
  n = 2
  ref = C_element
FEATURE [App::DocumentObjectGroupPython] Cl_element025  label="Cl_element : 012"  # scripted group (container) (typed FeaturePython)
  n = 4
  ref = Cl_element
FEATURE [App::DocumentObjectGroupPython] G4_TETRACHLOROETHYLENE  # scripted group (container) (typed FeaturePython)
  Dunit = g/cm3
  Dvalue = 1.625
  Group = -> [C_element109,Cl_element025]
  conduct = 2
  density = 1
  expand = 3
  formula = G4_TETRACHLOROETHYLENE
  name = G4_TETRACHLOROETHYLENE
  specific = 4
FEATURE [App::DocumentObjectGroupPython] Tl_element001  label="Tl_element : 1"  # scripted group (container) (typed FeaturePython)
  n = 1
  ref = Tl_element
FEATURE [App::DocumentObjectGroupPython] Cl_element026  label="Cl_element : 013"  # scripted group (container) (typed FeaturePython)
  n = 1
  ref = Cl_element
FEATURE [App::DocumentObjectGroupPython] G4_THALLIUM_CHLORIDE  # scripted group (container) (typed FeaturePython)
  Dunit = g/cm3
  Dvalue = 7.004
  Group = -> [Tl_element001,Cl_element026]
  conduct = 2
  density = 1
  expand = 3
  formula = G4_THALLIUM_CHLORIDE
  name = G4_THALLIUM_CHLORIDE
  specific = 4
FEATURE [App::DocumentObjectGroupPython] H_element100  label="H_element : 0.147"  # scripted group (container) (typed FeaturePython)
  n = 0.105
FEATURE [App::DocumentObjectGroupPython] C_element110  label="C_element : 0.256"  # scripted group (container) (typed FeaturePython)
  n = 0.256
FEATURE [App::DocumentObjectGroupPython] N_element042  label="N_element : 0.760"  # scripted group (container) (typed FeaturePython)
  n = 0.027
FEATURE [App::DocumentObjectGroupPython] O_element094  label="O_element : 0.602"  # scripted group (container) (typed FeaturePython)
  n = 0.602
FEATURE [App::DocumentObjectGroupPython] Na_element019  label="Na_element : 0.102"  # scripted group (container) (typed FeaturePython)
  n = 0.001
FEATURE [App::DocumentObjectGroupPython] P_element011  label="P_element : 0.109"  # scripted group (container) (typed FeaturePython)
  n = 0.002
FEATURE [App::DocumentObjectGroupPython] S_element022  label="S_element : 0.023"  # scripted group (container) (typed FeaturePython)
  n = 0.003
FEATURE [App::DocumentObjectGroupPython] Cl_element027  label="Cl_element : 0.591"  # scripted group (container) (typed FeaturePython)
  n = 0.002
FEATURE [App::DocumentObjectGroupPython] K_element012  label="K_element : 0.018"  # scripted group (container) (typed FeaturePython)
  n = 0.002
FEATURE [App::DocumentObjectGroupPython] G4_TISSUE_SOFT_ICRP  # scripted group (container) (typed FeaturePython)
  Dunit = g/cm3
  Dvalue = 1.03
  Group = -> [H_element100,C_element110,N_element042,O_element094,Na_element019,P_element011,S_element022,Cl_element027,K_element012]
  conduct = 2
  density = 1
  expand = 3
  formula = G4_TISSUE_SOFT_ICRP
  name = G4_TISSUE_SOFT_ICRP
  specific = 4
FEATURE [App::DocumentObjectGroupPython] H_element101  label="H_element : 0.148"  # scripted group (container) (typed FeaturePython)
  n = 0.101
FEATURE [App::DocumentObjectGroupPython] C_element111  label="C_element : 0.111"  # scripted group (container) (typed FeaturePython)
  n = 0.111
FEATURE [App::DocumentObjectGroupPython] N_element043  label="N_element : 0.026"  # scripted group (container) (typed FeaturePython)
  n = 0.026
FEATURE [App::DocumentObjectGroupPython] O_element095  label="O_element : 0.762"  # scripted group (container) (typed FeaturePython)
  n = 0.762
FEATURE [App::DocumentObjectGroupPython] G4_TISSUE_SOFT_ICRU_4  label="G4_TISSUE_SOFT_ICRU-4"  # scripted group (container) (typed FeaturePython)
  Dunit = g/cm3
  Dvalue = 1
  Group = -> [H_element101,C_element111,N_element043,O_element095]
  conduct = 2
  density = 1
  expand = 3
  formula = G4_TISSUE_SOFT_ICRU-4
  name = G4_TISSUE_SOFT_ICRU-4
  specific = 4
FEATURE [App::DocumentObjectGroupPython] H_element102  label="H_element : 0.149"  # scripted group (container) (typed FeaturePython)
  n = 0.101869
FEATURE [App::DocumentObjectGroupPython] C_element112  label="C_element : 0.456"  # scripted group (container) (typed FeaturePython)
  n = 0.456179
FEATURE [App::DocumentObjectGroupPython] N_element044  label="N_element : 0.761"  # scripted group (container) (typed FeaturePython)
  n = 0.035172
FEATURE [App::DocumentObjectGroupPython] O_element096  label="O_element : 0.407"  # scripted group (container) (typed FeaturePython)
  n = 0.40678
FEATURE [App::DocumentObjectGroupPython] G4_TISSUE_METHANE  label="G4_TISSUE-METHANE"  # scripted group (container) (typed FeaturePython)
  Dunit = g/cm3
  Dvalue = 0.00106409
  Group = -> [H_element102,C_element112,N_element044,O_element096]
  conduct = 2
  density = 1
  expand = 3
  formula = G4_TISSUE-METHANE
  name = G4_TISSUE-METHANE
  specific = 4
FEATURE [App::DocumentObjectGroupPython] H_element103  label="H_element : 0.103"  # scripted group (container) (typed FeaturePython)
  n = 0.102672
FEATURE [App::DocumentObjectGroupPython] C_element113  label="C_element : 0.569"  # scripted group (container) (typed FeaturePython)
  n = 0.56894
FEATURE [App::DocumentObjectGroupPython] N_element045  label="N_element : 0.762"  # scripted group (container) (typed FeaturePython)
  n = 0.035022
FEATURE [App::DocumentObjectGroupPython] O_element097  label="O_element : 0.293"  # scripted group (container) (typed FeaturePython)
  n = 0.293366
FEATURE [App::DocumentObjectGroupPython] G4_TISSUE_PROPANE  label="G4_TISSUE-PROPANE"  # scripted group (container) (typed FeaturePython)
  Dunit = g/cm3
  Dvalue = 0.00182628
  Group = -> [H_element103,C_element113,N_element045,O_element097]
  conduct = 2
  density = 1
  expand = 3
  formula = G4_TISSUE-PROPANE
  name = G4_TISSUE-PROPANE
  specific = 4
FEATURE [App::DocumentObjectGroupPython] Ti_element003  label="Ti_element : 1"  # scripted group (container) (typed FeaturePython)
  n = 1
  ref = Ti_element
FEATURE [App::DocumentObjectGroupPython] O_element098  label="O_element : 052"  # scripted group (container) (typed FeaturePython)
  n = 2
  ref = O_element
FEATURE [App::DocumentObjectGroupPython] G4_TITANIUM_DIOXIDE  # scripted group (container) (typed FeaturePython)
  Dunit = g/cm3
  Dvalue = 4.26
  Group = -> [Ti_element003,O_element098]
  conduct = 2
  density = 1
  expand = 3
  formula = G4_TITANIUM_DIOXIDE
  name = G4_TITANIUM_DIOXIDE
  specific = 4
FEATURE [App::DocumentObjectGroupPython] C_element114  label="C_element : 061"  # scripted group (container) (typed FeaturePython)
  n = 7
  ref = C_element
FEATURE [App::DocumentObjectGroupPython] H_element104  label="H_element : 055"  # scripted group (container) (typed FeaturePython)
  n = 8
  ref = H_element
FEATURE [App::DocumentObjectGroupPython] G4_TOLUENE  # scripted group (container) (typed FeaturePython)
  Dunit = g/cm3
  Dvalue = 0.8669
  Group = -> [C_element114,H_element104]
  conduct = 2
  density = 1
  expand = 3
  formula = G4_TOLUENE
  name = G4_TOLUENE
  specific = 4
FEATURE [App::DocumentObjectGroupPython] C_element115  label="C_element : 062"  # scripted group (container) (typed FeaturePython)
  n = 2
  ref = C_element
FEATURE [App::DocumentObjectGroupPython] H_element105  label="H_element : 056"  # scripted group (container) (typed FeaturePython)
  n = 1
  ref = H_element
FEATURE [App::DocumentObjectGroupPython] Cl_element028  label="Cl_element : 014"  # scripted group (container) (typed FeaturePython)
  n = 3
  ref = Cl_element
FEATURE [App::DocumentObjectGroupPython] G4_TRICHLOROETHYLENE  # scripted group (container) (typed FeaturePython)
  Dunit = g/cm3
  Dvalue = 1.46
  Group = -> [C_element115,H_element105,Cl_element028]
  conduct = 2
  density = 1
  expand = 3
  formula = G4_TRICHLOROETHYLENE
  name = G4_TRICHLOROETHYLENE
  specific = 4
FEATURE [App::DocumentObjectGroupPython] C_element116  label="C_element : 063"  # scripted group (container) (typed FeaturePython)
  n = 6
  ref = C_element
FEATURE [App::DocumentObjectGroupPython] H_element106  label="H_element : 15"  # scripted group (container) (typed FeaturePython)
  n = 15
  ref = H_element
FEATURE [App::DocumentObjectGroupPython] O_element099  label="O_element : 053"  # scripted group (container) (typed FeaturePython)
  n = 4
  ref = O_element
FEATURE [App::DocumentObjectGroupPython] P_element012  label="P_element : 1"  # scripted group (container) (typed FeaturePython)
  n = 1
  ref = P_element
FEATURE [App::DocumentObjectGroupPython] G4_TRIETHYL_PHOSPHATE  # scripted group (container) (typed FeaturePython)
  Dunit = g/cm3
  Dvalue = 1.07
  Group = -> [C_element116,H_element106,O_element099,P_element012]
  conduct = 2
  density = 1
  expand = 3
  formula = G4_TRIETHYL_PHOSPHATE
  name = G4_TRIETHYL_PHOSPHATE
  specific = 4
FEATURE [App::DocumentObjectGroupPython] W_element003  label="W_element : 003"  # scripted group (container) (typed FeaturePython)
  n = 1
  ref = W_element
FEATURE [App::DocumentObjectGroupPython] F_element017  label="F_element : 6"  # scripted group (container) (typed FeaturePython)
  n = 6
  ref = F_element
FEATURE [App::DocumentObjectGroupPython] G4_TUNGSTEN_HEXAFLUORIDE  # scripted group (container) (typed FeaturePython)
  Dunit = g/cm3
  Dvalue = 2.4
  Group = -> [W_element003,F_element017]
  conduct = 2
  density = 1
  expand = 3
  formula = G4_TUNGSTEN_HEXAFLUORIDE
  name = G4_TUNGSTEN_HEXAFLUORIDE
  specific = 4
FEATURE [App::DocumentObjectGroupPython] U_element001  label="U_element : 1"  # scripted group (container) (typed FeaturePython)
  n = 1
  ref = U_element
FEATURE [App::DocumentObjectGroupPython] C_element117  label="C_element : 064"  # scripted group (container) (typed FeaturePython)
  n = 2
  ref = C_element
FEATURE [App::DocumentObjectGroupPython] G4_URANIUM_DICARBIDE  # scripted group (container) (typed FeaturePython)
  Dunit = g/cm3
  Dvalue = 11.28
  Group = -> [U_element001,C_element117]
  conduct = 2
  density = 1
  expand = 3
  formula = G4_URANIUM_DICARBIDE
  name = G4_URANIUM_DICARBIDE
  specific = 4
FEATURE [App::DocumentObjectGroupPython] U_element002  label="U_element : 002"  # scripted group (container) (typed FeaturePython)
  n = 1
  ref = U_element
FEATURE [App::DocumentObjectGroupPython] C_element118  label="C_element : 065"  # scripted group (container) (typed FeaturePython)
  n = 1
  ref = C_element
FEATURE [App::DocumentObjectGroupPython] G4_URANIUM_MONOCARBIDE  # scripted group (container) (typed FeaturePython)
  Dunit = g/cm3
  Dvalue = 13.63
  Group = -> [U_element002,C_element118]
  conduct = 2
  density = 1
  expand = 3
  formula = G4_URANIUM_MONOCARBIDE
  name = G4_URANIUM_MONOCARBIDE
  specific = 4
FEATURE [App::DocumentObjectGroupPython] U_element003  label="U_element : 003"  # scripted group (container) (typed FeaturePython)
  n = 1
  ref = U_element
FEATURE [App::DocumentObjectGroupPython] O_element100  label="O_element : 054"  # scripted group (container) (typed FeaturePython)
  n = 2
  ref = O_element
FEATURE [App::DocumentObjectGroupPython] G4_URANIUM_OXIDE  # scripted group (container) (typed FeaturePython)
  Dunit = g/cm3
  Dvalue = 10.96
  Group = -> [U_element003,O_element100]
  conduct = 2
  density = 1
  expand = 3
  formula = G4_URANIUM_OXIDE
  name = G4_URANIUM_OXIDE
  specific = 4
FEATURE [App::DocumentObjectGroupPython] C_element119  label="C_element : 066"  # scripted group (container) (typed FeaturePython)
  n = 1
  ref = C_element
FEATURE [App::DocumentObjectGroupPython] H_element107  label="H_element : 057"  # scripted group (container) (typed FeaturePython)
  n = 4
  ref = H_element
FEATURE [App::DocumentObjectGroupPython] N_element046  label="N_element : 019"  # scripted group (container) (typed FeaturePython)
  n = 2
  ref = N_element
FEATURE [App::DocumentObjectGroupPython] O_element101  label="O_element : 055"  # scripted group (container) (typed FeaturePython)
  n = 1
  ref = O_element
FEATURE [App::DocumentObjectGroupPython] G4_UREA  # scripted group (container) (typed FeaturePython)
  Dunit = g/cm3
  Dvalue = 1.323
  Group = -> [C_element119,H_element107,N_element046,O_element101]
  conduct = 2
  density = 1
  expand = 3
  formula = G4_UREA
  name = G4_UREA
  specific = 4
FEATURE [App::DocumentObjectGroupPython] C_element120  label="C_element : 067"  # scripted group (container) (typed FeaturePython)
  n = 5
  ref = C_element
FEATURE [App::DocumentObjectGroupPython] H_element108  label="H_element : 058"  # scripted group (container) (typed FeaturePython)
  n = 11
  ref = H_element
FEATURE [App::DocumentObjectGroupPython] N_element047  label="N_element : 020"  # scripted group (container) (typed FeaturePython)
  n = 1
  ref = N_element
FEATURE [App::DocumentObjectGroupPython] O_element102  label="O_element : 056"  # scripted group (container) (typed FeaturePython)
  n = 2
  ref = O_element
FEATURE [App::DocumentObjectGroupPython] G4_VALINE  # scripted group (container) (typed FeaturePython)
  Dunit = g/cm3
  Dvalue = 1.23
  Group = -> [C_element120,H_element108,N_element047,O_element102]
  conduct = 2
  density = 1
  expand = 3
  formula = G4_VALINE
  name = G4_VALINE
  specific = 4
FEATURE [App::DocumentObjectGroupPython] H_element109  label="H_element : 0.009"  # scripted group (container) (typed FeaturePython)
  n = 0.009417
FEATURE [App::DocumentObjectGroupPython] C_element121  label="C_element : 0.281"  # scripted group (container) (typed FeaturePython)
  n = 0.280555
FEATURE [App::DocumentObjectGroupPython] F_element018  label="F_element : 0.710"  # scripted group (container) (typed FeaturePython)
  n = 0.710028
FEATURE [App::DocumentObjectGroupPython] G4_VITON  # scripted group (container) (typed FeaturePython)
  Dunit = g/cm3
  Dvalue = 1.8
  Group = -> [H_element109,C_element121,F_element018]
  conduct = 2
  density = 1
  expand = 3
  formula = G4_VITON
  name = G4_VITON
  specific = 4
FEATURE [App::DocumentObjectGroupPython] H_element110  label="H_element : 059"  # scripted group (container) (typed FeaturePython)
  n = 2
  ref = H_element
FEATURE [App::DocumentObjectGroupPython] O_element103  label="O_element : 057"  # scripted group (container) (typed FeaturePython)
  n = 1
  ref = O_element
FEATURE [App::DocumentObjectGroupPython] G4_WATER  # scripted group (container) (typed FeaturePython)
  Dunit = g/cm3
  Dvalue = 1
  Group = -> [H_element110,O_element103]
  conduct = 2
  density = 1
  expand = 3
  formula = G4_WATER
  name = G4_WATER
  specific = 4
FEATURE [App::DocumentObjectGroupPython] H_element111  label="H_element : 060"  # scripted group (container) (typed FeaturePython)
  n = 2
  ref = H_element
FEATURE [App::DocumentObjectGroupPython] O_element104  label="O_element : 058"  # scripted group (container) (typed FeaturePython)
  n = 1
  ref = O_element
FEATURE [App::DocumentObjectGroupPython] G4_WATER_VAPOR  # scripted group (container) (typed FeaturePython)
  Dunit = g/cm3
  Dvalue = 0.000756182
  Group = -> [H_element111,O_element104]
  conduct = 2
  density = 1
  expand = 3
  formula = G4_WATER_VAPOR
  name = G4_WATER_VAPOR
  specific = 4
FEATURE [App::DocumentObjectGroupPython] C_element122  label="C_element : 068"  # scripted group (container) (typed FeaturePython)
  n = 8
  ref = C_element
FEATURE [App::DocumentObjectGroupPython] H_element112  label="H_element : 061"  # scripted group (container) (typed FeaturePython)
  n = 10
  ref = H_element
FEATURE [App::DocumentObjectGroupPython] G4_XYLENE  # scripted group (container) (typed FeaturePython)
  Dunit = g/cm3
  Dvalue = 0.87
  Group = -> [C_element122,H_element112]
  conduct = 2
  density = 1
  expand = 3
  formula = G4_XYLENE
  name = G4_XYLENE
  specific = 4
FEATURE [App::DocumentObjectGroupPython] C_element123  label="C_element : 069"  # scripted group (container) (typed FeaturePython)
  n = 1
  ref = C_element
FEATURE [App::DocumentObjectGroupPython] G4_GRAPHITE  # scripted group (container) (typed FeaturePython)
  Dunit = g/cm3
  Dvalue = 2.21
  Group = -> [C_element123]
  conduct = 2
  density = 1
  expand = 3
  formula = G4_GRAPHITE
  name = G4_GRAPHITE
  specific = 4
FEATURE [App::DocumentObjectGroupPython] NIST  # scripted group (container) (typed FeaturePython)
  Group = -> [G4_A_150_TISSUE,G4_ACETONE,G4_ACETYLENE,G4_ADENINE,G4_ADIPOSE_TISSUE_ICRP,G4_AIR,G4_ALANINE,G4_ALUMINUM_OXIDE,G4_AMBER,G4_AMMONIA,G4_ANILINE,G4_ANTHRACENE,G4_B_100_BONE,G4_BAKELITE,G4_BARIUM_FLUORIDE,G4_BARIUM_SULFATE,G4_BENZENE,G4_BERYLLIUM_OXIDE,G4_BGO,G4_BLOOD_ICRP,G4_BONE_COMPACT_ICRU,G4_BONE_CORTICAL_ICRP,G4_BORON_CARBIDE,G4_BORON_OXIDE,G4_BRAIN_ICRP,G4_BUTANE,G4_N_BUTYL_ALCOHOL,G4_C_552,+152 more]
FEATURE [App::DocumentObjectGroupPython] H_element113  label="H_element : 062"  # scripted group (container) (typed FeaturePython)
  n = 1
  ref = H_element
FEATURE [App::DocumentObjectGroupPython] G4_H  # scripted group (container) (typed FeaturePython)
  Dunit = g/cm3
  Dvalue = 8.3748e-05
  Group = -> [H_element113]
  conduct = 2
  density = 1
  expand = 3
  formula = H
  name = G4_H
  specific = 4
FEATURE [App::DocumentObjectGroupPython] He_element001  label="He_element : 1"  # scripted group (container) (typed FeaturePython)
  n = 1
  ref = He_element
FEATURE [App::DocumentObjectGroupPython] G4_He  # scripted group (container) (typed FeaturePython)
  Dunit = g/cm3
  Dvalue = 0.000166322
  Group = -> [He_element001]
  conduct = 2
  density = 1
  expand = 3
  formula = He
  name = G4_He
  specific = 4
FEATURE [App::DocumentObjectGroupPython] Li_element008  label="Li_element : 008"  # scripted group (container) (typed FeaturePython)
  n = 1
  ref = Li_element
FEATURE [App::DocumentObjectGroupPython] G4_Li  # scripted group (container) (typed FeaturePython)
  Dunit = g/cm3
  Dvalue = 0.534
  Group = -> [Li_element008]
  conduct = 2
  density = 1
  expand = 3
  formula = Li
  name = G4_Li
  specific = 4
FEATURE [App::DocumentObjectGroupPython] Be_element002  label="Be_element : 002"  # scripted group (container) (typed FeaturePython)
  n = 1
  ref = Be_element
FEATURE [App::DocumentObjectGroupPython] G4_Be  # scripted group (container) (typed FeaturePython)
  Dunit = g/cm3
  Dvalue = 1.848
  Group = -> [Be_element002]
  conduct = 2
  density = 1
  expand = 3
  formula = Be
  name = G4_Be
  specific = 4
FEATURE [App::DocumentObjectGroupPython] B_element007  label="B_element : 007"  # scripted group (container) (typed FeaturePython)
  n = 1
  ref = B_element
FEATURE [App::DocumentObjectGroupPython] G4_B  # scripted group (container) (typed FeaturePython)
  Dunit = g/cm3
  Dvalue = 2.37
  Group = -> [B_element007]
  conduct = 2
  density = 1
  expand = 3
  formula = B
  name = G4_B
  specific = 4
FEATURE [App::DocumentObjectGroupPython] C_element124  label="C_element : 070"  # scripted group (container) (typed FeaturePython)
  n = 1
  ref = C_element
FEATURE [App::DocumentObjectGroupPython] G4_C  # scripted group (container) (typed FeaturePython)
  Dunit = g/cm3
  Dvalue = 2
  Group = -> [C_element124]
  conduct = 2
  density = 1
  expand = 3
  formula = C
  name = G4_C
  specific = 4
FEATURE [App::DocumentObjectGroupPython] N_element048  label="N_element : 021"  # scripted group (container) (typed FeaturePython)
  n = 1
  ref = N_element
FEATURE [App::DocumentObjectGroupPython] G4_N  # scripted group (container) (typed FeaturePython)
  Dunit = g/cm3
  Dvalue = 0.0011652
  Group = -> [N_element048]
  conduct = 2
  density = 1
  expand = 3
  formula = N
  name = G4_N
  specific = 4
FEATURE [App::DocumentObjectGroupPython] O_element105  label="O_element : 059"  # scripted group (container) (typed FeaturePython)
  n = 1
  ref = O_element
FEATURE [App::DocumentObjectGroupPython] G4_O  # scripted group (container) (typed FeaturePython)
  Dunit = g/cm3
  Dvalue = 0.00133151
  Group = -> [O_element105]
  conduct = 2
  density = 1
  expand = 3
  formula = O
  name = G4_O
  specific = 4
FEATURE [App::DocumentObjectGroupPython] F_element019  label="F_element : 008"  # scripted group (container) (typed FeaturePython)
  n = 1
  ref = F_element
FEATURE [App::DocumentObjectGroupPython] G4_F  # scripted group (container) (typed FeaturePython)
  Dunit = g/cm3
  Dvalue = 0.00158029
  Group = -> [F_element019]
  conduct = 2
  density = 1
  expand = 3
  formula = F
  name = G4_F
  specific = 4
FEATURE [App::DocumentObjectGroupPython] Ne_element001  label="Ne_element : 1"  # scripted group (container) (typed FeaturePython)
  n = 1
  ref = Ne_element
FEATURE [App::DocumentObjectGroupPython] G4_Ne  # scripted group (container) (typed FeaturePython)
  Dunit = g/cm3
  Dvalue = 0.000838505
  Group = -> [Ne_element001]
  conduct = 2
  density = 1
  expand = 3
  formula = Ne
  name = G4_Ne
  specific = 4
FEATURE [App::DocumentObjectGroupPython] Na_element020  label="Na_element : 005"  # scripted group (container) (typed FeaturePython)
  n = 1
  ref = Na_element
FEATURE [App::DocumentObjectGroupPython] G4_Na  # scripted group (container) (typed FeaturePython)
  Dunit = g/cm3
  Dvalue = 0.971
  Group = -> [Na_element020]
  conduct = 2
  density = 1
  expand = 3
  formula = Na
  name = G4_Na
  specific = 4
FEATURE [App::DocumentObjectGroupPython] Mg_element011  label="Mg_element : 005"  # scripted group (container) (typed FeaturePython)
  n = 1
  ref = Mg_element
FEATURE [App::DocumentObjectGroupPython] G4_Mg  # scripted group (container) (typed FeaturePython)
  Dunit = g/cm3
  Dvalue = 1.74
  Group = -> [Mg_element011]
  conduct = 2
  density = 1
  expand = 3
  formula = Mg
  name = G4_Mg
  specific = 4
FEATURE [App::DocumentObjectGroupPython] Al_element004  label="Al_element : 1"  # scripted group (container) (typed FeaturePython)
  n = 1
  ref = Al_element
FEATURE [App::DocumentObjectGroupPython] G4_Al  # scripted group (container) (typed FeaturePython)
  Dunit = g/cm3
  Dvalue = 2.699
  Group = -> [Al_element004]
  conduct = 2
  density = 1
  expand = 3
  formula = Al
  name = G4_Al
  specific = 4
FEATURE [App::DocumentObjectGroupPython] Si_element007  label="Si_element : 002"  # scripted group (container) (typed FeaturePython)
  n = 1
  ref = Si_element
FEATURE [App::DocumentObjectGroupPython] G4_Si  # scripted group (container) (typed FeaturePython)
  Dunit = g/cm3
  Dvalue = 2.33
  Group = -> [Si_element007]
  conduct = 2
  density = 1
  expand = 3
  formula = Si
  name = G4_Si
  specific = 4
FEATURE [App::DocumentObjectGroupPython] P_element013  label="P_element : 002"  # scripted group (container) (typed FeaturePython)
  n = 1
  ref = P_element
FEATURE [App::DocumentObjectGroupPython] G4_P  # scripted group (container) (typed FeaturePython)
  Dunit = g/cm3
  Dvalue = 2.2
  Group = -> [P_element013]
  conduct = 2
  density = 1
  expand = 3
  formula = P
  name = G4_P
  specific = 4
FEATURE [App::DocumentObjectGroupPython] S_element023  label="S_element : 007"  # scripted group (container) (typed FeaturePython)
  n = 1
  ref = S_element
FEATURE [App::DocumentObjectGroupPython] G4_S  # scripted group (container) (typed FeaturePython)
  Dunit = g/cm3
  Dvalue = 2
  Group = -> [S_element023]
  conduct = 2
  density = 1
  expand = 3
  formula = S
  name = G4_S
  specific = 4
FEATURE [App::DocumentObjectGroupPython] Cl_element029  label="Cl_element : 015"  # scripted group (container) (typed FeaturePython)
  n = 1
  ref = Cl_element
FEATURE [App::DocumentObjectGroupPython] G4_Cl  # scripted group (container) (typed FeaturePython)
  Dunit = g/cm3
  Dvalue = 0.00299473
  Group = -> [Cl_element029]
  conduct = 2
  density = 1
  expand = 3
  formula = Cl
  name = G4_Cl
  specific = 4
FEATURE [App::DocumentObjectGroupPython] Ar_element002  label="Ar_element : 1"  # scripted group (container) (typed FeaturePython)
  n = 1
  ref = Ar_element
FEATURE [App::DocumentObjectGroupPython] G4_Ar  # scripted group (container) (typed FeaturePython)
  Dunit = g/cm3
  Dvalue = 0.00166201
  Group = -> [Ar_element002]
  conduct = 2
  density = 1
  expand = 3
  formula = Ar
  name = G4_Ar
  specific = 4
FEATURE [App::DocumentObjectGroupPython] K_element013  label="K_element : 003"  # scripted group (container) (typed FeaturePython)
  n = 1
  ref = K_element
FEATURE [App::DocumentObjectGroupPython] G4_K  # scripted group (container) (typed FeaturePython)
  Dunit = g/cm3
  Dvalue = 0.862
  Group = -> [K_element013]
  conduct = 2
  density = 1
  expand = 3
  formula = K
  name = G4_K
  specific = 4
FEATURE [App::DocumentObjectGroupPython] Ca_element014  label="Ca_element : 007"  # scripted group (container) (typed FeaturePython)
  n = 1
  ref = Ca_element
FEATURE [App::DocumentObjectGroupPython] G4_Ca  # scripted group (container) (typed FeaturePython)
  Dunit = g/cm3
  Dvalue = 1.55
  Group = -> [Ca_element014]
  conduct = 2
  density = 1
  expand = 3
  formula = Ca
  name = G4_Ca
  specific = 4
FEATURE [App::DocumentObjectGroupPython] Sc_element001  label="Sc_element : 1"  # scripted group (container) (typed FeaturePython)
  n = 1
  ref = Sc_element
FEATURE [App::DocumentObjectGroupPython] G4_Sc  # scripted group (container) (typed FeaturePython)
  Dunit = g/cm3
  Dvalue = 2.989
  Group = -> [Sc_element001]
  conduct = 2
  density = 1
  expand = 3
  formula = Sc
  name = G4_Sc
  specific = 4
FEATURE [App::DocumentObjectGroupPython] Ti_element004  label="Ti_element : 002"  # scripted group (container) (typed FeaturePython)
  n = 1
  ref = Ti_element
FEATURE [App::DocumentObjectGroupPython] G4_Ti  # scripted group (container) (typed FeaturePython)
  Dunit = g/cm3
  Dvalue = 4.54
  Group = -> [Ti_element004]
  conduct = 2
  density = 1
  expand = 3
  formula = Ti
  name = G4_Ti
  specific = 4
FEATURE [App::DocumentObjectGroupPython] V_element001  label="V_element : 1"  # scripted group (container) (typed FeaturePython)
  n = 1
  ref = V_element
FEATURE [App::DocumentObjectGroupPython] G4_V  # scripted group (container) (typed FeaturePython)
  Dunit = g/cm3
  Dvalue = 6.11
  Group = -> [V_element001]
  conduct = 2
  density = 1
  expand = 3
  formula = V
  name = G4_V
  specific = 4
FEATURE [App::DocumentObjectGroupPython] Cr_element001  label="Cr_element : 1"  # scripted group (container) (typed FeaturePython)
  n = 1
  ref = Cr_element
FEATURE [App::DocumentObjectGroupPython] G4_Cr  # scripted group (container) (typed FeaturePython)
  Dunit = g/cm3
  Dvalue = 7.18
  Group = -> [Cr_element001]
  conduct = 2
  density = 1
  expand = 3
  formula = Cr
  name = G4_Cr
  specific = 4
FEATURE [App::DocumentObjectGroupPython] Mn_element001  label="Mn_element : 1"  # scripted group (container) (typed FeaturePython)
  n = 1
  ref = Mn_element
FEATURE [App::DocumentObjectGroupPython] G4_Mn  # scripted group (container) (typed FeaturePython)
  Dunit = g/cm3
  Dvalue = 7.44
  Group = -> [Mn_element001]
  conduct = 2
  density = 1
  expand = 3
  formula = Mn
  name = G4_Mn
  specific = 4
FEATURE [App::DocumentObjectGroupPython] Fe_element007  label="Fe_element : 004"  # scripted group (container) (typed FeaturePython)
  n = 1
  ref = Fe_element
FEATURE [App::DocumentObjectGroupPython] G4_Fe  # scripted group (container) (typed FeaturePython)
  Dunit = g/cm3
  Dvalue = 7.874
  Group = -> [Fe_element007]
  conduct = 2
  density = 1
  expand = 3
  formula = Fe
  name = G4_Fe
  specific = 4
FEATURE [App::DocumentObjectGroupPython] Co_element001  label="Co_element : 1"  # scripted group (container) (typed FeaturePython)
  n = 1
  ref = Co_element
FEATURE [App::DocumentObjectGroupPython] G4_Co  # scripted group (container) (typed FeaturePython)
  Dunit = g/cm3
  Dvalue = 8.9
  Group = -> [Co_element001]
  conduct = 2
  density = 1
  expand = 3
  formula = Co
  name = G4_Co
  specific = 4
FEATURE [App::DocumentObjectGroupPython] Ni_element001  label="Ni_element : 1"  # scripted group (container) (typed FeaturePython)
  n = 1
  ref = Ni_element
FEATURE [App::DocumentObjectGroupPython] G4_Ni  # scripted group (container) (typed FeaturePython)
  Dunit = g/cm3
  Dvalue = 8.902
  Group = -> [Ni_element001]
  conduct = 2
  density = 1
  expand = 3
  formula = Ni
  name = G4_Ni
  specific = 4
FEATURE [App::DocumentObjectGroupPython] Cu_element001  label="Cu_element : 1"  # scripted group (container) (typed FeaturePython)
  n = 1
  ref = Cu_element
FEATURE [App::DocumentObjectGroupPython] G4_Cu  # scripted group (container) (typed FeaturePython)
  Dunit = g/cm3
  Dvalue = 8.96
  Group = -> [Cu_element001]
  conduct = 2
  density = 1
  expand = 3
  formula = Cu
  name = G4_Cu
  specific = 4
FEATURE [App::DocumentObjectGroupPython] Zn_element001  label="Zn_element : 1"  # scripted group (container) (typed FeaturePython)
  n = 1
  ref = Zn_element
FEATURE [App::DocumentObjectGroupPython] G4_Zn  # scripted group (container) (typed FeaturePython)
  Dunit = g/cm3
  Dvalue = 7.133
  Group = -> [Zn_element001]
  conduct = 2
  density = 1
  expand = 3
  formula = Zn
  name = G4_Zn
  specific = 4
FEATURE [App::DocumentObjectGroupPython] Ga_element002  label="Ga_element : 002"  # scripted group (container) (typed FeaturePython)
  n = 1
  ref = Ga_element
FEATURE [App::DocumentObjectGroupPython] G4_Ga  # scripted group (container) (typed FeaturePython)
  Dunit = g/cm3
  Dvalue = 5.904
  Group = -> [Ga_element002]
  conduct = 2
  density = 1
  expand = 3
  formula = Ga
  name = G4_Ga
  specific = 4
FEATURE [App::DocumentObjectGroupPython] Ge_element002  label="Ge_element : 1"  # scripted group (container) (typed FeaturePython)
  n = 1
  ref = Ge_element
FEATURE [App::DocumentObjectGroupPython] G4_Ge  # scripted group (container) (typed FeaturePython)
  Dunit = g/cm3
  Dvalue = 5.323
  Group = -> [Ge_element002]
  conduct = 2
  density = 1
  expand = 3
  formula = Ge
  name = G4_Ge
  specific = 4
FEATURE [App::DocumentObjectGroupPython] As_element003  label="As_element : 002"  # scripted group (container) (typed FeaturePython)
  n = 1
  ref = As_element
FEATURE [App::DocumentObjectGroupPython] G4_As  # scripted group (container) (typed FeaturePython)
  Dunit = g/cm3
  Dvalue = 5.73
  Group = -> [As_element003]
  conduct = 2
  density = 1
  expand = 3
  formula = As
  name = G4_As
  specific = 4
FEATURE [App::DocumentObjectGroupPython] Se_element001  label="Se_element : 1"  # scripted group (container) (typed FeaturePython)
  n = 1
  ref = Se_element
FEATURE [App::DocumentObjectGroupPython] G4_Se  # scripted group (container) (typed FeaturePython)
  Dunit = g/cm3
  Dvalue = 4.5
  Group = -> [Se_element001]
  conduct = 2
  density = 1
  expand = 3
  formula = Se
  name = G4_Se
  specific = 4
FEATURE [App::DocumentObjectGroupPython] Br_element007  label="Br_element : 004"  # scripted group (container) (typed FeaturePython)
  n = 1
  ref = Br_element
FEATURE [App::DocumentObjectGroupPython] G4_Br  # scripted group (container) (typed FeaturePython)
  Dunit = g/cm3
  Dvalue = 0.0070721
  Group = -> [Br_element007]
  conduct = 2
  density = 1
  expand = 3
  formula = Br
  name = G4_Br
  specific = 4
FEATURE [App::DocumentObjectGroupPython] Kr_element001  label="Kr_element : 1"  # scripted group (container) (typed FeaturePython)
  n = 1
  ref = Kr_element
FEATURE [App::DocumentObjectGroupPython] G4_Kr  # scripted group (container) (typed FeaturePython)
  Dunit = g/cm3
  Dvalue = 0.00347832
  Group = -> [Kr_element001]
  conduct = 2
  density = 1
  expand = 3
  formula = Kr
  name = G4_Kr
  specific = 4
FEATURE [App::DocumentObjectGroupPython] Rb_element001  label="Rb_element : 1"  # scripted group (container) (typed FeaturePython)
  n = 1
  ref = Rb_element
FEATURE [App::DocumentObjectGroupPython] G4_Rb  # scripted group (container) (typed FeaturePython)
  Dunit = g/cm3
  Dvalue = 1.532
  Group = -> [Rb_element001]
  conduct = 2
  density = 1
  expand = 3
  formula = Rb
  name = G4_Rb
  specific = 4
FEATURE [App::DocumentObjectGroupPython] Sr_element001  label="Sr_element : 1"  # scripted group (container) (typed FeaturePython)
  n = 1
  ref = Sr_element
FEATURE [App::DocumentObjectGroupPython] G4_Sr  # scripted group (container) (typed FeaturePython)
  Dunit = g/cm3
  Dvalue = 2.54
  Group = -> [Sr_element001]
  conduct = 2
  density = 1
  expand = 3
  formula = Sr
  name = G4_Sr
  specific = 4
FEATURE [App::DocumentObjectGroupPython] Y_element001  label="Y_element : 1"  # scripted group (container) (typed FeaturePython)
  n = 1
  ref = Y_element
FEATURE [App::DocumentObjectGroupPython] G4_Y  # scripted group (container) (typed FeaturePython)
  Dunit = g/cm3
  Dvalue = 4.469
  Group = -> [Y_element001]
  conduct = 2
  density = 1
  expand = 3
  formula = Y
  name = G4_Y
  specific = 4
FEATURE [App::DocumentObjectGroupPython] Zr_element001  label="Zr_element : 1"  # scripted group (container) (typed FeaturePython)
  n = 1
  ref = Zr_element
FEATURE [App::DocumentObjectGroupPython] G4_Zr  # scripted group (container) (typed FeaturePython)
  Dunit = g/cm3
  Dvalue = 6.506
  Group = -> [Zr_element001]
  conduct = 2
  density = 1
  expand = 3
  formula = Zr
  name = G4_Zr
  specific = 4
FEATURE [App::DocumentObjectGroupPython] Nb_element001  label="Nb_element : 1"  # scripted group (container) (typed FeaturePython)
  n = 1
  ref = Nb_element
FEATURE [App::DocumentObjectGroupPython] G4_Nb  # scripted group (container) (typed FeaturePython)
  Dunit = g/cm3
  Dvalue = 8.57
  Group = -> [Nb_element001]
  conduct = 2
  density = 1
  expand = 3
  formula = Nb
  name = G4_Nb
  specific = 4
FEATURE [App::DocumentObjectGroupPython] Mo_element001  label="Mo_element : 1"  # scripted group (container) (typed FeaturePython)
  n = 1
  ref = Mo_element
FEATURE [App::DocumentObjectGroupPython] G4_Mo  # scripted group (container) (typed FeaturePython)
  Dunit = g/cm3
  Dvalue = 10.22
  Group = -> [Mo_element001]
  conduct = 2
  density = 1
  expand = 3
  formula = Mo
  name = G4_Mo
  specific = 4
FEATURE [App::DocumentObjectGroupPython] Tc_element001  label="Tc_element : 1"  # scripted group (container) (typed FeaturePython)
  n = 1
  ref = Tc_element
FEATURE [App::DocumentObjectGroupPython] G4_Tc  # scripted group (container) (typed FeaturePython)
  Dunit = g/cm3
  Dvalue = 11.5
  Group = -> [Tc_element001]
  conduct = 2
  density = 1
  expand = 3
  formula = Tc
  name = G4_Tc
  specific = 4
FEATURE [App::DocumentObjectGroupPython] Ru_element001  label="Ru_element : 1"  # scripted group (container) (typed FeaturePython)
  n = 1
  ref = Ru_element
FEATURE [App::DocumentObjectGroupPython] G4_Ru  # scripted group (container) (typed FeaturePython)
  Dunit = g/cm3
  Dvalue = 12.41
  Group = -> [Ru_element001]
  conduct = 2
  density = 1
  expand = 3
  formula = Ru
  name = G4_Ru
  specific = 4
FEATURE [App::DocumentObjectGroupPython] Rh_element001  label="Rh_element : 1"  # scripted group (container) (typed FeaturePython)
  n = 1
  ref = Rh_element
FEATURE [App::DocumentObjectGroupPython] G4_Rh  # scripted group (container) (typed FeaturePython)
  Dunit = g/cm3
  Dvalue = 12.41
  Group = -> [Rh_element001]
  conduct = 2
  density = 1
  expand = 3
  formula = Rh
  name = G4_Rh
  specific = 4
FEATURE [App::DocumentObjectGroupPython] Pd_element001  label="Pd_element : 1"  # scripted group (container) (typed FeaturePython)
  n = 1
  ref = Pd_element
FEATURE [App::DocumentObjectGroupPython] G4_Pd  # scripted group (container) (typed FeaturePython)
  Dunit = g/cm3
  Dvalue = 12.02
  Group = -> [Pd_element001]
  conduct = 2
  density = 1
  expand = 3
  formula = Pd
  name = G4_Pd
  specific = 4
FEATURE [App::DocumentObjectGroupPython] Ag_element006  label="Ag_element : 004"  # scripted group (container) (typed FeaturePython)
  n = 1
  ref = Ag_element
FEATURE [App::DocumentObjectGroupPython] G4_Ag  # scripted group (container) (typed FeaturePython)
  Dunit = g/cm3
  Dvalue = 10.5
  Group = -> [Ag_element006]
  conduct = 2
  density = 1
  expand = 3
  formula = Ag
  name = G4_Ag
  specific = 4
FEATURE [App::DocumentObjectGroupPython] Cd_element003  label="Cd_element : 003"  # scripted group (container) (typed FeaturePython)
  n = 1
  ref = Cd_element
FEATURE [App::DocumentObjectGroupPython] G4_Cd  # scripted group (container) (typed FeaturePython)
  Dunit = g/cm3
  Dvalue = 8.65
  Group = -> [Cd_element003]
  conduct = 2
  density = 1
  expand = 3
  formula = Cd
  name = G4_Cd
  specific = 4
FEATURE [App::DocumentObjectGroupPython] In_element001  label="In_element : 1"  # scripted group (container) (typed FeaturePython)
  n = 1
  ref = In_element
FEATURE [App::DocumentObjectGroupPython] G4_In  # scripted group (container) (typed FeaturePython)
  Dunit = g/cm3
  Dvalue = 7.31
  Group = -> [In_element001]
  conduct = 2
  density = 1
  expand = 3
  formula = In
  name = G4_In
  specific = 4
FEATURE [App::DocumentObjectGroupPython] Sn_element001  label="Sn_element : 1"  # scripted group (container) (typed FeaturePython)
  n = 1
  ref = Sn_element
FEATURE [App::DocumentObjectGroupPython] G4_Sn  # scripted group (container) (typed FeaturePython)
  Dunit = g/cm3
  Dvalue = 7.31
  Group = -> [Sn_element001]
  conduct = 2
  density = 1
  expand = 3
  formula = Sn
  name = G4_Sn
  specific = 4
FEATURE [App::DocumentObjectGroupPython] Sb_element001  label="Sb_element : 1"  # scripted group (container) (typed FeaturePython)
  n = 1
  ref = Sb_element
FEATURE [App::DocumentObjectGroupPython] G4_Sb  # scripted group (container) (typed FeaturePython)
  Dunit = g/cm3
  Dvalue = 6.691
  Group = -> [Sb_element001]
  conduct = 2
  density = 1
  expand = 3
  formula = Sb
  name = G4_Sb
  specific = 4
FEATURE [App::DocumentObjectGroupPython] Te_element002  label="Te_element : 002"  # scripted group (container) (typed FeaturePython)
  n = 1
  ref = Te_element
FEATURE [App::DocumentObjectGroupPython] G4_Te  # scripted group (container) (typed FeaturePython)
  Dunit = g/cm3
  Dvalue = 6.24
  Group = -> [Te_element002]
  conduct = 2
  density = 1
  expand = 3
  formula = Te
  name = G4_Te
  specific = 4
FEATURE [App::DocumentObjectGroupPython] I_element010  label="I_element : 006"  # scripted group (container) (typed FeaturePython)
  n = 1
  ref = I_element
FEATURE [App::DocumentObjectGroupPython] G4_I  # scripted group (container) (typed FeaturePython)
  Dunit = g/cm3
  Dvalue = 4.93
  Group = -> [I_element010]
  conduct = 2
  density = 1
  expand = 3
  formula = I
  name = G4_I
  specific = 4
FEATURE [App::DocumentObjectGroupPython] Xe_element001  label="Xe_element : 1"  # scripted group (container) (typed FeaturePython)
  n = 1
  ref = Xe_element
FEATURE [App::DocumentObjectGroupPython] G4_Xe  # scripted group (container) (typed FeaturePython)
  Dunit = g/cm3
  Dvalue = 0.00548536
  Group = -> [Xe_element001]
  conduct = 2
  density = 1
  expand = 3
  formula = Xe
  name = G4_Xe
  specific = 4
FEATURE [App::DocumentObjectGroupPython] Cs_element003  label="Cs_element : 003"  # scripted group (container) (typed FeaturePython)
  n = 1
  ref = Cs_element
FEATURE [App::DocumentObjectGroupPython] G4_Cs  # scripted group (container) (typed FeaturePython)
  Dunit = g/cm3
  Dvalue = 1.873
  Group = -> [Cs_element003]
  conduct = 2
  density = 1
  expand = 3
  formula = Cs
  name = G4_Cs
  specific = 4
FEATURE [App::DocumentObjectGroupPython] Ba_element003  label="Ba_element : 003"  # scripted group (container) (typed FeaturePython)
  n = 1
  ref = Ba_element
FEATURE [App::DocumentObjectGroupPython] G4_Ba  # scripted group (container) (typed FeaturePython)
  Dunit = g/cm3
  Dvalue = 3.5
  Group = -> [Ba_element003]
  conduct = 2
  density = 1
  expand = 3
  formula = Ba
  name = G4_Ba
  specific = 4
FEATURE [App::DocumentObjectGroupPython] La_element003  label="La_element : 003"  # scripted group (container) (typed FeaturePython)
  n = 1
  ref = La_element
FEATURE [App::DocumentObjectGroupPython] G4_La  # scripted group (container) (typed FeaturePython)
  Dunit = g/cm3
  Dvalue = 6.154
  Group = -> [La_element003]
  conduct = 2
  density = 1
  expand = 3
  formula = La
  name = G4_La
  specific = 4
FEATURE [App::DocumentObjectGroupPython] Ce_element002  label="Ce_element : 1"  # scripted group (container) (typed FeaturePython)
  n = 1
  ref = Ce_element
FEATURE [App::DocumentObjectGroupPython] G4_Ce  # scripted group (container) (typed FeaturePython)
  Dunit = g/cm3
  Dvalue = 6.657
  Group = -> [Ce_element002]
  conduct = 2
  density = 1
  expand = 3
  formula = Ce
  name = G4_Ce
  specific = 4
FEATURE [App::DocumentObjectGroupPython] Pr_element001  label="Pr_element : 1"  # scripted group (container) (typed FeaturePython)
  n = 1
  ref = Pr_element
FEATURE [App::DocumentObjectGroupPython] G4_Pr  # scripted group (container) (typed FeaturePython)
  Dunit = g/cm3
  Dvalue = 6.71
  Group = -> [Pr_element001]
  conduct = 2
  density = 1
  expand = 3
  formula = Pr
  name = G4_Pr
  specific = 4
FEATURE [App::DocumentObjectGroupPython] Nd_element001  label="Nd_element : 1"  # scripted group (container) (typed FeaturePython)
  n = 1
  ref = Nd_element
FEATURE [App::DocumentObjectGroupPython] G4_Nd  # scripted group (container) (typed FeaturePython)
  Dunit = g/cm3
  Dvalue = 6.9
  Group = -> [Nd_element001]
  conduct = 2
  density = 1
  expand = 3
  formula = Nd
  name = G4_Nd
  specific = 4
FEATURE [App::DocumentObjectGroupPython] Pm_element001  label="Pm_element : 1"  # scripted group (container) (typed FeaturePython)
  n = 1
  ref = Pm_element
FEATURE [App::DocumentObjectGroupPython] G4_Pm  # scripted group (container) (typed FeaturePython)
  Dunit = g/cm3
  Dvalue = 7.22
  Group = -> [Pm_element001]
  conduct = 2
  density = 1
  expand = 3
  formula = Pm
  name = G4_Pm
  specific = 4
FEATURE [App::DocumentObjectGroupPython] Sm_element001  label="Sm_element : 1"  # scripted group (container) (typed FeaturePython)
  n = 1
  ref = Sm_element
FEATURE [App::DocumentObjectGroupPython] G4_Sm  # scripted group (container) (typed FeaturePython)
  Dunit = g/cm3
  Dvalue = 7.46
  Group = -> [Sm_element001]
  conduct = 2
  density = 1
  expand = 3
  formula = Sm
  name = G4_Sm
  specific = 4
FEATURE [App::DocumentObjectGroupPython] Eu_element001  label="Eu_element : 1"  # scripted group (container) (typed FeaturePython)
  n = 1
  ref = Eu_element
FEATURE [App::DocumentObjectGroupPython] G4_Eu  # scripted group (container) (typed FeaturePython)
  Dunit = g/cm3
  Dvalue = 5.243
  Group = -> [Eu_element001]
  conduct = 2
  density = 1
  expand = 3
  formula = Eu
  name = G4_Eu
  specific = 4
FEATURE [App::DocumentObjectGroupPython] Gd_element002  label="Gd_element : 1"  # scripted group (container) (typed FeaturePython)
  n = 1
  ref = Gd_element
FEATURE [App::DocumentObjectGroupPython] G4_Gd  # scripted group (container) (typed FeaturePython)
  Dunit = g/cm3
  Dvalue = 7.9004
  Group = -> [Gd_element002]
  conduct = 2
  density = 1
  expand = 3
  formula = Gd
  name = G4_Gd
  specific = 4
FEATURE [App::DocumentObjectGroupPython] Tb_element001  label="Tb_element : 1"  # scripted group (container) (typed FeaturePython)
  n = 1
  ref = Tb_element
FEATURE [App::DocumentObjectGroupPython] G4_Tb  # scripted group (container) (typed FeaturePython)
  Dunit = g/cm3
  Dvalue = 8.229
  Group = -> [Tb_element001]
  conduct = 2
  density = 1
  expand = 3
  formula = Tb
  name = G4_Tb
  specific = 4
FEATURE [App::DocumentObjectGroupPython] Dy_element001  label="Dy_element : 1"  # scripted group (container) (typed FeaturePython)
  n = 1
  ref = Dy_element
FEATURE [App::DocumentObjectGroupPython] G4_Dy  # scripted group (container) (typed FeaturePython)
  Dunit = g/cm3
  Dvalue = 8.55
  Group = -> [Dy_element001]
  conduct = 2
  density = 1
  expand = 3
  formula = Dy
  name = G4_Dy
  specific = 4
FEATURE [App::DocumentObjectGroupPython] Ho_element001  label="Ho_element : 1"  # scripted group (container) (typed FeaturePython)
  n = 1
  ref = Ho_element
FEATURE [App::DocumentObjectGroupPython] G4_Ho  # scripted group (container) (typed FeaturePython)
  Dunit = g/cm3
  Dvalue = 8.795
  Group = -> [Ho_element001]
  conduct = 2
  density = 1
  expand = 3
  formula = Ho
  name = G4_Ho
  specific = 4
FEATURE [App::DocumentObjectGroupPython] Er_element001  label="Er_element : 1"  # scripted group (container) (typed FeaturePython)
  n = 1
  ref = Er_element
FEATURE [App::DocumentObjectGroupPython] G4_Er  # scripted group (container) (typed FeaturePython)
  Dunit = g/cm3
  Dvalue = 9.066
  Group = -> [Er_element001]
  conduct = 2
  density = 1
  expand = 3
  formula = Er
  name = G4_Er
  specific = 4
FEATURE [App::DocumentObjectGroupPython] Tm_element001  label="Tm_element : 1"  # scripted group (container) (typed FeaturePython)
  n = 1
  ref = Tm_element
FEATURE [App::DocumentObjectGroupPython] G4_Tm  # scripted group (container) (typed FeaturePython)
  Dunit = g/cm3
  Dvalue = 9.321
  Group = -> [Tm_element001]
  conduct = 2
  density = 1
  expand = 3
  formula = Tm
  name = G4_Tm
  specific = 4
FEATURE [App::DocumentObjectGroupPython] Yb_element001  label="Yb_element : 1"  # scripted group (container) (typed FeaturePython)
  n = 1
  ref = Yb_element
FEATURE [App::DocumentObjectGroupPython] G4_Yb  # scripted group (container) (typed FeaturePython)
  Dunit = g/cm3
  Dvalue = 6.73
  Group = -> [Yb_element001]
  conduct = 2
  density = 1
  expand = 3
  formula = Yb
  name = G4_Yb
  specific = 4
FEATURE [App::DocumentObjectGroupPython] Lu_element001  label="Lu_element : 1"  # scripted group (container) (typed FeaturePython)
  n = 1
  ref = Lu_element
FEATURE [App::DocumentObjectGroupPython] G4_Lu  # scripted group (container) (typed FeaturePython)
  Dunit = g/cm3
  Dvalue = 9.84
  Group = -> [Lu_element001]
  conduct = 2
  density = 1
  expand = 3
  formula = Lu
  name = G4_Lu
  specific = 4
FEATURE [App::DocumentObjectGroupPython] Hf_element001  label="Hf_element : 1"  # scripted group (container) (typed FeaturePython)
  n = 1
  ref = Hf_element
FEATURE [App::DocumentObjectGroupPython] G4_Hf  # scripted group (container) (typed FeaturePython)
  Dunit = g/cm3
  Dvalue = 13.31
  Group = -> [Hf_element001]
  conduct = 2
  density = 1
  expand = 3
  formula = Hf
  name = G4_Hf
  specific = 4
FEATURE [App::DocumentObjectGroupPython] Ta_element001  label="Ta_element : 1"  # scripted group (container) (typed FeaturePython)
  n = 1
  ref = Ta_element
FEATURE [App::DocumentObjectGroupPython] G4_Ta  # scripted group (container) (typed FeaturePython)
  Dunit = g/cm3
  Dvalue = 16.654
  Group = -> [Ta_element001]
  conduct = 2
  density = 1
  expand = 3
  formula = Ta
  name = G4_Ta
  specific = 4
FEATURE [App::DocumentObjectGroupPython] W_element004  label="W_element : 004"  # scripted group (container) (typed FeaturePython)
  n = 1
  ref = W_element
FEATURE [App::DocumentObjectGroupPython] G4_W  # scripted group (container) (typed FeaturePython)
  Dunit = g/cm3
  Dvalue = 19.3
  Group = -> [W_element004]
  conduct = 2
  density = 1
  expand = 3
  formula = W
  name = G4_W
  specific = 4
FEATURE [App::DocumentObjectGroupPython] Re_element001  label="Re_element : 1"  # scripted group (container) (typed FeaturePython)
  n = 1
  ref = Re_element
FEATURE [App::DocumentObjectGroupPython] G4_Re  # scripted group (container) (typed FeaturePython)
  Dunit = g/cm3
  Dvalue = 21.02
  Group = -> [Re_element001]
  conduct = 2
  density = 1
  expand = 3
  formula = Re
  name = G4_Re
  specific = 4
FEATURE [App::DocumentObjectGroupPython] Os_element001  label="Os_element : 1"  # scripted group (container) (typed FeaturePython)
  n = 1
  ref = Os_element
FEATURE [App::DocumentObjectGroupPython] G4_Os  # scripted group (container) (typed FeaturePython)
  Dunit = g/cm3
  Dvalue = 22.57
  Group = -> [Os_element001]
  conduct = 2
  density = 1
  expand = 3
  formula = Os
  name = G4_Os
  specific = 4
FEATURE [App::DocumentObjectGroupPython] Ir_element001  label="Ir_element : 1"  # scripted group (container) (typed FeaturePython)
  n = 1
  ref = Ir_element
FEATURE [App::DocumentObjectGroupPython] G4_Ir  # scripted group (container) (typed FeaturePython)
  Dunit = g/cm3
  Dvalue = 22.42
  Group = -> [Ir_element001]
  conduct = 2
  density = 1
  expand = 3
  formula = Ir
  name = G4_Ir
  specific = 4
FEATURE [App::DocumentObjectGroupPython] Pt_element001  label="Pt_element : 1"  # scripted group (container) (typed FeaturePython)
  n = 1
  ref = Pt_element
FEATURE [App::DocumentObjectGroupPython] G4_Pt  # scripted group (container) (typed FeaturePython)
  Dunit = g/cm3
  Dvalue = 21.45
  Group = -> [Pt_element001]
  conduct = 2
  density = 1
  expand = 3
  formula = Pt
  name = G4_Pt
  specific = 4
FEATURE [App::DocumentObjectGroupPython] Au_element001  label="Au_element : 1"  # scripted group (container) (typed FeaturePython)
  n = 1
  ref = Au_element
FEATURE [App::DocumentObjectGroupPython] G4_Au  # scripted group (container) (typed FeaturePython)
  Dunit = g/cm3
  Dvalue = 19.32
  Group = -> [Au_element001]
  conduct = 2
  density = 1
  expand = 3
  formula = Au
  name = G4_Au
  specific = 4
FEATURE [App::DocumentObjectGroupPython] Hg_element002  label="Hg_element : 002"  # scripted group (container) (typed FeaturePython)
  n = 1
  ref = Hg_element
FEATURE [App::DocumentObjectGroupPython] G4_Hg  # scripted group (container) (typed FeaturePython)
  Dunit = g/cm3
  Dvalue = 13.546
  Group = -> [Hg_element002]
  conduct = 2
  density = 1
  expand = 3
  formula = Hg
  name = G4_Hg
  specific = 4
FEATURE [App::DocumentObjectGroupPython] Tl_element002  label="Tl_element : 002"  # scripted group (container) (typed FeaturePython)
  n = 1
  ref = Tl_element
FEATURE [App::DocumentObjectGroupPython] G4_Tl  # scripted group (container) (typed FeaturePython)
  Dunit = g/cm3
  Dvalue = 11.72
  Group = -> [Tl_element002]
  conduct = 2
  density = 1
  expand = 3
  formula = Tl
  name = G4_Tl
  specific = 4
FEATURE [App::DocumentObjectGroupPython] Pb_element003  label="Pb_element : 1"  # scripted group (container) (typed FeaturePython)
  n = 1
  ref = Pb_element
FEATURE [App::DocumentObjectGroupPython] G4_Pb  # scripted group (container) (typed FeaturePython)
  Dunit = g/cm3
  Dvalue = 11.35
  Group = -> [Pb_element003]
  conduct = 2
  density = 1
  expand = 3
  formula = Pb
  name = G4_Pb
  specific = 4
FEATURE [App::DocumentObjectGroupPython] Bi_element002  label="Bi_element : 1"  # scripted group (container) (typed FeaturePython)
  n = 1
  ref = Bi_element
FEATURE [App::DocumentObjectGroupPython] G4_Bi  # scripted group (container) (typed FeaturePython)
  Dunit = g/cm3
  Dvalue = 9.747
  Group = -> [Bi_element002]
  conduct = 2
  density = 1
  expand = 3
  formula = Bi
  name = G4_Bi
  specific = 4
FEATURE [App::DocumentObjectGroupPython] Po_element001  label="Po_element : 1"  # scripted group (container) (typed FeaturePython)
  n = 1
  ref = Po_element
FEATURE [App::DocumentObjectGroupPython] G4_Po  # scripted group (container) (typed FeaturePython)
  Dunit = g/cm3
  Dvalue = 9.32
  Group = -> [Po_element001]
  conduct = 2
  density = 1
  expand = 3
  formula = Po
  name = G4_Po
  specific = 4
FEATURE [App::DocumentObjectGroupPython] At_element001  label="At_element : 1"  # scripted group (container) (typed FeaturePython)
  n = 1
  ref = At_element
FEATURE [App::DocumentObjectGroupPython] G4_At  # scripted group (container) (typed FeaturePython)
  Dunit = g/cm3
  Dvalue = 9.32
  Group = -> [At_element001]
  conduct = 2
  density = 1
  expand = 3
  formula = At
  name = G4_At
  specific = 4
FEATURE [App::DocumentObjectGroupPython] Rn_element001  label="Rn_element : 1"  # scripted group (container) (typed FeaturePython)
  n = 1
  ref = Rn_element
FEATURE [App::DocumentObjectGroupPython] G4_Rn  # scripted group (container) (typed FeaturePython)
  Dunit = g/cm3
  Dvalue = 0.00900662
  Group = -> [Rn_element001]
  conduct = 2
  density = 1
  expand = 3
  formula = Rn
  name = G4_Rn
  specific = 4
FEATURE [App::DocumentObjectGroupPython] Fr_element001  label="Fr_element : 1"  # scripted group (container) (typed FeaturePython)
  n = 1
  ref = Fr_element
FEATURE [App::DocumentObjectGroupPython] G4_Fr  # scripted group (container) (typed FeaturePython)
  Dunit = g/cm3
  Dvalue = 1
  Group = -> [Fr_element001]
  conduct = 2
  density = 1
  expand = 3
  formula = Fr
  name = G4_Fr
  specific = 4
FEATURE [App::DocumentObjectGroupPython] Ra_element001  label="Ra_element : 1"  # scripted group (container) (typed FeaturePython)
  n = 1
  ref = Ra_element
FEATURE [App::DocumentObjectGroupPython] G4_Ra  # scripted group (container) (typed FeaturePython)
  Dunit = g/cm3
  Dvalue = 5
  Group = -> [Ra_element001]
  conduct = 2
  density = 1
  expand = 3
  formula = Ra
  name = G4_Ra
  specific = 4
FEATURE [App::DocumentObjectGroupPython] Ac_element001  label="Ac_element : 1"  # scripted group (container) (typed FeaturePython)
  n = 1
  ref = Ac_element
FEATURE [App::DocumentObjectGroupPython] G4_Ac  # scripted group (container) (typed FeaturePython)
  Dunit = g/cm3
  Dvalue = 10.07
  Group = -> [Ac_element001]
  conduct = 2
  density = 1
  expand = 3
  formula = Ac
  name = G4_Ac
  specific = 4
FEATURE [App::DocumentObjectGroupPython] Th_element001  label="Th_element : 1"  # scripted group (container) (typed FeaturePython)
  n = 1
  ref = Th_element
FEATURE [App::DocumentObjectGroupPython] G4_Th  # scripted group (container) (typed FeaturePython)
  Dunit = g/cm3
  Dvalue = 11.72
  Group = -> [Th_element001]
  conduct = 2
  density = 1
  expand = 3
  formula = Th
  name = G4_Th
  specific = 4
FEATURE [App::DocumentObjectGroupPython] Pa_element001  label="Pa_element : 1"  # scripted group (container) (typed FeaturePython)
  n = 1
  ref = Pa_element
FEATURE [App::DocumentObjectGroupPython] G4_Pa  # scripted group (container) (typed FeaturePython)
  Dunit = g/cm3
  Dvalue = 15.37
  Group = -> [Pa_element001]
  conduct = 2
  density = 1
  expand = 3
  formula = Pa
  name = G4_Pa
  specific = 4
FEATURE [App::DocumentObjectGroupPython] U_element004  label="U_element : 004"  # scripted group (container) (typed FeaturePython)
  n = 1
  ref = U_element
FEATURE [App::DocumentObjectGroupPython] G4_U  # scripted group (container) (typed FeaturePython)
  Dunit = g/cm3
  Dvalue = 18.95
  Group = -> [U_element004]
  conduct = 2
  density = 1
  expand = 3
  formula = U
  name = G4_U
  specific = 4
FEATURE [App::DocumentObjectGroupPython] Np_element001  label="Np_element : 1"  # scripted group (container) (typed FeaturePython)
  n = 1
  ref = Np_element
FEATURE [App::DocumentObjectGroupPython] G4_Np  # scripted group (container) (typed FeaturePython)
  Dunit = g/cm3
  Dvalue = 20.25
  Group = -> [Np_element001]
  conduct = 2
  density = 1
  expand = 3
  formula = Np
  name = G4_Np
  specific = 4
FEATURE [App::DocumentObjectGroupPython] Pu_element002  label="Pu_element : 002"  # scripted group (container) (typed FeaturePython)
  n = 1
  ref = Pu_element
FEATURE [App::DocumentObjectGroupPython] G4_Pu  # scripted group (container) (typed FeaturePython)
  Dunit = g/cm3
  Dvalue = 19.84
  Group = -> [Pu_element002]
  conduct = 2
  density = 1
  expand = 3
  formula = Pu
  name = G4_Pu
  specific = 4
FEATURE [App::DocumentObjectGroupPython] Am_element001  label="Am_element : 1"  # scripted group (container) (typed FeaturePython)
  n = 1
  ref = Am_element
FEATURE [App::DocumentObjectGroupPython] G4_Am  # scripted group (container) (typed FeaturePython)
  Dunit = g/cm3
  Dvalue = 13.67
  Group = -> [Am_element001]
  conduct = 2
  density = 1
  expand = 3
  formula = Am
  name = G4_Am
  specific = 4
FEATURE [App::DocumentObjectGroupPython] Cm_element001  label="Cm_element : 1"  # scripted group (container) (typed FeaturePython)
  n = 1
  ref = Cm_element
FEATURE [App::DocumentObjectGroupPython] G4_Cm  # scripted group (container) (typed FeaturePython)
  Dunit = g/cm3
  Dvalue = 13.51
  Group = -> [Cm_element001]
  conduct = 2
  density = 1
  expand = 3
  formula = Cm
  name = G4_Cm
  specific = 4
FEATURE [App::DocumentObjectGroupPython] Bk_element001  label="Bk_element : 1"  # scripted group (container) (typed FeaturePython)
  n = 1
  ref = Bk_element
FEATURE [App::DocumentObjectGroupPython] G4_Bk  # scripted group (container) (typed FeaturePython)
  Dunit = g/cm3
  Dvalue = 14
  Group = -> [Bk_element001]
  conduct = 2
  density = 1
  expand = 3
  formula = Bk
  name = G4_Bk
  specific = 4
FEATURE [App::DocumentObjectGroupPython] Cf_element001  label="Cf_element : 1"  # scripted group (container) (typed FeaturePython)
  n = 1
  ref = Cf_element
FEATURE [App::DocumentObjectGroupPython] G4_Cf  # scripted group (container) (typed FeaturePython)
  Dunit = g/cm3
  Dvalue = 10
  Group = -> [Cf_element001]
  conduct = 2
  density = 1
  expand = 3
  formula = Cf
  name = G4_Cf
  specific = 4
FEATURE [App::DocumentObjectGroupPython] Element  # scripted group (container) (typed FeaturePython)
  Group = -> [G4_H,G4_He,G4_Li,G4_Be,G4_B,G4_C,G4_N,G4_O,G4_F,G4_Ne,G4_Na,G4_Mg,G4_Al,G4_Si,G4_P,G4_S,G4_Cl,G4_Ar,G4_K,G4_Ca,G4_Sc,G4_Ti,G4_V,G4_Cr,G4_Mn,G4_Fe,G4_Co,G4_Ni,G4_Cu,G4_Zn,G4_Ga,G4_Ge,G4_As,G4_Se,G4_Br,G4_Kr,G4_Rb,G4_Sr,G4_Y,G4_Zr,G4_Nb,G4_Mo,G4_Tc,G4_Ru,G4_Rh,G4_Pd,G4_Ag,G4_Cd,G4_In,G4_Sn,G4_Sb,G4_Te,G4_I,G4_Xe,G4_Cs,G4_Ba,G4_La,G4_Ce,G4_Pr,G4_Nd,G4_Pm,G4_Sm,G4_Eu,G4_Gd,G4_Tb,G4_Dy,G4_Ho,G4_Er,+30 more]
FEATURE [App::DocumentObjectGroupPython] H_element114  label="H_element : 063"  # scripted group (container) (typed FeaturePython)
  n = 2
  ref = H_element
FEATURE [App::DocumentObjectGroupPython] G4_lH2  # scripted group (container) (typed FeaturePython)
  Dunit = g/cm3
  Dvalue = 0.0708
  Group = -> [H_element114]
  conduct = 2
  density = 1
  expand = 3
  formula = G4_lH2
  name = G4_lH2
  specific = 4
FEATURE [App::DocumentObjectGroupPython] N_element049  label="N_element : 022"  # scripted group (container) (typed FeaturePython)
  n = 2
  ref = N_element
FEATURE [App::DocumentObjectGroupPython] G4_lN2  # scripted group (container) (typed FeaturePython)
  Dunit = g/cm3
  Dvalue = 0.807
  Group = -> [N_element049]
  conduct = 2
  density = 1
  expand = 3
  formula = G4_lN2
  name = G4_lN2
  specific = 4
FEATURE [App::DocumentObjectGroupPython] O_element106  label="O_element : 060"  # scripted group (container) (typed FeaturePython)
  n = 2
  ref = O_element
FEATURE [App::DocumentObjectGroupPython] G4_lO2  # scripted group (container) (typed FeaturePython)
  Dunit = g/cm3
  Dvalue = 1.141
  Group = -> [O_element106]
  conduct = 2
  density = 1
  expand = 3
  formula = G4_lO2
  name = G4_lO2
  specific = 4
FEATURE [App::DocumentObjectGroupPython] Ar  label="Ar : 1"  # scripted group (container) (typed FeaturePython)
  n = 1
  ref = Ar
FEATURE [App::DocumentObjectGroupPython] G4_lAr  # scripted group (container) (typed FeaturePython)
  Dunit = g/cm3
  Dvalue = 1.396
  Group = -> [Ar]
  conduct = 2
  density = 1
  expand = 3
  formula = G4_lAr
  name = G4_lAr
  specific = 4
FEATURE [App::DocumentObjectGroupPython] Br  label="Br : 1"  # scripted group (container) (typed FeaturePython)
  n = 1
  ref = Br
FEATURE [App::DocumentObjectGroupPython] G4_lBr  # scripted group (container) (typed FeaturePython)
  Dunit = g/cm3
  Dvalue = 3.1028
  Group = -> [Br]
  conduct = 2
  density = 1
  expand = 3
  formula = G4_lBr
  name = G4_lBr
  specific = 4
FEATURE [App::DocumentObjectGroupPython] Kr  label="Kr : 1"  # scripted group (container) (typed FeaturePython)
  n = 1
  ref = Kr
FEATURE [App::DocumentObjectGroupPython] G4_lKr  # scripted group (container) (typed FeaturePython)
  Dunit = g/cm3
  Dvalue = 2.418
  Group = -> [Kr]
  conduct = 2
  density = 1
  expand = 3
  formula = G4_lKr
  name = G4_lKr
  specific = 4
FEATURE [App::DocumentObjectGroupPython] Xe  label="Xe : 1"  # scripted group (container) (typed FeaturePython)
  n = 1
  ref = Xe
FEATURE [App::DocumentObjectGroupPython] G4_lXe  # scripted group (container) (typed FeaturePython)
  Dunit = g/cm3
  Dvalue = 2.953
  Group = -> [Xe]
  conduct = 2
  density = 1
  expand = 3
  formula = G4_lXe
  name = G4_lXe
  specific = 4
FEATURE [App::DocumentObjectGroupPython] O_element107  label="O_element : 061"  # scripted group (container) (typed FeaturePython)
  n = 4
  ref = O_element
FEATURE [App::DocumentObjectGroupPython] Pb_element004  label="Pb_element : 002"  # scripted group (container) (typed FeaturePython)
  n = 1
  ref = Pb_element
FEATURE [App::DocumentObjectGroupPython] W_element005  label="W_element : 005"  # scripted group (container) (typed FeaturePython)
  n = 1
  ref = W_element
FEATURE [App::DocumentObjectGroupPython] G4_PbWO4  # scripted group (container) (typed FeaturePython)
  Dunit = g/cm3
  Dvalue = 8.28
  Group = -> [O_element107,Pb_element004,W_element005]
  conduct = 2
  density = 1
  expand = 3
  formula = G4_PbWO4
  name = G4_PbWO4
  specific = 4
FEATURE [App::DocumentObjectGroupPython] alactic  label="alactic : 1"  # scripted group (container) (typed FeaturePython)
  n = 1
  ref = alactic
FEATURE [App::DocumentObjectGroupPython] G4_Galactic  # scripted group (container) (typed FeaturePython)
  Dunit = g/cm3
  Dvalue = 0
  Group = -> [alactic]
  conduct = 2
  density = 1
  expand = 3
  formula = G4_Galactic
  name = G4_Galactic
  specific = 4
FEATURE [App::DocumentObjectGroupPython] RAPHITE_POROUS  label="RAPHITE_POROUS : 1"  # scripted group (container) (typed FeaturePython)
  n = 1
  ref = RAPHITE_POROUS
FEATURE [App::DocumentObjectGroupPython] G4_GRAPHITE_POROUS  # scripted group (container) (typed FeaturePython)
  Dunit = g/cm3
  Dvalue = 1.7
  Group = -> [RAPHITE_POROUS]
  conduct = 2
  density = 1
  expand = 3
  formula = G4_GRAPHITE_POROUS
  name = G4_GRAPHITE_POROUS
  specific = 4
FEATURE [App::DocumentObjectGroupPython] H_element115  label="H_element : 0.150"  # scripted group (container) (typed FeaturePython)
  n = 0.080538
FEATURE [App::DocumentObjectGroupPython] C_element125  label="C_element : 0.600"  # scripted group (container) (typed FeaturePython)
  n = 0.599848
FEATURE [App::DocumentObjectGroupPython] O_element108  label="O_element : 0.320"  # scripted group (container) (typed FeaturePython)
  n = 0.319614
FEATURE [App::DocumentObjectGroupPython] G4_LUCITE  # scripted group (container) (typed FeaturePython)
  Dunit = g/cm3
  Dvalue = 1.19
  Group = -> [H_element115,C_element125,O_element108]
  conduct = 2
  density = 1
  expand = 3
  formula = G4_LUCITE
  name = G4_LUCITE
  specific = 4
FEATURE [App::DocumentObjectGroupPython] Cu_element002  label="Cu_element : 62"  # scripted group (container) (typed FeaturePython)
  n = 62
  ref = Cu_element
FEATURE [App::DocumentObjectGroupPython] Zn_element002  label="Zn_element : 35"  # scripted group (container) (typed FeaturePython)
  n = 35
  ref = Zn_element
FEATURE [App::DocumentObjectGroupPython] Pb_element005  label="Pb_element : 3"  # scripted group (container) (typed FeaturePython)
  n = 3
  ref = Pb_element
FEATURE [App::DocumentObjectGroupPython] G4_BRASS  # scripted group (container) (typed FeaturePython)
  Dunit = g/cm3
  Dvalue = 8.52
  Group = -> [Cu_element002,Zn_element002,Pb_element005]
  conduct = 2
  density = 1
  expand = 3
  formula = G4_BRASS
  name = G4_BRASS
  specific = 4
FEATURE [App::DocumentObjectGroupPython] Cu_element003  label="Cu_element : 89"  # scripted group (container) (typed FeaturePython)
  n = 89
  ref = Cu_element
FEATURE [App::DocumentObjectGroupPython] Zn_element003  label="Zn_element : 9"  # scripted group (container) (typed FeaturePython)
  n = 9
  ref = Zn_element
FEATURE [App::DocumentObjectGroupPython] Pb_element006  label="Pb_element : 2"  # scripted group (container) (typed FeaturePython)
  n = 2
  ref = Pb_element
FEATURE [App::DocumentObjectGroupPython] G4_BRONZE  # scripted group (container) (typed FeaturePython)
  Dunit = g/cm3
  Dvalue = 8.82
  Group = -> [Cu_element003,Zn_element003,Pb_element006]
  conduct = 2
  density = 1
  expand = 3
  formula = G4_BRONZE
  name = G4_BRONZE
  specific = 4
FEATURE [App::DocumentObjectGroupPython] Fe_element008  label="Fe_element : 74"  # scripted group (container) (typed FeaturePython)
  n = 74
  ref = Fe_element
FEATURE [App::DocumentObjectGroupPython] Cr_element002  label="Cr_element : 18"  # scripted group (container) (typed FeaturePython)
  n = 18
  ref = Cr_element
FEATURE [App::DocumentObjectGroupPython] Ni_element002  label="Ni_element : 8"  # scripted group (container) (typed FeaturePython)
  n = 8
  ref = Ni_element
FEATURE [App::DocumentObjectGroupPython] G4_STAINLESS_STEEL  label="G4_STAINLESS-STEEL"  # scripted group (container) (typed FeaturePython)
  Dunit = g/cm3
  Dvalue = 8
  Group = -> [Fe_element008,Cr_element002,Ni_element002]
  conduct = 2
  density = 1
  expand = 3
  formula = G4_STAINLESS-STEEL
  name = G4_STAINLESS-STEEL
  specific = 4
FEATURE [App::DocumentObjectGroupPython] H_element116  label="H_element : 064"  # scripted group (container) (typed FeaturePython)
  n = 18
  ref = H_element
FEATURE [App::DocumentObjectGroupPython] C_element126  label="C_element : 071"  # scripted group (container) (typed FeaturePython)
  n = 12
  ref = C_element
FEATURE [App::DocumentObjectGroupPython] O_element109  label="O_element : 062"  # scripted group (container) (typed FeaturePython)
  n = 7
  ref = O_element
FEATURE [App::DocumentObjectGroupPython] G4_CR39  # scripted group (container) (typed FeaturePython)
  Dunit = g/cm3
  Dvalue = 1.32
  Group = -> [H_element116,C_element126,O_element109]
  conduct = 2
  density = 1
  expand = 3
  formula = G4_CR39
  name = G4_CR39
  specific = 4
FEATURE [App::DocumentObjectGroupPython] H_element117  label="H_element : 38"  # scripted group (container) (typed FeaturePython)
  n = 38
  ref = H_element
FEATURE [App::DocumentObjectGroupPython] C_element127  label="C_element : 072"  # scripted group (container) (typed FeaturePython)
  n = 18
  ref = C_element
FEATURE [App::DocumentObjectGroupPython] O_element110  label="O_element : 063"  # scripted group (container) (typed FeaturePython)
  n = 1
  ref = O_element
FEATURE [App::DocumentObjectGroupPython] G4_OCTADECANOL  # scripted group (container) (typed FeaturePython)
  Dunit = g/cm3
  Dvalue = 0.812
  Group = -> [H_element117,C_element127,O_element110]
  conduct = 2
  density = 1
  expand = 3
  formula = G4_OCTADECANOL
  name = G4_OCTADECANOL
  specific = 4
FEATURE [App::DocumentObjectGroupPython] HEP  # scripted group (container) (typed FeaturePython)
  Group = -> [G4_lH2,G4_lN2,G4_lO2,G4_lAr,G4_lBr,G4_lKr,G4_lXe,G4_PbWO4,G4_Galactic,G4_GRAPHITE_POROUS,G4_LUCITE,G4_BRASS,G4_BRONZE,G4_STAINLESS_STEEL,G4_CR39,G4_OCTADECANOL]
FEATURE [App::DocumentObjectGroupPython] C_element128  label="C_element : 073"  # scripted group (container) (typed FeaturePython)
  n = 14
  ref = C_element
FEATURE [App::DocumentObjectGroupPython] H_element118  label="H_element : 065"  # scripted group (container) (typed FeaturePython)
  n = 10
  ref = H_element
FEATURE [App::DocumentObjectGroupPython] O_element111  label="O_element : 064"  # scripted group (container) (typed FeaturePython)
  n = 2
  ref = O_element
FEATURE [App::DocumentObjectGroupPython] N_element050  label="N_element : 023"  # scripted group (container) (typed FeaturePython)
  n = 2
  ref = N_element
FEATURE [App::DocumentObjectGroupPython] G4_KEVLAR  # scripted group (container) (typed FeaturePython)
  Dunit = g/cm3
  Dvalue = 1.44
  Group = -> [C_element128,H_element118,O_element111,N_element050]
  conduct = 2
  density = 1
  expand = 3
  formula = G4_KEVLAR
  name = G4_KEVLAR
  specific = 4
FEATURE [App::DocumentObjectGroupPython] C_element129  label="C_element : 074"  # scripted group (container) (typed FeaturePython)
  n = 10
  ref = C_element
FEATURE [App::DocumentObjectGroupPython] H_element119  label="H_element : 066"  # scripted group (container) (typed FeaturePython)
  n = 8
  ref = H_element
FEATURE [App::DocumentObjectGroupPython] O_element112  label="O_element : 065"  # scripted group (container) (typed FeaturePython)
  n = 4
  ref = O_element
FEATURE [App::DocumentObjectGroupPython] G4_DACRON  # scripted group (container) (typed FeaturePython)
  Dunit = g/cm3
  Dvalue = 1.4
  Group = -> [C_element129,H_element119,O_element112]
  conduct = 2
  density = 1
  expand = 3
  formula = G4_DACRON
  name = G4_DACRON
  specific = 4
FEATURE [App::DocumentObjectGroupPython] C_element130  label="C_element : 075"  # scripted group (container) (typed FeaturePython)
  n = 4
  ref = C_element
FEATURE [App::DocumentObjectGroupPython] H_element120  label="H_element : 067"  # scripted group (container) (typed FeaturePython)
  n = 5
  ref = H_element
FEATURE [App::DocumentObjectGroupPython] Cl_element030  label="Cl_element : 016"  # scripted group (container) (typed FeaturePython)
  n = 1
  ref = Cl_element
FEATURE [App::DocumentObjectGroupPython] G4_NEOPRENE  # scripted group (container) (typed FeaturePython)
  Dunit = g/cm3
  Dvalue = 1.23
  Group = -> [C_element130,H_element120,Cl_element030]
  conduct = 2
  density = 1
  expand = 3
  formula = G4_NEOPRENE
  name = G4_NEOPRENE
  specific = 4
FEATURE [App::DocumentObjectGroupPython] Space  # scripted group (container) (typed FeaturePython)
  Group = -> [G4_KEVLAR,G4_DACRON,G4_NEOPRENE]
FEATURE [App::DocumentObjectGroupPython] H_element121  label="H_element : 068"  # scripted group (container) (typed FeaturePython)
  n = 5
  ref = H_element
FEATURE [App::DocumentObjectGroupPython] C_element131  label="C_element : 076"  # scripted group (container) (typed FeaturePython)
  n = 4
  ref = C_element
FEATURE [App::DocumentObjectGroupPython] N_element051  label="N_element : 3"  # scripted group (container) (typed FeaturePython)
  n = 3
  ref = N_element
FEATURE [App::DocumentObjectGroupPython] O_element113  label="O_element : 066"  # scripted group (container) (typed FeaturePython)
  n = 1
  ref = O_element
FEATURE [App::DocumentObjectGroupPython] G4_CYTOSINE  # scripted group (container) (typed FeaturePython)
  Dunit = g/cm3
  Dvalue = 1.55
  Group = -> [H_element121,C_element131,N_element051,O_element113]
  conduct = 2
  density = 1
  expand = 3
  formula = G4_CYTOSINE
  name = G4_CYTOSINE
  specific = 4
FEATURE [App::DocumentObjectGroupPython] H_element122  label="H_element : 069"  # scripted group (container) (typed FeaturePython)
  n = 6
  ref = H_element
FEATURE [App::DocumentObjectGroupPython] C_element132  label="C_element : 077"  # scripted group (container) (typed FeaturePython)
  n = 5
  ref = C_element
FEATURE [App::DocumentObjectGroupPython] N_element052  label="N_element : 024"  # scripted group (container) (typed FeaturePython)
  n = 2
  ref = N_element
FEATURE [App::DocumentObjectGroupPython] O_element114  label="O_element : 067"  # scripted group (container) (typed FeaturePython)
  n = 2
  ref = O_element
FEATURE [App::DocumentObjectGroupPython] G4_THYMINE  # scripted group (container) (typed FeaturePython)
  Dunit = g/cm3
  Dvalue = 1.23
  Group = -> [H_element122,C_element132,N_element052,O_element114]
  conduct = 2
  density = 1
  expand = 3
  formula = G4_THYMINE
  name = G4_THYMINE
  specific = 4
FEATURE [App::DocumentObjectGroupPython] H_element123  label="H_element : 070"  # scripted group (container) (typed FeaturePython)
  n = 4
  ref = H_element
FEATURE [App::DocumentObjectGroupPython] C_element133  label="C_element : 078"  # scripted group (container) (typed FeaturePython)
  n = 4
  ref = C_element
FEATURE [App::DocumentObjectGroupPython] N_element053  label="N_element : 025"  # scripted group (container) (typed FeaturePython)
  n = 2
  ref = N_element
FEATURE [App::DocumentObjectGroupPython] O_element115  label="O_element : 068"  # scripted group (container) (typed FeaturePython)
  n = 2
  ref = O_element
FEATURE [App::DocumentObjectGroupPython] G4_URACIL  # scripted group (container) (typed FeaturePython)
  Dunit = g/cm3
  Dvalue = 1.32
  Group = -> [H_element123,C_element133,N_element053,O_element115]
  conduct = 2
  density = 1
  expand = 3
  formula = G4_URACIL
  name = G4_URACIL
  specific = 4
FEATURE [App::DocumentObjectGroupPython] H_element124  label="H_element : 071"  # scripted group (container) (typed FeaturePython)
  n = 4
  ref = H_element
FEATURE [App::DocumentObjectGroupPython] C_element134  label="C_element : 079"  # scripted group (container) (typed FeaturePython)
  n = 5
  ref = C_element
FEATURE [App::DocumentObjectGroupPython] N_element054  label="N_element : 026"  # scripted group (container) (typed FeaturePython)
  n = 5
  ref = N_element
FEATURE [App::DocumentObjectGroupPython] G4_DNA_ADENINE  # scripted group (container) (typed FeaturePython)
  Dunit = g/cm3
  Dvalue = 1
  Group = -> [H_element124,C_element134,N_element054]
  conduct = 2
  density = 1
  expand = 3
  formula = G4_DNA_ADENINE
  name = G4_DNA_ADENINE
  specific = 4
FEATURE [App::DocumentObjectGroupPython] H_element125  label="H_element : 072"  # scripted group (container) (typed FeaturePython)
  n = 4
  ref = H_element
FEATURE [App::DocumentObjectGroupPython] C_element135  label="C_element : 080"  # scripted group (container) (typed FeaturePython)
  n = 5
  ref = C_element
FEATURE [App::DocumentObjectGroupPython] N_element055  label="N_element : 027"  # scripted group (container) (typed FeaturePython)
  n = 5
  ref = N_element
FEATURE [App::DocumentObjectGroupPython] O_element116  label="O_element : 069"  # scripted group (container) (typed FeaturePython)
  n = 1
  ref = O_element
FEATURE [App::DocumentObjectGroupPython] G4_DNA_GUANINE  # scripted group (container) (typed FeaturePython)
  Dunit = g/cm3
  Dvalue = 1
  Group = -> [H_element125,C_element135,N_element055,O_element116]
  conduct = 2
  density = 1
  expand = 3
  formula = G4_DNA_GUANINE
  name = G4_DNA_GUANINE
  specific = 4
FEATURE [App::DocumentObjectGroupPython] H_element126  label="H_element : 073"  # scripted group (container) (typed FeaturePython)
  n = 4
  ref = H_element
FEATURE [App::DocumentObjectGroupPython] C_element136  label="C_element : 081"  # scripted group (container) (typed FeaturePython)
  n = 4
  ref = C_element
FEATURE [App::DocumentObjectGroupPython] N_element056  label="N_element : 028"  # scripted group (container) (typed FeaturePython)
  n = 3
  ref = N_element
FEATURE [App::DocumentObjectGroupPython] O_element117  label="O_element : 070"  # scripted group (container) (typed FeaturePython)
  n = 1
  ref = O_element
FEATURE [App::DocumentObjectGroupPython] G4_DNA_CYTOSINE  # scripted group (container) (typed FeaturePython)
  Dunit = g/cm3
  Dvalue = 1
  Group = -> [H_element126,C_element136,N_element056,O_element117]
  conduct = 2
  density = 1
  expand = 3
  formula = G4_DNA_CYTOSINE
  name = G4_DNA_CYTOSINE
  specific = 4
FEATURE [App::DocumentObjectGroupPython] H_element127  label="H_element : 074"  # scripted group (container) (typed FeaturePython)
  n = 5
  ref = H_element
FEATURE [App::DocumentObjectGroupPython] C_element137  label="C_element : 082"  # scripted group (container) (typed FeaturePython)
  n = 5
  ref = C_element
FEATURE [App::DocumentObjectGroupPython] N_element057  label="N_element : 029"  # scripted group (container) (typed FeaturePython)
  n = 2
  ref = N_element
FEATURE [App::DocumentObjectGroupPython] O_element118  label="O_element : 071"  # scripted group (container) (typed FeaturePython)
  n = 2
  ref = O_element
FEATURE [App::DocumentObjectGroupPython] G4_DNA_THYMINE  # scripted group (container) (typed FeaturePython)
  Dunit = g/cm3
  Dvalue = 1
  Group = -> [H_element127,C_element137,N_element057,O_element118]
  conduct = 2
  density = 1
  expand = 3
  formula = G4_DNA_THYMINE
  name = G4_DNA_THYMINE
  specific = 4
FEATURE [App::DocumentObjectGroupPython] H_element128  label="H_element : 075"  # scripted group (container) (typed FeaturePython)
  n = 3
  ref = H_element
FEATURE [App::DocumentObjectGroupPython] C_element138  label="C_element : 083"  # scripted group (container) (typed FeaturePython)
  n = 4
  ref = C_element
FEATURE [App::DocumentObjectGroupPython] N_element058  label="N_element : 030"  # scripted group (container) (typed FeaturePython)
  n = 2
  ref = N_element
FEATURE [App::DocumentObjectGroupPython] O_element119  label="O_element : 072"  # scripted group (container) (typed FeaturePython)
  n = 2
  ref = O_element
FEATURE [App::DocumentObjectGroupPython] G4_DNA_URACIL  # scripted group (container) (typed FeaturePython)
  Dunit = g/cm3
  Dvalue = 1
  Group = -> [H_element128,C_element138,N_element058,O_element119]
  conduct = 2
  density = 1
  expand = 3
  formula = G4_DNA_URACIL
  name = G4_DNA_URACIL
  specific = 4
FEATURE [App::DocumentObjectGroupPython] H_element129  label="H_element : 076"  # scripted group (container) (typed FeaturePython)
  n = 10
  ref = H_element
FEATURE [App::DocumentObjectGroupPython] C_element139  label="C_element : 084"  # scripted group (container) (typed FeaturePython)
  n = 10
  ref = C_element
FEATURE [App::DocumentObjectGroupPython] N_element059  label="N_element : 031"  # scripted group (container) (typed FeaturePython)
  n = 5
  ref = N_element
FEATURE [App::DocumentObjectGroupPython] O_element120  label="O_element : 073"  # scripted group (container) (typed FeaturePython)
  n = 4
  ref = O_element
FEATURE [App::DocumentObjectGroupPython] G4_DNA_ADENOSINE  # scripted group (container) (typed FeaturePython)
  Dunit = g/cm3
  Dvalue = 1
  Group = -> [H_element129,C_element139,N_element059,O_element120]
  conduct = 2
  density = 1
  expand = 3
  formula = G4_DNA_ADENOSINE
  name = G4_DNA_ADENOSINE
  specific = 4
FEATURE [App::DocumentObjectGroupPython] H_element130  label="H_element : 077"  # scripted group (container) (typed FeaturePython)
  n = 10
  ref = H_element
FEATURE [App::DocumentObjectGroupPython] C_element140  label="C_element : 085"  # scripted group (container) (typed FeaturePython)
  n = 10
  ref = C_element
FEATURE [App::DocumentObjectGroupPython] N_element060  label="N_element : 032"  # scripted group (container) (typed FeaturePython)
  n = 5
  ref = N_element
FEATURE [App::DocumentObjectGroupPython] O_element121  label="O_element : 074"  # scripted group (container) (typed FeaturePython)
  n = 5
  ref = O_element
FEATURE [App::DocumentObjectGroupPython] G4_DNA_GUANOSINE  # scripted group (container) (typed FeaturePython)
  Dunit = g/cm3
  Dvalue = 1
  Group = -> [H_element130,C_element140,N_element060,O_element121]
  conduct = 2
  density = 1
  expand = 3
  formula = G4_DNA_GUANOSINE
  name = G4_DNA_GUANOSINE
  specific = 4
FEATURE [App::DocumentObjectGroupPython] H_element131  label="H_element : 078"  # scripted group (container) (typed FeaturePython)
  n = 10
  ref = H_element
FEATURE [App::DocumentObjectGroupPython] C_element141  label="C_element : 086"  # scripted group (container) (typed FeaturePython)
  n = 9
  ref = C_element
FEATURE [App::DocumentObjectGroupPython] N_element061  label="N_element : 033"  # scripted group (container) (typed FeaturePython)
  n = 3
  ref = N_element
FEATURE [App::DocumentObjectGroupPython] O_element122  label="O_element : 075"  # scripted group (container) (typed FeaturePython)
  n = 5
  ref = O_element
FEATURE [App::DocumentObjectGroupPython] G4_DNA_CYTIDINE  # scripted group (container) (typed FeaturePython)
  Dunit = g/cm3
  Dvalue = 1
  Group = -> [H_element131,C_element141,N_element061,O_element122]
  conduct = 2
  density = 1
  expand = 3
  formula = G4_DNA_CYTIDINE
  name = G4_DNA_CYTIDINE
  specific = 4
FEATURE [App::DocumentObjectGroupPython] H_element132  label="H_element : 079"  # scripted group (container) (typed FeaturePython)
  n = 9
  ref = H_element
FEATURE [App::DocumentObjectGroupPython] C_element142  label="C_element : 087"  # scripted group (container) (typed FeaturePython)
  n = 9
  ref = C_element
FEATURE [App::DocumentObjectGroupPython] N_element062  label="N_element : 034"  # scripted group (container) (typed FeaturePython)
  n = 2
  ref = N_element
FEATURE [App::DocumentObjectGroupPython] O_element123  label="O_element : 076"  # scripted group (container) (typed FeaturePython)
  n = 6
  ref = O_element
FEATURE [App::DocumentObjectGroupPython] G4_DNA_URIDINE  # scripted group (container) (typed FeaturePython)
  Dunit = g/cm3
  Dvalue = 1
  Group = -> [H_element132,C_element142,N_element062,O_element123]
  conduct = 2
  density = 1
  expand = 3
  formula = G4_DNA_URIDINE
  name = G4_DNA_URIDINE
  specific = 4
FEATURE [App::DocumentObjectGroupPython] H_element133  label="H_element : 080"  # scripted group (container) (typed FeaturePython)
  n = 11
  ref = H_element
FEATURE [App::DocumentObjectGroupPython] C_element143  label="C_element : 088"  # scripted group (container) (typed FeaturePython)
  n = 10
  ref = C_element
FEATURE [App::DocumentObjectGroupPython] N_element063  label="N_element : 035"  # scripted group (container) (typed FeaturePython)
  n = 2
  ref = N_element
FEATURE [App::DocumentObjectGroupPython] O_element124  label="O_element : 077"  # scripted group (container) (typed FeaturePython)
  n = 6
  ref = O_element
FEATURE [App::DocumentObjectGroupPython] G4_DNA_METHYLURIDINE  # scripted group (container) (typed FeaturePython)
  Dunit = g/cm3
  Dvalue = 1
  Group = -> [H_element133,C_element143,N_element063,O_element124]
  conduct = 2
  density = 1
  expand = 3
  formula = G4_DNA_METHYLURIDINE
  name = G4_DNA_METHYLURIDINE
  specific = 4
FEATURE [App::DocumentObjectGroupPython] P_element014  label="P_element : 003"  # scripted group (container) (typed FeaturePython)
  n = 1
  ref = P_element
FEATURE [App::DocumentObjectGroupPython] O_element125  label="O_element : 078"  # scripted group (container) (typed FeaturePython)
  n = 3
  ref = O_element
FEATURE [App::DocumentObjectGroupPython] G4_DNA_MONOPHOSPHATE  # scripted group (container) (typed FeaturePython)
  Dunit = g/cm3
  Dvalue = 1
  Group = -> [P_element014,O_element125]
  conduct = 2
  density = 1
  expand = 3
  formula = G4_DNA_MONOPHOSPHATE
  name = G4_DNA_MONOPHOSPHATE
  specific = 4
FEATURE [App::DocumentObjectGroupPython] H_element134  label="H_element : 081"  # scripted group (container) (typed FeaturePython)
  n = 10
  ref = H_element
FEATURE [App::DocumentObjectGroupPython] C_element144  label="C_element : 089"  # scripted group (container) (typed FeaturePython)
  n = 10
  ref = C_element
FEATURE [App::DocumentObjectGroupPython] N_element064  label="N_element : 036"  # scripted group (container) (typed FeaturePython)
  n = 5
  ref = N_element
FEATURE [App::DocumentObjectGroupPython] O_element126  label="O_element : 079"  # scripted group (container) (typed FeaturePython)
  n = 7
  ref = O_element
FEATURE [App::DocumentObjectGroupPython] P_element015  label="P_element : 004"  # scripted group (container) (typed FeaturePython)
  n = 1
  ref = P_element
FEATURE [App::DocumentObjectGroupPython] G4_DNA_A  # scripted group (container) (typed FeaturePython)
  Dunit = g/cm3
  Dvalue = 1
  Group = -> [H_element134,C_element144,N_element064,O_element126,P_element015]
  conduct = 2
  density = 1
  expand = 3
  formula = G4_DNA_A
  name = G4_DNA_A
  specific = 4
FEATURE [App::DocumentObjectGroupPython] H_element135  label="H_element : 082"  # scripted group (container) (typed FeaturePython)
  n = 10
  ref = H_element
FEATURE [App::DocumentObjectGroupPython] C_element145  label="C_element : 090"  # scripted group (container) (typed FeaturePython)
  n = 10
  ref = C_element
FEATURE [App::DocumentObjectGroupPython] N_element065  label="N_element : 037"  # scripted group (container) (typed FeaturePython)
  n = 5
  ref = N_element
FEATURE [App::DocumentObjectGroupPython] O_element127  label="O_element : 8"  # scripted group (container) (typed FeaturePython)
  n = 8
  ref = O_element
FEATURE [App::DocumentObjectGroupPython] P_element016  label="P_element : 005"  # scripted group (container) (typed FeaturePython)
  n = 1
  ref = P_element
FEATURE [App::DocumentObjectGroupPython] G4_DNA_G  # scripted group (container) (typed FeaturePython)
  Dunit = g/cm3
  Dvalue = 1
  Group = -> [H_element135,C_element145,N_element065,O_element127,P_element016]
  conduct = 2
  density = 1
  expand = 3
  formula = G4_DNA_G
  name = G4_DNA_G
  specific = 4
FEATURE [App::DocumentObjectGroupPython] H_element136  label="H_element : 083"  # scripted group (container) (typed FeaturePython)
  n = 10
  ref = H_element
FEATURE [App::DocumentObjectGroupPython] C_element146  label="C_element : 091"  # scripted group (container) (typed FeaturePython)
  n = 9
  ref = C_element
FEATURE [App::DocumentObjectGroupPython] N_element066  label="N_element : 038"  # scripted group (container) (typed FeaturePython)
  n = 3
  ref = N_element
FEATURE [App::DocumentObjectGroupPython] O_element128  label="O_element : 080"  # scripted group (container) (typed FeaturePython)
  n = 8
  ref = O_element
FEATURE [App::DocumentObjectGroupPython] P_element017  label="P_element : 006"  # scripted group (container) (typed FeaturePython)
  n = 1
  ref = P_element
FEATURE [App::DocumentObjectGroupPython] G4_DNA_C  # scripted group (container) (typed FeaturePython)
  Dunit = g/cm3
  Dvalue = 1
  Group = -> [H_element136,C_element146,N_element066,O_element128,P_element017]
  conduct = 2
  density = 1
  expand = 3
  formula = G4_DNA_C
  name = G4_DNA_C
  specific = 4
FEATURE [App::DocumentObjectGroupPython] H_element137  label="H_element : 084"  # scripted group (container) (typed FeaturePython)
  n = 9
  ref = H_element
FEATURE [App::DocumentObjectGroupPython] C_element147  label="C_element : 092"  # scripted group (container) (typed FeaturePython)
  n = 9
  ref = C_element
FEATURE [App::DocumentObjectGroupPython] N_element067  label="N_element : 039"  # scripted group (container) (typed FeaturePython)
  n = 2
  ref = N_element
FEATURE [App::DocumentObjectGroupPython] O_element129  label="O_element : 9"  # scripted group (container) (typed FeaturePython)
  n = 9
  ref = O_element
FEATURE [App::DocumentObjectGroupPython] P_element018  label="P_element : 007"  # scripted group (container) (typed FeaturePython)
  n = 1
  ref = P_element
FEATURE [App::DocumentObjectGroupPython] G4_DNA_U  # scripted group (container) (typed FeaturePython)
  Dunit = g/cm3
  Dvalue = 1
  Group = -> [H_element137,C_element147,N_element067,O_element129,P_element018]
  conduct = 2
  density = 1
  expand = 3
  formula = G4_DNA_U
  name = G4_DNA_U
  specific = 4
FEATURE [App::DocumentObjectGroupPython] H_element138  label="H_element : 085"  # scripted group (container) (typed FeaturePython)
  n = 11
  ref = H_element
FEATURE [App::DocumentObjectGroupPython] C_element148  label="C_element : 093"  # scripted group (container) (typed FeaturePython)
  n = 10
  ref = C_element
FEATURE [App::DocumentObjectGroupPython] N_element068  label="N_element : 040"  # scripted group (container) (typed FeaturePython)
  n = 2
  ref = N_element
FEATURE [App::DocumentObjectGroupPython] O_element130  label="O_element : 081"  # scripted group (container) (typed FeaturePython)
  n = 9
  ref = O_element
FEATURE [App::DocumentObjectGroupPython] P_element019  label="P_element : 008"  # scripted group (container) (typed FeaturePython)
  n = 1
  ref = P_element
FEATURE [App::DocumentObjectGroupPython] G4_DNA_MU  # scripted group (container) (typed FeaturePython)
  Dunit = g/cm3
  Dvalue = 1
  Group = -> [H_element138,C_element148,N_element068,O_element130,P_element019]
  conduct = 2
  density = 1
  expand = 3
  formula = G4_DNA_MU
  name = G4_DNA_MU
  specific = 4
FEATURE [App::DocumentObjectGroupPython] BioChemical  # scripted group (container) (typed FeaturePython)
  Group = -> [G4_CYTOSINE,G4_THYMINE,G4_URACIL,G4_DNA_ADENINE,G4_DNA_GUANINE,G4_DNA_CYTOSINE,G4_DNA_THYMINE,G4_DNA_URACIL,G4_DNA_ADENOSINE,G4_DNA_GUANOSINE,G4_DNA_CYTIDINE,G4_DNA_URIDINE,G4_DNA_METHYLURIDINE,G4_DNA_MONOPHOSPHATE,G4_DNA_A,G4_DNA_G,G4_DNA_C,G4_DNA_U,G4_DNA_MU]
FEATURE [App::DocumentObjectGroupPython] G4Materials  # scripted group (container) (typed FeaturePython)
  Group = -> [NIST,Element,HEP,Space,BioChemical]
  version = 1
FEATURE [App::DocumentObjectGroupPython] Geant4  # scripted group (container) (typed FeaturePython)
  Group = -> [G4Isotopes,G4Elements,G4Materials]
FEATURE [App::DocumentObjectGroupPython] Materials  # scripted group (container) (typed FeaturePython)
  Group = -> [Geant4]
FEATURE [Part::FeaturePython] GDMLBox_WorldBox  # WARN: FeaturePython — macro-defined, semantics opaque (R4)
  lunit = 2
  material = 5
  x = 200
  y = 200
  z = 200
FEATURE [Part::FeaturePython] GDMLSphere_Sphere  # WARN: FeaturePython — macro-defined, semantics opaque (R4)
  Placement = pos=(20,0,0) rot=(0,0,1;0rad)
  aunit = 0
  deltaphi = 2.02
  deltatheta = 2.02
  lunit = 2
  material = 18
  rmax = 20
  rmin = 10
  startphi = 0
  starttheta = 0
FEATURE [Part::FeaturePython] GDMLTorus_Torus  # WARN: FeaturePython — macro-defined, semantics opaque (R4)
  aunit = deg
  deltaphi = 360
  lunit = 2
  material = 5
  rmax = 5
  rmin = 0
  rtor = 10
  startphi = 10
FEATURE [Part::MultiFuse] Fusion
  Placement = pos=(30,0,0) rot=(0,0,1;0rad)
  Shapes = -> [GDMLSphere_Sphere,GDMLTorus_Torus]
  material = 18
FEATURE [Part::FeaturePython] Array  # Draft array (typed FeaturePython)
  Angle = 360
  ArrayType = 1
  Axis = (0,0,1)
  Base = -> Fusion
  Center = (0,0,0)
  Fuse = false
  IntervalAxis = (0,0,0)
  IntervalX = (50,0,0)
  IntervalY = (0,50,0)
  IntervalZ = (0,0,50)
  NumberCircles = 3
  NumberPolar = 5
  NumberX = 2
  NumberY = 2
  NumberZ = 1
  RadialDistance = 50
  Symmetry = 1
  TangentialDistance = 25
  material = 261
FEATURE [App::Part] Part
  Group = -> [GDMLSphere_Sphere,GDMLTorus_Torus,Fusion,Array]
  Origin = -> Origin001
FEATURE [App::Part] worldVOL
  Group = -> [GDMLBox_WorldBox,Part]
  Origin = -> Origin
